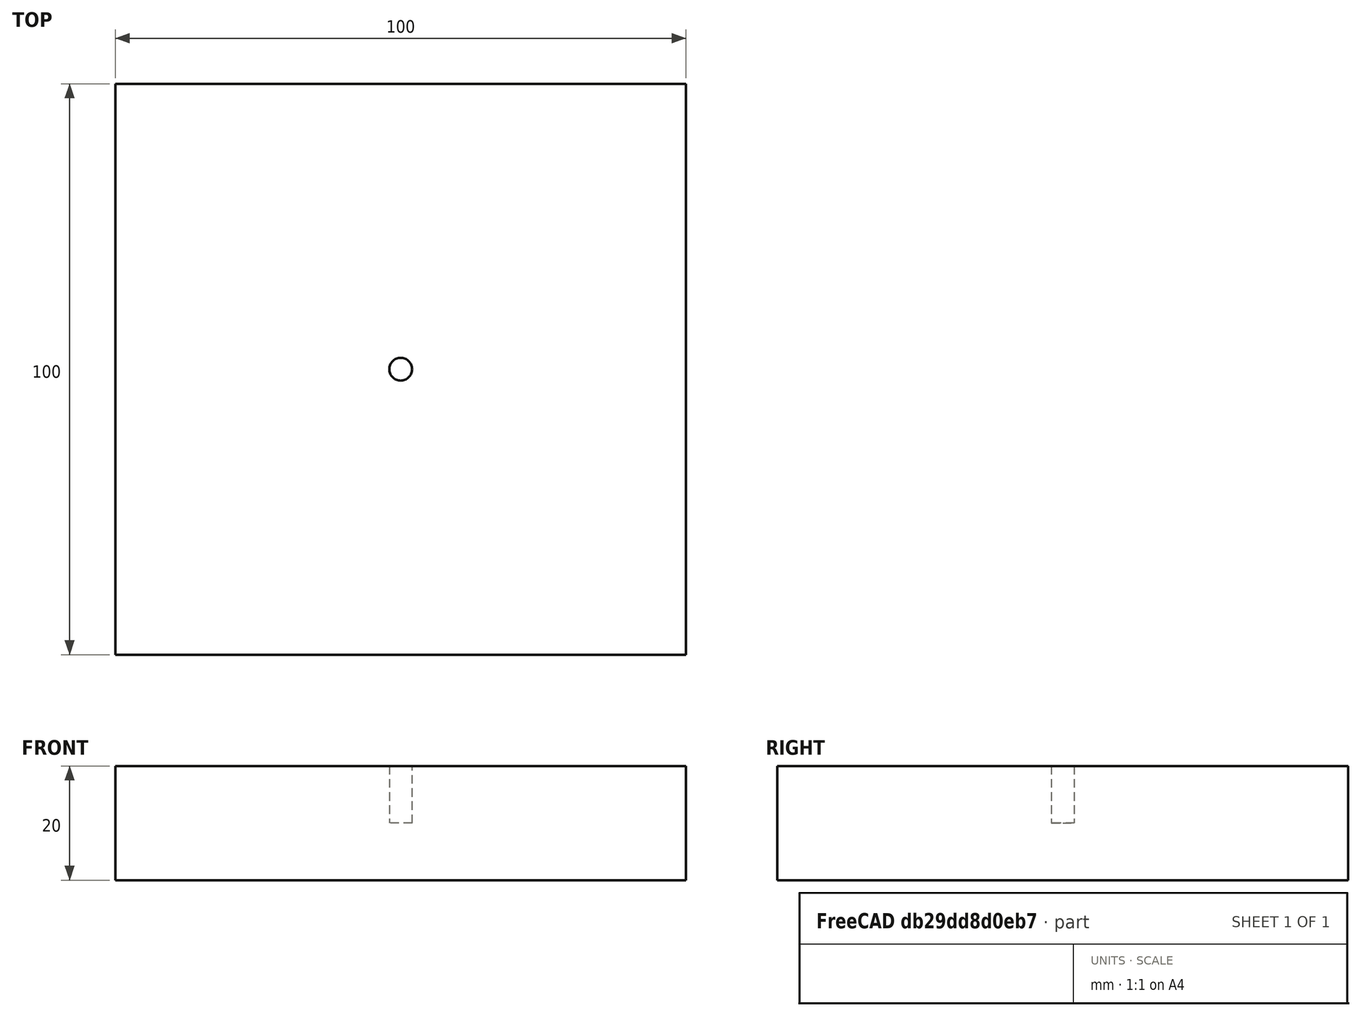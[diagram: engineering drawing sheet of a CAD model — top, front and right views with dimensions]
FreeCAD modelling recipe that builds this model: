
FCSTD DOCUMENT  (FreeCAD 0.19R24291 (Git))
Label: TestExtrudeSketch-Circle
License: All rights reserved
LicenseURL: http://en.wikipedia.org/wiki/All_rights_reserved
objects: App::DocumentObjectGroupPython×1089, Part::FeaturePython×1, Sketcher::SketchObject×1, Part::Extrusion×1, App::Part×1
note: 3 computed .brp shape members not serialized (recipe doc carries the construction recipe); baked Part::Feature solids carry a one-line shape summary decoded from their .brp

FEATURE [App::DocumentObjectGroupPython] HALFPI  # scripted group (container) (typed FeaturePython)
  name = HALFPI
  value = pi/2.
FEATURE [App::DocumentObjectGroupPython] PI  # scripted group (container) (typed FeaturePython)
  name = PI
  value = 1.*pi
FEATURE [App::DocumentObjectGroupPython] TWOPI  # scripted group (container) (typed FeaturePython)
  name = TWOPI
  value = 2.*pi
FEATURE [App::DocumentObjectGroupPython] Constants  # scripted group (container) (typed FeaturePython)
  Group = -> [HALFPI,PI,TWOPI]
FEATURE [App::DocumentObjectGroupPython] Variables  # scripted group (container) (typed FeaturePython)
FEATURE [App::DocumentObjectGroupPython] Quantities  # scripted group (container) (typed FeaturePython)
FEATURE [App::DocumentObjectGroupPython] Isotopes  # scripted group (container) (typed FeaturePython)
FEATURE [App::DocumentObjectGroupPython] Elements  # scripted group (container) (typed FeaturePython)
FEATURE [App::DocumentObjectGroupPython] Materials  # scripted group (container) (typed FeaturePython)
FEATURE [App::DocumentObjectGroupPython] G4Isotopes  # scripted group (container) (typed FeaturePython)
FEATURE [App::DocumentObjectGroupPython] H_element  # scripted group (container) (typed FeaturePython)
  Z = 1
  atom_value = 1.008
  formula = H
  name = H_element
FEATURE [App::DocumentObjectGroupPython] He_element  # scripted group (container) (typed FeaturePython)
  Z = 2
  atom_value = 4.0026
  formula = He
  name = He_element
FEATURE [App::DocumentObjectGroupPython] Li_element  # scripted group (container) (typed FeaturePython)
  Z = 3
  atom_value = 6.94
  formula = Li
  name = Li_element
FEATURE [App::DocumentObjectGroupPython] Be_element  # scripted group (container) (typed FeaturePython)
  Z = 4
  atom_value = 9.01218
  formula = Be
  name = Be_element
FEATURE [App::DocumentObjectGroupPython] B_element  # scripted group (container) (typed FeaturePython)
  Z = 5
  atom_value = 10.81
  formula = B
  name = B_element
FEATURE [App::DocumentObjectGroupPython] C_element  # scripted group (container) (typed FeaturePython)
  Z = 6
  atom_value = 12.011
  formula = C
  name = C_element
FEATURE [App::DocumentObjectGroupPython] N_element  # scripted group (container) (typed FeaturePython)
  Z = 7
  atom_value = 14.007
  formula = N
  name = N_element
FEATURE [App::DocumentObjectGroupPython] O_element  # scripted group (container) (typed FeaturePython)
  Z = 8
  atom_value = 15.999
  formula = O
  name = O_element
FEATURE [App::DocumentObjectGroupPython] F_element  # scripted group (container) (typed FeaturePython)
  Z = 9
  atom_value = 18.9984
  formula = F
  name = F_element
FEATURE [App::DocumentObjectGroupPython] Ne_element  # scripted group (container) (typed FeaturePython)
  Z = 10
  atom_value = 20.1797
  formula = Ne
  name = Ne_element
FEATURE [App::DocumentObjectGroupPython] Na_element  # scripted group (container) (typed FeaturePython)
  Z = 11
  atom_value = 22.9898
  formula = Na
  name = Na_element
FEATURE [App::DocumentObjectGroupPython] Mg_element  # scripted group (container) (typed FeaturePython)
  Z = 12
  atom_value = 24.305
  formula = Mg
  name = Mg_element
FEATURE [App::DocumentObjectGroupPython] Al_element  # scripted group (container) (typed FeaturePython)
  Z = 13
  atom_value = 26.9815
  formula = Al
  name = Al_element
FEATURE [App::DocumentObjectGroupPython] Si_element  # scripted group (container) (typed FeaturePython)
  Z = 14
  atom_value = 28.085
  formula = Si
  name = Si_element
FEATURE [App::DocumentObjectGroupPython] P_element  # scripted group (container) (typed FeaturePython)
  Z = 15
  atom_value = 30.9738
  formula = P
  name = P_element
FEATURE [App::DocumentObjectGroupPython] S_element  # scripted group (container) (typed FeaturePython)
  Z = 16
  atom_value = 32.06
  formula = S
  name = S_element
FEATURE [App::DocumentObjectGroupPython] Cl_element  # scripted group (container) (typed FeaturePython)
  Z = 17
  atom_value = 35.45
  formula = Cl
  name = Cl_element
FEATURE [App::DocumentObjectGroupPython] Ar_element  # scripted group (container) (typed FeaturePython)
  Z = 18
  atom_value = 39.95
  formula = Ar
  name = Ar_element
FEATURE [App::DocumentObjectGroupPython] K_element  # scripted group (container) (typed FeaturePython)
  Z = 19
  atom_value = 39.0983
  formula = K
  name = K_element
FEATURE [App::DocumentObjectGroupPython] Ca_element  # scripted group (container) (typed FeaturePython)
  Z = 20
  atom_value = 40.078
  formula = Ca
  name = Ca_element
FEATURE [App::DocumentObjectGroupPython] Sc_element  # scripted group (container) (typed FeaturePython)
  Z = 21
  atom_value = 44.9559
  formula = Sc
  name = Sc_element
FEATURE [App::DocumentObjectGroupPython] Ti_element  # scripted group (container) (typed FeaturePython)
  Z = 22
  atom_value = 47.867
  formula = Ti
  name = Ti_element
FEATURE [App::DocumentObjectGroupPython] V_element  # scripted group (container) (typed FeaturePython)
  Z = 23
  atom_value = 50.9415
  formula = V
  name = V_element
FEATURE [App::DocumentObjectGroupPython] Cr_element  # scripted group (container) (typed FeaturePython)
  Z = 24
  atom_value = 51.9961
  formula = Cr
  name = Cr_element
FEATURE [App::DocumentObjectGroupPython] Mn_element  # scripted group (container) (typed FeaturePython)
  Z = 25
  atom_value = 54.938
  formula = Mn
  name = Mn_element
FEATURE [App::DocumentObjectGroupPython] Fe_element  # scripted group (container) (typed FeaturePython)
  Z = 26
  atom_value = 55.845
  formula = Fe
  name = Fe_element
FEATURE [App::DocumentObjectGroupPython] Co_element  # scripted group (container) (typed FeaturePython)
  Z = 27
  atom_value = 58.9332
  formula = Co
  name = Co_element
FEATURE [App::DocumentObjectGroupPython] Ni_element  # scripted group (container) (typed FeaturePython)
  Z = 28
  atom_value = 58.6934
  formula = Ni
  name = Ni_element
FEATURE [App::DocumentObjectGroupPython] Cu_element  # scripted group (container) (typed FeaturePython)
  Z = 29
  atom_value = 63.546
  formula = Cu
  name = Cu_element
FEATURE [App::DocumentObjectGroupPython] Zn_element  # scripted group (container) (typed FeaturePython)
  Z = 30
  atom_value = 65.38
  formula = Zn
  name = Zn_element
FEATURE [App::DocumentObjectGroupPython] Ga_element  # scripted group (container) (typed FeaturePython)
  Z = 31
  atom_value = 69.723
  formula = Ga
  name = Ga_element
FEATURE [App::DocumentObjectGroupPython] Ge_element  # scripted group (container) (typed FeaturePython)
  Z = 32
  atom_value = 72.63
  formula = Ge
  name = Ge_element
FEATURE [App::DocumentObjectGroupPython] As_element  # scripted group (container) (typed FeaturePython)
  Z = 33
  atom_value = 74.9216
  formula = As
  name = As_element
FEATURE [App::DocumentObjectGroupPython] Se_element  # scripted group (container) (typed FeaturePython)
  Z = 34
  atom_value = 78.971
  formula = Se
  name = Se_element
FEATURE [App::DocumentObjectGroupPython] Br_element  # scripted group (container) (typed FeaturePython)
  Z = 35
  atom_value = 79.904
  formula = Br
  name = Br_element
FEATURE [App::DocumentObjectGroupPython] Kr_element  # scripted group (container) (typed FeaturePython)
  Z = 36
  atom_value = 83.798
  formula = Kr
  name = Kr_element
FEATURE [App::DocumentObjectGroupPython] Rb_element  # scripted group (container) (typed FeaturePython)
  Z = 37
  atom_value = 85.4678
  formula = Rb
  name = Rb_element
FEATURE [App::DocumentObjectGroupPython] Sr_element  # scripted group (container) (typed FeaturePython)
  Z = 38
  atom_value = 87.62
  formula = Sr
  name = Sr_element
FEATURE [App::DocumentObjectGroupPython] Y_element  # scripted group (container) (typed FeaturePython)
  Z = 39
  atom_value = 88.9058
  formula = Y
  name = Y_element
FEATURE [App::DocumentObjectGroupPython] Zr_element  # scripted group (container) (typed FeaturePython)
  Z = 40
  atom_value = 91.224
  formula = Zr
  name = Zr_element
FEATURE [App::DocumentObjectGroupPython] Nb_element  # scripted group (container) (typed FeaturePython)
  Z = 41
  atom_value = 92.9064
  formula = Nb
  name = Nb_element
FEATURE [App::DocumentObjectGroupPython] Mo_element  # scripted group (container) (typed FeaturePython)
  Z = 42
  atom_value = 95.95
  formula = Mo
  name = Mo_element
FEATURE [App::DocumentObjectGroupPython] Tc_element  # scripted group (container) (typed FeaturePython)
  Z = 43
  atom_value = 97
  formula = Tc
  name = Tc_element
FEATURE [App::DocumentObjectGroupPython] Ru_element  # scripted group (container) (typed FeaturePython)
  Z = 44
  atom_value = 101.07
  formula = Ru
  name = Ru_element
FEATURE [App::DocumentObjectGroupPython] Rh_element  # scripted group (container) (typed FeaturePython)
  Z = 45
  atom_value = 102.905
  formula = Rh
  name = Rh_element
FEATURE [App::DocumentObjectGroupPython] Pd_element  # scripted group (container) (typed FeaturePython)
  Z = 46
  atom_value = 106.42
  formula = Pd
  name = Pd_element
FEATURE [App::DocumentObjectGroupPython] Ag_element  # scripted group (container) (typed FeaturePython)
  Z = 47
  atom_value = 107.868
  formula = Ag
  name = Ag_element
FEATURE [App::DocumentObjectGroupPython] Cd_element  # scripted group (container) (typed FeaturePython)
  Z = 48
  atom_value = 112.414
  formula = Cd
  name = Cd_element
FEATURE [App::DocumentObjectGroupPython] In_element  # scripted group (container) (typed FeaturePython)
  Z = 49
  atom_value = 114.818
  formula = In
  name = In_element
FEATURE [App::DocumentObjectGroupPython] Sn_element  # scripted group (container) (typed FeaturePython)
  Z = 50
  atom_value = 118.71
  formula = Sn
  name = Sn_element
FEATURE [App::DocumentObjectGroupPython] Sb_element  # scripted group (container) (typed FeaturePython)
  Z = 51
  atom_value = 121.76
  formula = Sb
  name = Sb_element
FEATURE [App::DocumentObjectGroupPython] Te_element  # scripted group (container) (typed FeaturePython)
  Z = 52
  atom_value = 127.6
  formula = Te
  name = Te_element
FEATURE [App::DocumentObjectGroupPython] I_element  # scripted group (container) (typed FeaturePython)
  Z = 53
  atom_value = 126.904
  formula = I
  name = I_element
FEATURE [App::DocumentObjectGroupPython] Xe_element  # scripted group (container) (typed FeaturePython)
  Z = 54
  atom_value = 131.293
  formula = Xe
  name = Xe_element
FEATURE [App::DocumentObjectGroupPython] Cs_element  # scripted group (container) (typed FeaturePython)
  Z = 55
  atom_value = 132.905
  formula = Cs
  name = Cs_element
FEATURE [App::DocumentObjectGroupPython] Ba_element  # scripted group (container) (typed FeaturePython)
  Z = 56
  atom_value = 137.327
  formula = Ba
  name = Ba_element
FEATURE [App::DocumentObjectGroupPython] La_element  # scripted group (container) (typed FeaturePython)
  Z = 57
  atom_value = 138.905
  formula = La
  name = La_element
FEATURE [App::DocumentObjectGroupPython] Ce_element  # scripted group (container) (typed FeaturePython)
  Z = 58
  atom_value = 140.116
  formula = Ce
  name = Ce_element
FEATURE [App::DocumentObjectGroupPython] Pr_element  # scripted group (container) (typed FeaturePython)
  Z = 59
  atom_value = 140.908
  formula = Pr
  name = Pr_element
FEATURE [App::DocumentObjectGroupPython] Nd_element  # scripted group (container) (typed FeaturePython)
  Z = 60
  atom_value = 144.242
  formula = Nd
  name = Nd_element
FEATURE [App::DocumentObjectGroupPython] Pm_element  # scripted group (container) (typed FeaturePython)
  Z = 61
  atom_value = 145
  formula = Pm
  name = Pm_element
FEATURE [App::DocumentObjectGroupPython] Sm_element  # scripted group (container) (typed FeaturePython)
  Z = 62
  atom_value = 150.36
  formula = Sm
  name = Sm_element
FEATURE [App::DocumentObjectGroupPython] Eu_element  # scripted group (container) (typed FeaturePython)
  Z = 63
  atom_value = 151.964
  formula = Eu
  name = Eu_element
FEATURE [App::DocumentObjectGroupPython] Gd_element  # scripted group (container) (typed FeaturePython)
  Z = 64
  atom_value = 157.25
  formula = Gd
  name = Gd_element
FEATURE [App::DocumentObjectGroupPython] Tb_element  # scripted group (container) (typed FeaturePython)
  Z = 65
  atom_value = 158.925
  formula = Tb
  name = Tb_element
FEATURE [App::DocumentObjectGroupPython] Dy_element  # scripted group (container) (typed FeaturePython)
  Z = 66
  atom_value = 162.5
  formula = Dy
  name = Dy_element
FEATURE [App::DocumentObjectGroupPython] Ho_element  # scripted group (container) (typed FeaturePython)
  Z = 67
  atom_value = 164.93
  formula = Ho
  name = Ho_element
FEATURE [App::DocumentObjectGroupPython] Er_element  # scripted group (container) (typed FeaturePython)
  Z = 68
  atom_value = 167.259
  formula = Er
  name = Er_element
FEATURE [App::DocumentObjectGroupPython] Tm_element  # scripted group (container) (typed FeaturePython)
  Z = 69
  atom_value = 168.934
  formula = Tm
  name = Tm_element
FEATURE [App::DocumentObjectGroupPython] Yb_element  # scripted group (container) (typed FeaturePython)
  Z = 70
  atom_value = 173.045
  formula = Yb
  name = Yb_element
FEATURE [App::DocumentObjectGroupPython] Lu_element  # scripted group (container) (typed FeaturePython)
  Z = 71
  atom_value = 174.967
  formula = Lu
  name = Lu_element
FEATURE [App::DocumentObjectGroupPython] Hf_element  # scripted group (container) (typed FeaturePython)
  Z = 72
  atom_value = 178.49
  formula = Hf
  name = Hf_element
FEATURE [App::DocumentObjectGroupPython] Ta_element  # scripted group (container) (typed FeaturePython)
  Z = 73
  atom_value = 180.948
  formula = Ta
  name = Ta_element
FEATURE [App::DocumentObjectGroupPython] W_element  # scripted group (container) (typed FeaturePython)
  Z = 74
  atom_value = 183.84
  formula = W
  name = W_element
FEATURE [App::DocumentObjectGroupPython] Re_element  # scripted group (container) (typed FeaturePython)
  Z = 75
  atom_value = 186.207
  formula = Re
  name = Re_element
FEATURE [App::DocumentObjectGroupPython] Os_element  # scripted group (container) (typed FeaturePython)
  Z = 76
  atom_value = 190.23
  formula = Os
  name = Os_element
FEATURE [App::DocumentObjectGroupPython] Ir_element  # scripted group (container) (typed FeaturePython)
  Z = 77
  atom_value = 192.217
  formula = Ir
  name = Ir_element
FEATURE [App::DocumentObjectGroupPython] Pt_element  # scripted group (container) (typed FeaturePython)
  Z = 78
  atom_value = 195.084
  formula = Pt
  name = Pt_element
FEATURE [App::DocumentObjectGroupPython] Au_element  # scripted group (container) (typed FeaturePython)
  Z = 79
  atom_value = 196.967
  formula = Au
  name = Au_element
FEATURE [App::DocumentObjectGroupPython] Hg_element  # scripted group (container) (typed FeaturePython)
  Z = 80
  atom_value = 200.592
  formula = Hg
  name = Hg_element
FEATURE [App::DocumentObjectGroupPython] Tl_element  # scripted group (container) (typed FeaturePython)
  Z = 81
  atom_value = 204.38
  formula = Tl
  name = Tl_element
FEATURE [App::DocumentObjectGroupPython] Pb_element  # scripted group (container) (typed FeaturePython)
  Z = 82
  atom_value = 207.2
  formula = Pb
  name = Pb_element
FEATURE [App::DocumentObjectGroupPython] Bi_element  # scripted group (container) (typed FeaturePython)
  Z = 83
  atom_value = 208.98
  formula = Bi
  name = Bi_element
FEATURE [App::DocumentObjectGroupPython] Po_element  # scripted group (container) (typed FeaturePython)
  Z = 84
  atom_value = 209
  formula = Po
  name = Po_element
FEATURE [App::DocumentObjectGroupPython] At_element  # scripted group (container) (typed FeaturePython)
  Z = 85
  atom_value = 210
  formula = At
  name = At_element
FEATURE [App::DocumentObjectGroupPython] Rn_element  # scripted group (container) (typed FeaturePython)
  Z = 86
  atom_value = 222
  formula = Rn
  name = Rn_element
FEATURE [App::DocumentObjectGroupPython] Fr_element  # scripted group (container) (typed FeaturePython)
  Z = 87
  atom_value = 223
  formula = Fr
  name = Fr_element
FEATURE [App::DocumentObjectGroupPython] Ra_element  # scripted group (container) (typed FeaturePython)
  Z = 88
  atom_value = 226
  formula = Ra
  name = Ra_element
FEATURE [App::DocumentObjectGroupPython] Ac_element  # scripted group (container) (typed FeaturePython)
  Z = 89
  atom_value = 227
  formula = Ac
  name = Ac_element
FEATURE [App::DocumentObjectGroupPython] Th_element  # scripted group (container) (typed FeaturePython)
  Z = 90
  atom_value = 232.038
  formula = Th
  name = Th_element
FEATURE [App::DocumentObjectGroupPython] Pa_element  # scripted group (container) (typed FeaturePython)
  Z = 91
  atom_value = 231.036
  formula = Pa
  name = Pa_element
FEATURE [App::DocumentObjectGroupPython] U_element  # scripted group (container) (typed FeaturePython)
  Z = 92
  atom_value = 238.029
  formula = U
  name = U_element
FEATURE [App::DocumentObjectGroupPython] Np_element  # scripted group (container) (typed FeaturePython)
  Z = 93
  atom_value = 237
  formula = Np
  name = Np_element
FEATURE [App::DocumentObjectGroupPython] Pu_element  # scripted group (container) (typed FeaturePython)
  Z = 94
  atom_value = 244
  formula = Pu
  name = Pu_element
FEATURE [App::DocumentObjectGroupPython] Am_element  # scripted group (container) (typed FeaturePython)
  Z = 95
  atom_value = 243
  formula = Am
  name = Am_element
FEATURE [App::DocumentObjectGroupPython] Cm_element  # scripted group (container) (typed FeaturePython)
  Z = 96
  atom_value = 247
  formula = Cm
  name = Cm_element
FEATURE [App::DocumentObjectGroupPython] Bk_element  # scripted group (container) (typed FeaturePython)
  Z = 97
  atom_value = 247
  formula = Bk
  name = Bk_element
FEATURE [App::DocumentObjectGroupPython] Cf_element  # scripted group (container) (typed FeaturePython)
  Z = 98
  atom_value = 251
  formula = Cf
  name = Cf_element
FEATURE [App::DocumentObjectGroupPython] G4Elements  # scripted group (container) (typed FeaturePython)
  Group = -> [H_element,He_element,Li_element,Be_element,B_element,C_element,N_element,O_element,F_element,Ne_element,Na_element,Mg_element,Al_element,Si_element,P_element,S_element,Cl_element,Ar_element,K_element,Ca_element,Sc_element,Ti_element,V_element,Cr_element,Mn_element,Fe_element,Co_element,Ni_element,Cu_element,Zn_element,Ga_element,Ge_element,As_element,Se_element,Br_element,Kr_element,Rb_element,+61 more]
FEATURE [App::DocumentObjectGroupPython] H_element001  label="H_element : 0.101"  # scripted group (container) (typed FeaturePython)
  n = 0.101327
FEATURE [App::DocumentObjectGroupPython] C_element001  label="C_element : 0.775"  # scripted group (container) (typed FeaturePython)
  n = 0.7755
FEATURE [App::DocumentObjectGroupPython] N_element001  label="N_element : 0.035"  # scripted group (container) (typed FeaturePython)
  n = 0.035057
FEATURE [App::DocumentObjectGroupPython] O_element001  label="O_element : 0.052"  # scripted group (container) (typed FeaturePython)
  n = 0.0523159
FEATURE [App::DocumentObjectGroupPython] F_element001  label="F_element : 0.017"  # scripted group (container) (typed FeaturePython)
  n = 0.017422
FEATURE [App::DocumentObjectGroupPython] Ca_element001  label="Ca_element : 0.018"  # scripted group (container) (typed FeaturePython)
  n = 0.018378
FEATURE [App::DocumentObjectGroupPython] G4_A_150_TISSUE  # scripted group (container) (typed FeaturePython)
  Dunit = g/cm3
  Dvalue = 1.127
  Group = -> [H_element001,C_element001,N_element001,O_element001,F_element001,Ca_element001]
  conduct = 2
  density = 1
  expand = 3
  formula = G4_A-150_TISSUE
  name = G4_A-150_TISSUE
  specific = 4
FEATURE [App::DocumentObjectGroupPython] C_element002  label="C_element : 3"  # scripted group (container) (typed FeaturePython)
  n = 3
  ref = C_element
FEATURE [App::DocumentObjectGroupPython] H_element002  label="H_element : 6"  # scripted group (container) (typed FeaturePython)
  n = 6
  ref = H_element
FEATURE [App::DocumentObjectGroupPython] O_element002  label="O_element : 1"  # scripted group (container) (typed FeaturePython)
  n = 1
  ref = O_element
FEATURE [App::DocumentObjectGroupPython] G4_ACETONE  # scripted group (container) (typed FeaturePython)
  Dunit = g/cm3
  Dvalue = 0.7899
  Group = -> [C_element002,H_element002,O_element002]
  conduct = 2
  density = 1
  expand = 3
  formula = G4_ACETONE
  name = G4_ACETONE
  specific = 4
FEATURE [App::DocumentObjectGroupPython] C_element003  label="C_element : 2"  # scripted group (container) (typed FeaturePython)
  n = 2
  ref = C_element
FEATURE [App::DocumentObjectGroupPython] H_element003  label="H_element : 2"  # scripted group (container) (typed FeaturePython)
  n = 2
  ref = H_element
FEATURE [App::DocumentObjectGroupPython] G4_ACETYLENE  # scripted group (container) (typed FeaturePython)
  Dunit = g/cm3
  Dvalue = 0.0010967
  Group = -> [C_element003,H_element003]
  conduct = 2
  density = 1
  expand = 3
  formula = G4_ACETYLENE
  name = G4_ACETYLENE
  specific = 4
FEATURE [App::DocumentObjectGroupPython] C_element004  label="C_element : 5"  # scripted group (container) (typed FeaturePython)
  n = 5
  ref = C_element
FEATURE [App::DocumentObjectGroupPython] H_element004  label="H_element : 5"  # scripted group (container) (typed FeaturePython)
  n = 5
  ref = H_element
FEATURE [App::DocumentObjectGroupPython] N_element002  label="N_element : 5"  # scripted group (container) (typed FeaturePython)
  n = 5
  ref = N_element
FEATURE [App::DocumentObjectGroupPython] G4_ADENINE  # scripted group (container) (typed FeaturePython)
  Dunit = g/cm3
  Dvalue = 1.6
  Group = -> [C_element004,H_element004,N_element002]
  conduct = 2
  density = 1
  expand = 3
  formula = G4_ADENINE
  name = G4_ADENINE
  specific = 4
FEATURE [App::DocumentObjectGroupPython] H_element005  label="H_element : 0.114"  # scripted group (container) (typed FeaturePython)
  n = 0.114
FEATURE [App::DocumentObjectGroupPython] C_element005  label="C_element : 0.598"  # scripted group (container) (typed FeaturePython)
  n = 0.598
FEATURE [App::DocumentObjectGroupPython] N_element003  label="N_element : 0.007"  # scripted group (container) (typed FeaturePython)
  n = 0.007
FEATURE [App::DocumentObjectGroupPython] O_element003  label="O_element : 0.278"  # scripted group (container) (typed FeaturePython)
  n = 0.278
FEATURE [App::DocumentObjectGroupPython] Na_element001  label="Na_element : 0.001"  # scripted group (container) (typed FeaturePython)
  n = 0.001
FEATURE [App::DocumentObjectGroupPython] S_element001  label="S_element : 0.001"  # scripted group (container) (typed FeaturePython)
  n = 0.001
FEATURE [App::DocumentObjectGroupPython] Cl_element001  label="Cl_element : 0.001"  # scripted group (container) (typed FeaturePython)
  n = 0.001
FEATURE [App::DocumentObjectGroupPython] G4_ADIPOSE_TISSUE_ICRP  # scripted group (container) (typed FeaturePython)
  Dunit = g/cm3
  Dvalue = 0.95
  Group = -> [H_element005,C_element005,N_element003,O_element003,Na_element001,S_element001,Cl_element001]
  conduct = 2
  density = 1
  expand = 3
  formula = G4_ADIPOSE_TISSUE_ICRP
  name = G4_ADIPOSE_TISSUE_ICRP
  specific = 4
FEATURE [App::DocumentObjectGroupPython] C_element006  label="C_element : 0.000"  # scripted group (container) (typed FeaturePython)
  n = 0.000124
FEATURE [App::DocumentObjectGroupPython] N_element004  label="N_element : 0.755"  # scripted group (container) (typed FeaturePython)
  n = 0.755268
FEATURE [App::DocumentObjectGroupPython] O_element004  label="O_element : 0.232"  # scripted group (container) (typed FeaturePython)
  n = 0.231781
FEATURE [App::DocumentObjectGroupPython] Ar_element001  label="Ar_element : 0.013"  # scripted group (container) (typed FeaturePython)
  n = 0.012827
FEATURE [App::DocumentObjectGroupPython] G4_AIR  # scripted group (container) (typed FeaturePython)
  Dunit = g/cm3
  Dvalue = 0.00120479
  Group = -> [C_element006,N_element004,O_element004,Ar_element001]
  conduct = 2
  density = 1
  expand = 3
  formula = G4_AIR
  name = G4_AIR
  specific = 4
FEATURE [App::DocumentObjectGroupPython] C_element007  label="C_element : 006"  # scripted group (container) (typed FeaturePython)
  n = 3
  ref = C_element
FEATURE [App::DocumentObjectGroupPython] H_element006  label="H_element : 7"  # scripted group (container) (typed FeaturePython)
  n = 7
  ref = H_element
FEATURE [App::DocumentObjectGroupPython] N_element005  label="N_element : 1"  # scripted group (container) (typed FeaturePython)
  n = 1
  ref = N_element
FEATURE [App::DocumentObjectGroupPython] O_element005  label="O_element : 2"  # scripted group (container) (typed FeaturePython)
  n = 2
  ref = O_element
FEATURE [App::DocumentObjectGroupPython] G4_ALANINE  # scripted group (container) (typed FeaturePython)
  Dunit = g/cm3
  Dvalue = 1.42
  Group = -> [C_element007,H_element006,N_element005,O_element005]
  conduct = 2
  density = 1
  expand = 3
  formula = G4_ALANINE
  name = G4_ALANINE
  specific = 4
FEATURE [App::DocumentObjectGroupPython] Al_element001  label="Al_element : 2"  # scripted group (container) (typed FeaturePython)
  n = 2
  ref = Al_element
FEATURE [App::DocumentObjectGroupPython] O_element006  label="O_element : 3"  # scripted group (container) (typed FeaturePython)
  n = 3
  ref = O_element
FEATURE [App::DocumentObjectGroupPython] G4_ALUMINUM_OXIDE  # scripted group (container) (typed FeaturePython)
  Dunit = g/cm3
  Dvalue = 3.97
  Group = -> [Al_element001,O_element006]
  conduct = 2
  density = 1
  expand = 3
  formula = G4_ALUMINUM_OXIDE
  name = G4_ALUMINUM_OXIDE
  specific = 4
FEATURE [App::DocumentObjectGroupPython] H_element007  label="H_element : 0.106"  # scripted group (container) (typed FeaturePython)
  n = 0.10593
FEATURE [App::DocumentObjectGroupPython] C_element008  label="C_element : 0.789"  # scripted group (container) (typed FeaturePython)
  n = 0.788974
FEATURE [App::DocumentObjectGroupPython] O_element007  label="O_element : 0.105"  # scripted group (container) (typed FeaturePython)
  n = 0.105096
FEATURE [App::DocumentObjectGroupPython] G4_AMBER  # scripted group (container) (typed FeaturePython)
  Dunit = g/cm3
  Dvalue = 1.1
  Group = -> [H_element007,C_element008,O_element007]
  conduct = 2
  density = 1
  expand = 3
  formula = G4_AMBER
  name = G4_AMBER
  specific = 4
FEATURE [App::DocumentObjectGroupPython] N_element006  label="N_element : 006"  # scripted group (container) (typed FeaturePython)
  n = 1
  ref = N_element
FEATURE [App::DocumentObjectGroupPython] H_element008  label="H_element : 3"  # scripted group (container) (typed FeaturePython)
  n = 3
  ref = H_element
FEATURE [App::DocumentObjectGroupPython] G4_AMMONIA  # scripted group (container) (typed FeaturePython)
  Dunit = g/cm3
  Dvalue = 0.000826019
  Group = -> [N_element006,H_element008]
  conduct = 2
  density = 1
  expand = 3
  formula = G4_AMMONIA
  name = G4_AMMONIA
  specific = 4
FEATURE [App::DocumentObjectGroupPython] C_element009  label="C_element : 6"  # scripted group (container) (typed FeaturePython)
  n = 6
  ref = C_element
FEATURE [App::DocumentObjectGroupPython] H_element009  label="H_element : 008"  # scripted group (container) (typed FeaturePython)
  n = 7
  ref = H_element
FEATURE [App::DocumentObjectGroupPython] N_element007  label="N_element : 007"  # scripted group (container) (typed FeaturePython)
  n = 1
  ref = N_element
FEATURE [App::DocumentObjectGroupPython] G4_ANILINE  # scripted group (container) (typed FeaturePython)
  Dunit = g/cm3
  Dvalue = 1.0235
  Group = -> [C_element009,H_element009,N_element007]
  conduct = 2
  density = 1
  expand = 3
  formula = G4_ANILINE
  name = G4_ANILINE
  specific = 4
FEATURE [App::DocumentObjectGroupPython] C_element010  label="C_element : 14"  # scripted group (container) (typed FeaturePython)
  n = 14
  ref = C_element
FEATURE [App::DocumentObjectGroupPython] H_element010  label="H_element : 10"  # scripted group (container) (typed FeaturePython)
  n = 10
  ref = H_element
FEATURE [App::DocumentObjectGroupPython] G4_ANTHRACENE  # scripted group (container) (typed FeaturePython)
  Dunit = g/cm3
  Dvalue = 1.283
  Group = -> [C_element010,H_element010]
  conduct = 2
  density = 1
  expand = 3
  formula = G4_ANTHRACENE
  name = G4_ANTHRACENE
  specific = 4
FEATURE [App::DocumentObjectGroupPython] H_element011  label="H_element : 0.065"  # scripted group (container) (typed FeaturePython)
  n = 0.0654709
FEATURE [App::DocumentObjectGroupPython] C_element011  label="C_element : 0.537"  # scripted group (container) (typed FeaturePython)
  n = 0.536944
FEATURE [App::DocumentObjectGroupPython] N_element008  label="N_element : 0.021"  # scripted group (container) (typed FeaturePython)
  n = 0.0215
FEATURE [App::DocumentObjectGroupPython] O_element008  label="O_element : 0.032"  # scripted group (container) (typed FeaturePython)
  n = 0.032085
FEATURE [App::DocumentObjectGroupPython] F_element002  label="F_element : 0.167"  # scripted group (container) (typed FeaturePython)
  n = 0.167411
FEATURE [App::DocumentObjectGroupPython] Ca_element002  label="Ca_element : 0.177"  # scripted group (container) (typed FeaturePython)
  n = 0.176589
FEATURE [App::DocumentObjectGroupPython] G4_B_100_BONE  # scripted group (container) (typed FeaturePython)
  Dunit = g/cm3
  Dvalue = 1.45
  Group = -> [H_element011,C_element011,N_element008,O_element008,F_element002,Ca_element002]
  conduct = 2
  density = 1
  expand = 3
  formula = G4_B-100_BONE
  name = G4_B-100_BONE
  specific = 4
FEATURE [App::DocumentObjectGroupPython] H_element012  label="H_element : 0.057"  # scripted group (container) (typed FeaturePython)
  n = 0.057441
FEATURE [App::DocumentObjectGroupPython] C_element012  label="C_element : 0.790"  # scripted group (container) (typed FeaturePython)
  n = 0.774591
FEATURE [App::DocumentObjectGroupPython] O_element009  label="O_element : 0.168"  # scripted group (container) (typed FeaturePython)
  n = 0.167968
FEATURE [App::DocumentObjectGroupPython] G4_BAKELITE  # scripted group (container) (typed FeaturePython)
  Dunit = g/cm3
  Dvalue = 1.25
  Group = -> [H_element012,C_element012,O_element009]
  conduct = 2
  density = 1
  expand = 3
  formula = G4_BAKELITE
  name = G4_BAKELITE
  specific = 4
FEATURE [App::DocumentObjectGroupPython] Ba_element001  label="Ba_element : 1"  # scripted group (container) (typed FeaturePython)
  n = 1
  ref = Ba_element
FEATURE [App::DocumentObjectGroupPython] F_element003  label="F_element : 2"  # scripted group (container) (typed FeaturePython)
  n = 2
  ref = F_element
FEATURE [App::DocumentObjectGroupPython] G4_BARIUM_FLUORIDE  # scripted group (container) (typed FeaturePython)
  Dunit = g/cm3
  Dvalue = 4.89
  Group = -> [Ba_element001,F_element003]
  conduct = 2
  density = 1
  expand = 3
  formula = G4_BARIUM_FLUORIDE
  name = G4_BARIUM_FLUORIDE
  specific = 4
FEATURE [App::DocumentObjectGroupPython] Ba_element002  label="Ba_element : 002"  # scripted group (container) (typed FeaturePython)
  n = 1
  ref = Ba_element
FEATURE [App::DocumentObjectGroupPython] S_element002  label="S_element : 1"  # scripted group (container) (typed FeaturePython)
  n = 1
  ref = S_element
FEATURE [App::DocumentObjectGroupPython] O_element010  label="O_element : 4"  # scripted group (container) (typed FeaturePython)
  n = 4
  ref = O_element
FEATURE [App::DocumentObjectGroupPython] G4_BARIUM_SULFATE  # scripted group (container) (typed FeaturePython)
  Dunit = g/cm3
  Dvalue = 4.5
  Group = -> [Ba_element002,S_element002,O_element010]
  conduct = 2
  density = 1
  expand = 3
  formula = G4_BARIUM_SULFATE
  name = G4_BARIUM_SULFATE
  specific = 4
FEATURE [App::DocumentObjectGroupPython] C_element013  label="C_element : 007"  # scripted group (container) (typed FeaturePython)
  n = 6
  ref = C_element
FEATURE [App::DocumentObjectGroupPython] H_element013  label="H_element : 009"  # scripted group (container) (typed FeaturePython)
  n = 6
  ref = H_element
FEATURE [App::DocumentObjectGroupPython] G4_BENZENE  # scripted group (container) (typed FeaturePython)
  Dunit = g/cm3
  Dvalue = 0.87865
  Group = -> [C_element013,H_element013]
  conduct = 2
  density = 1
  expand = 3
  formula = G4_BENZENE
  name = G4_BENZENE
  specific = 4
FEATURE [App::DocumentObjectGroupPython] Be_element001  label="Be_element : 1"  # scripted group (container) (typed FeaturePython)
  n = 1
  ref = Be_element
FEATURE [App::DocumentObjectGroupPython] O_element011  label="O_element : 005"  # scripted group (container) (typed FeaturePython)
  n = 1
  ref = O_element
FEATURE [App::DocumentObjectGroupPython] G4_BERYLLIUM_OXIDE  # scripted group (container) (typed FeaturePython)
  Dunit = g/cm3
  Dvalue = 3.01
  Group = -> [Be_element001,O_element011]
  conduct = 2
  density = 1
  expand = 3
  formula = G4_BERYLLIUM_OXIDE
  name = G4_BERYLLIUM_OXIDE
  specific = 4
FEATURE [App::DocumentObjectGroupPython] Bi_element001  label="Bi_element : 4"  # scripted group (container) (typed FeaturePython)
  n = 4
  ref = Bi_element
FEATURE [App::DocumentObjectGroupPython] Ge_element001  label="Ge_element : 3"  # scripted group (container) (typed FeaturePython)
  n = 3
  ref = Ge_element
FEATURE [App::DocumentObjectGroupPython] O_element012  label="O_element : 12"  # scripted group (container) (typed FeaturePython)
  n = 12
  ref = O_element
FEATURE [App::DocumentObjectGroupPython] G4_BGO  # scripted group (container) (typed FeaturePython)
  Dunit = g/cm3
  Dvalue = 7.13
  Group = -> [Bi_element001,Ge_element001,O_element012]
  conduct = 2
  density = 1
  expand = 3
  formula = G4_BGO
  name = G4_BGO
  specific = 4
FEATURE [App::DocumentObjectGroupPython] H_element014  label="H_element : 0.102"  # scripted group (container) (typed FeaturePython)
  n = 0.102
FEATURE [App::DocumentObjectGroupPython] C_element014  label="C_element : 0.110"  # scripted group (container) (typed FeaturePython)
  n = 0.11
FEATURE [App::DocumentObjectGroupPython] N_element009  label="N_element : 0.033"  # scripted group (container) (typed FeaturePython)
  n = 0.033
FEATURE [App::DocumentObjectGroupPython] O_element013  label="O_element : 0.745"  # scripted group (container) (typed FeaturePython)
  n = 0.745
FEATURE [App::DocumentObjectGroupPython] Na_element002  label="Na_element : 0.002"  # scripted group (container) (typed FeaturePython)
  n = 0.001
FEATURE [App::DocumentObjectGroupPython] P_element001  label="P_element : 0.001"  # scripted group (container) (typed FeaturePython)
  n = 0.001
FEATURE [App::DocumentObjectGroupPython] S_element003  label="S_element : 0.002"  # scripted group (container) (typed FeaturePython)
  n = 0.002
FEATURE [App::DocumentObjectGroupPython] Cl_element002  label="Cl_element : 0.003"  # scripted group (container) (typed FeaturePython)
  n = 0.003
FEATURE [App::DocumentObjectGroupPython] K_element001  label="K_element : 0.002"  # scripted group (container) (typed FeaturePython)
  n = 0.002
FEATURE [App::DocumentObjectGroupPython] Fe_element001  label="Fe_element : 0.001"  # scripted group (container) (typed FeaturePython)
  n = 0.001
FEATURE [App::DocumentObjectGroupPython] G4_BLOOD_ICRP  # scripted group (container) (typed FeaturePython)
  Dunit = g/cm3
  Dvalue = 1.06
  Group = -> [H_element014,C_element014,N_element009,O_element013,Na_element002,P_element001,S_element003,Cl_element002,K_element001,Fe_element001]
  conduct = 2
  density = 1
  expand = 3
  formula = G4_BLOOD_ICRP
  name = G4_BLOOD_ICRP
  specific = 4
FEATURE [App::DocumentObjectGroupPython] H_element015  label="H_element : 0.064"  # scripted group (container) (typed FeaturePython)
  n = 0.064
FEATURE [App::DocumentObjectGroupPython] C_element015  label="C_element : 0.278"  # scripted group (container) (typed FeaturePython)
  n = 0.278
FEATURE [App::DocumentObjectGroupPython] N_element010  label="N_element : 0.027"  # scripted group (container) (typed FeaturePython)
  n = 0.027
FEATURE [App::DocumentObjectGroupPython] O_element014  label="O_element : 0.410"  # scripted group (container) (typed FeaturePython)
  n = 0.41
FEATURE [App::DocumentObjectGroupPython] Mg_element001  label="Mg_element : 0.002"  # scripted group (container) (typed FeaturePython)
  n = 0.002
FEATURE [App::DocumentObjectGroupPython] P_element002  label="P_element : 0.070"  # scripted group (container) (typed FeaturePython)
  n = 0.07
FEATURE [App::DocumentObjectGroupPython] S_element004  label="S_element : 0.003"  # scripted group (container) (typed FeaturePython)
  n = 0.002
FEATURE [App::DocumentObjectGroupPython] Ca_element003  label="Ca_element : 0.147"  # scripted group (container) (typed FeaturePython)
  n = 0.147
FEATURE [App::DocumentObjectGroupPython] G4_BONE_COMPACT_ICRU  # scripted group (container) (typed FeaturePython)
  Dunit = g/cm3
  Dvalue = 1.85
  Group = -> [H_element015,C_element015,N_element010,O_element014,Mg_element001,P_element002,S_element004,Ca_element003]
  conduct = 2
  density = 1
  expand = 3
  formula = G4_BONE_COMPACT_ICRU
  name = G4_BONE_COMPACT_ICRU
  specific = 4
FEATURE [App::DocumentObjectGroupPython] H_element016  label="H_element : 0.034"  # scripted group (container) (typed FeaturePython)
  n = 0.034
FEATURE [App::DocumentObjectGroupPython] C_element016  label="C_element : 0.155"  # scripted group (container) (typed FeaturePython)
  n = 0.155
FEATURE [App::DocumentObjectGroupPython] N_element011  label="N_element : 0.042"  # scripted group (container) (typed FeaturePython)
  n = 0.042
FEATURE [App::DocumentObjectGroupPython] O_element015  label="O_element : 0.435"  # scripted group (container) (typed FeaturePython)
  n = 0.435
FEATURE [App::DocumentObjectGroupPython] Na_element003  label="Na_element : 0.003"  # scripted group (container) (typed FeaturePython)
  n = 0.001
FEATURE [App::DocumentObjectGroupPython] Mg_element002  label="Mg_element : 0.003"  # scripted group (container) (typed FeaturePython)
  n = 0.002
FEATURE [App::DocumentObjectGroupPython] P_element003  label="P_element : 0.103"  # scripted group (container) (typed FeaturePython)
  n = 0.103
FEATURE [App::DocumentObjectGroupPython] S_element005  label="S_element : 0.004"  # scripted group (container) (typed FeaturePython)
  n = 0.003
FEATURE [App::DocumentObjectGroupPython] Ca_element004  label="Ca_element : 0.225"  # scripted group (container) (typed FeaturePython)
  n = 0.225
FEATURE [App::DocumentObjectGroupPython] G4_BONE_CORTICAL_ICRP  # scripted group (container) (typed FeaturePython)
  Dunit = g/cm3
  Dvalue = 1.92
  Group = -> [H_element016,C_element016,N_element011,O_element015,Na_element003,Mg_element002,P_element003,S_element005,Ca_element004]
  conduct = 2
  density = 1
  expand = 3
  formula = G4_BONE_CORTICAL_ICRP
  name = G4_BONE_CORTICAL_ICRP
  specific = 4
FEATURE [App::DocumentObjectGroupPython] B_element001  label="B_element : 4"  # scripted group (container) (typed FeaturePython)
  n = 4
  ref = B_element
FEATURE [App::DocumentObjectGroupPython] C_element017  label="C_element : 1"  # scripted group (container) (typed FeaturePython)
  n = 1
  ref = C_element
FEATURE [App::DocumentObjectGroupPython] G4_BORON_CARBIDE  # scripted group (container) (typed FeaturePython)
  Dunit = g/cm3
  Dvalue = 2.52
  Group = -> [B_element001,C_element017]
  conduct = 2
  density = 1
  expand = 3
  formula = G4_BORON_CARBIDE
  name = G4_BORON_CARBIDE
  specific = 4
FEATURE [App::DocumentObjectGroupPython] B_element002  label="B_element : 2"  # scripted group (container) (typed FeaturePython)
  n = 2
  ref = B_element
FEATURE [App::DocumentObjectGroupPython] O_element016  label="O_element : 006"  # scripted group (container) (typed FeaturePython)
  n = 3
  ref = O_element
FEATURE [App::DocumentObjectGroupPython] G4_BORON_OXIDE  # scripted group (container) (typed FeaturePython)
  Dunit = g/cm3
  Dvalue = 1.812
  Group = -> [B_element002,O_element016]
  conduct = 2
  density = 1
  expand = 3
  formula = G4_BORON_OXIDE
  name = G4_BORON_OXIDE
  specific = 4
FEATURE [App::DocumentObjectGroupPython] H_element017  label="H_element : 0.107"  # scripted group (container) (typed FeaturePython)
  n = 0.107
FEATURE [App::DocumentObjectGroupPython] C_element018  label="C_element : 0.145"  # scripted group (container) (typed FeaturePython)
  n = 0.145
FEATURE [App::DocumentObjectGroupPython] N_element012  label="N_element : 0.022"  # scripted group (container) (typed FeaturePython)
  n = 0.022
FEATURE [App::DocumentObjectGroupPython] O_element017  label="O_element : 0.712"  # scripted group (container) (typed FeaturePython)
  n = 0.712
FEATURE [App::DocumentObjectGroupPython] Na_element004  label="Na_element : 0.004"  # scripted group (container) (typed FeaturePython)
  n = 0.002
FEATURE [App::DocumentObjectGroupPython] P_element004  label="P_element : 0.004"  # scripted group (container) (typed FeaturePython)
  n = 0.004
FEATURE [App::DocumentObjectGroupPython] S_element006  label="S_element : 0.005"  # scripted group (container) (typed FeaturePython)
  n = 0.002
FEATURE [App::DocumentObjectGroupPython] Cl_element003  label="Cl_element : 0.004"  # scripted group (container) (typed FeaturePython)
  n = 0.003
FEATURE [App::DocumentObjectGroupPython] K_element002  label="K_element : 0.003"  # scripted group (container) (typed FeaturePython)
  n = 0.003
FEATURE [App::DocumentObjectGroupPython] G4_BRAIN_ICRP  # scripted group (container) (typed FeaturePython)
  Dunit = g/cm3
  Dvalue = 1.04
  Group = -> [H_element017,C_element018,N_element012,O_element017,Na_element004,P_element004,S_element006,Cl_element003,K_element002]
  conduct = 2
  density = 1
  expand = 3
  formula = G4_BRAIN_ICRP
  name = G4_BRAIN_ICRP
  specific = 4
FEATURE [App::DocumentObjectGroupPython] C_element019  label="C_element : 4"  # scripted group (container) (typed FeaturePython)
  n = 4
  ref = C_element
FEATURE [App::DocumentObjectGroupPython] H_element018  label="H_element : 010"  # scripted group (container) (typed FeaturePython)
  n = 10
  ref = H_element
FEATURE [App::DocumentObjectGroupPython] G4_BUTANE  # scripted group (container) (typed FeaturePython)
  Dunit = g/cm3
  Dvalue = 0.00249343
  Group = -> [C_element019,H_element018]
  conduct = 2
  density = 1
  expand = 3
  formula = G4_BUTANE
  name = G4_BUTANE
  specific = 4
FEATURE [App::DocumentObjectGroupPython] C_element020  label="C_element : 008"  # scripted group (container) (typed FeaturePython)
  n = 4
  ref = C_element
FEATURE [App::DocumentObjectGroupPython] H_element019  label="H_element : 011"  # scripted group (container) (typed FeaturePython)
  n = 10
  ref = H_element
FEATURE [App::DocumentObjectGroupPython] O_element018  label="O_element : 007"  # scripted group (container) (typed FeaturePython)
  n = 1
  ref = O_element
FEATURE [App::DocumentObjectGroupPython] G4_N_BUTYL_ALCOHOL  # scripted group (container) (typed FeaturePython)
  Dunit = g/cm3
  Dvalue = 0.8098
  Group = -> [C_element020,H_element019,O_element018]
  conduct = 2
  density = 1
  expand = 3
  formula = G4_N-BUTYL_ALCOHOL
  name = G4_N-BUTYL_ALCOHOL
  specific = 4
FEATURE [App::DocumentObjectGroupPython] H_element020  label="H_element : 0.025"  # scripted group (container) (typed FeaturePython)
  n = 0.02468
FEATURE [App::DocumentObjectGroupPython] C_element021  label="C_element : 0.502"  # scripted group (container) (typed FeaturePython)
  n = 0.501611
FEATURE [App::DocumentObjectGroupPython] O_element019  label="O_element : 0.005"  # scripted group (container) (typed FeaturePython)
  n = 0.004527
FEATURE [App::DocumentObjectGroupPython] F_element004  label="F_element : 0.465"  # scripted group (container) (typed FeaturePython)
  n = 0.465209
FEATURE [App::DocumentObjectGroupPython] Si_element001  label="Si_element : 0.004"  # scripted group (container) (typed FeaturePython)
  n = 0.003973
FEATURE [App::DocumentObjectGroupPython] G4_C_552  # scripted group (container) (typed FeaturePython)
  Dunit = g/cm3
  Dvalue = 1.76
  Group = -> [H_element020,C_element021,O_element019,F_element004,Si_element001]
  conduct = 2
  density = 1
  expand = 3
  formula = G4_C-552
  name = G4_C-552
  specific = 4
FEATURE [App::DocumentObjectGroupPython] Cd_element001  label="Cd_element : 1"  # scripted group (container) (typed FeaturePython)
  n = 1
  ref = Cd_element
FEATURE [App::DocumentObjectGroupPython] Te_element001  label="Te_element : 1"  # scripted group (container) (typed FeaturePython)
  n = 1
  ref = Te_element
FEATURE [App::DocumentObjectGroupPython] G4_CADMIUM_TELLURIDE  # scripted group (container) (typed FeaturePython)
  Dunit = g/cm3
  Dvalue = 6.2
  Group = -> [Cd_element001,Te_element001]
  conduct = 2
  density = 1
  expand = 3
  formula = G4_CADMIUM_TELLURIDE
  name = G4_CADMIUM_TELLURIDE
  specific = 4
FEATURE [App::DocumentObjectGroupPython] Cd_element002  label="Cd_element : 002"  # scripted group (container) (typed FeaturePython)
  n = 1
  ref = Cd_element
FEATURE [App::DocumentObjectGroupPython] W_element001  label="W_element : 1"  # scripted group (container) (typed FeaturePython)
  n = 1
  ref = W_element
FEATURE [App::DocumentObjectGroupPython] O_element020  label="O_element : 008"  # scripted group (container) (typed FeaturePython)
  n = 4
  ref = O_element
FEATURE [App::DocumentObjectGroupPython] G4_CADMIUM_TUNGSTATE  # scripted group (container) (typed FeaturePython)
  Dunit = g/cm3
  Dvalue = 7.9
  Group = -> [Cd_element002,W_element001,O_element020]
  conduct = 2
  density = 1
  expand = 3
  formula = G4_CADMIUM_TUNGSTATE
  name = G4_CADMIUM_TUNGSTATE
  specific = 4
FEATURE [App::DocumentObjectGroupPython] Ca_element005  label="Ca_element : 1"  # scripted group (container) (typed FeaturePython)
  n = 1
  ref = Ca_element
FEATURE [App::DocumentObjectGroupPython] C_element022  label="C_element : 009"  # scripted group (container) (typed FeaturePython)
  n = 1
  ref = C_element
FEATURE [App::DocumentObjectGroupPython] O_element021  label="O_element : 009"  # scripted group (container) (typed FeaturePython)
  n = 3
  ref = O_element
FEATURE [App::DocumentObjectGroupPython] G4_CALCIUM_CARBONATE  # scripted group (container) (typed FeaturePython)
  Dunit = g/cm3
  Dvalue = 2.8
  Group = -> [Ca_element005,C_element022,O_element021]
  conduct = 2
  density = 1
  expand = 3
  formula = G4_CALCIUM_CARBONATE
  name = G4_CALCIUM_CARBONATE
  specific = 4
FEATURE [App::DocumentObjectGroupPython] Ca_element006  label="Ca_element : 002"  # scripted group (container) (typed FeaturePython)
  n = 1
  ref = Ca_element
FEATURE [App::DocumentObjectGroupPython] F_element005  label="F_element : 003"  # scripted group (container) (typed FeaturePython)
  n = 2
  ref = F_element
FEATURE [App::DocumentObjectGroupPython] G4_CALCIUM_FLUORIDE  # scripted group (container) (typed FeaturePython)
  Dunit = g/cm3
  Dvalue = 3.18
  Group = -> [Ca_element006,F_element005]
  conduct = 2
  density = 1
  expand = 3
  formula = G4_CALCIUM_FLUORIDE
  name = G4_CALCIUM_FLUORIDE
  specific = 4
FEATURE [App::DocumentObjectGroupPython] Ca_element007  label="Ca_element : 003"  # scripted group (container) (typed FeaturePython)
  n = 1
  ref = Ca_element
FEATURE [App::DocumentObjectGroupPython] O_element022  label="O_element : 010"  # scripted group (container) (typed FeaturePython)
  n = 1
  ref = O_element
FEATURE [App::DocumentObjectGroupPython] G4_CALCIUM_OXIDE  # scripted group (container) (typed FeaturePython)
  Dunit = g/cm3
  Dvalue = 3.3
  Group = -> [Ca_element007,O_element022]
  conduct = 2
  density = 1
  expand = 3
  formula = G4_CALCIUM_OXIDE
  name = G4_CALCIUM_OXIDE
  specific = 4
FEATURE [App::DocumentObjectGroupPython] Ca_element008  label="Ca_element : 004"  # scripted group (container) (typed FeaturePython)
  n = 1
  ref = Ca_element
FEATURE [App::DocumentObjectGroupPython] S_element007  label="S_element : 002"  # scripted group (container) (typed FeaturePython)
  n = 1
  ref = S_element
FEATURE [App::DocumentObjectGroupPython] O_element023  label="O_element : 011"  # scripted group (container) (typed FeaturePython)
  n = 4
  ref = O_element
FEATURE [App::DocumentObjectGroupPython] G4_CALCIUM_SULFATE  # scripted group (container) (typed FeaturePython)
  Dunit = g/cm3
  Dvalue = 2.96
  Group = -> [Ca_element008,S_element007,O_element023]
  conduct = 2
  density = 1
  expand = 3
  formula = G4_CALCIUM_SULFATE
  name = G4_CALCIUM_SULFATE
  specific = 4
FEATURE [App::DocumentObjectGroupPython] Ca_element009  label="Ca_element : 005"  # scripted group (container) (typed FeaturePython)
  n = 1
  ref = Ca_element
FEATURE [App::DocumentObjectGroupPython] W_element002  label="W_element : 002"  # scripted group (container) (typed FeaturePython)
  n = 1
  ref = W_element
FEATURE [App::DocumentObjectGroupPython] O_element024  label="O_element : 012"  # scripted group (container) (typed FeaturePython)
  n = 4
  ref = O_element
FEATURE [App::DocumentObjectGroupPython] G4_CALCIUM_TUNGSTATE  # scripted group (container) (typed FeaturePython)
  Dunit = g/cm3
  Dvalue = 6.062
  Group = -> [Ca_element009,W_element002,O_element024]
  conduct = 2
  density = 1
  expand = 3
  formula = G4_CALCIUM_TUNGSTATE
  name = G4_CALCIUM_TUNGSTATE
  specific = 4
FEATURE [App::DocumentObjectGroupPython] C_element023  label="C_element : 010"  # scripted group (container) (typed FeaturePython)
  n = 1
  ref = C_element
FEATURE [App::DocumentObjectGroupPython] O_element025  label="O_element : 013"  # scripted group (container) (typed FeaturePython)
  n = 2
  ref = O_element
FEATURE [App::DocumentObjectGroupPython] G4_CARBON_DIOXIDE  # scripted group (container) (typed FeaturePython)
  Dunit = g/cm3
  Dvalue = 0.00184212
  Group = -> [C_element023,O_element025]
  conduct = 2
  density = 1
  expand = 3
  formula = G4_CARBON_DIOXIDE
  name = G4_CARBON_DIOXIDE
  specific = 4
FEATURE [App::DocumentObjectGroupPython] C_element024  label="C_element : 011"  # scripted group (container) (typed FeaturePython)
  n = 1
  ref = C_element
FEATURE [App::DocumentObjectGroupPython] Cl_element004  label="Cl_element : 4"  # scripted group (container) (typed FeaturePython)
  n = 4
  ref = Cl_element
FEATURE [App::DocumentObjectGroupPython] G4_CARBON_TETRACHLORIDE  # scripted group (container) (typed FeaturePython)
  Dunit = g/cm3
  Dvalue = 1.594
  Group = -> [C_element024,Cl_element004]
  conduct = 2
  density = 1
  expand = 3
  formula = G4_CARBON_TETRACHLORIDE
  name = G4_CARBON_TETRACHLORIDE
  specific = 4
FEATURE [App::DocumentObjectGroupPython] C_element025  label="C_element : 012"  # scripted group (container) (typed FeaturePython)
  n = 6
  ref = C_element
FEATURE [App::DocumentObjectGroupPython] H_element021  label="H_element : 012"  # scripted group (container) (typed FeaturePython)
  n = 10
  ref = H_element
FEATURE [App::DocumentObjectGroupPython] O_element026  label="O_element : 5"  # scripted group (container) (typed FeaturePython)
  n = 5
  ref = O_element
FEATURE [App::DocumentObjectGroupPython] G4_CELLULOSE_CELLOPHANE  # scripted group (container) (typed FeaturePython)
  Dunit = g/cm3
  Dvalue = 1.42
  Group = -> [C_element025,H_element021,O_element026]
  conduct = 2
  density = 1
  expand = 3
  formula = G4_CELLULOSE_CELLOPHANE
  name = G4_CELLULOSE_CELLOPHANE
  specific = 4
FEATURE [App::DocumentObjectGroupPython] H_element022  label="H_element : 0.067"  # scripted group (container) (typed FeaturePython)
  n = 0.067125
FEATURE [App::DocumentObjectGroupPython] C_element026  label="C_element : 0.545"  # scripted group (container) (typed FeaturePython)
  n = 0.545403
FEATURE [App::DocumentObjectGroupPython] O_element027  label="O_element : 0.387"  # scripted group (container) (typed FeaturePython)
  n = 0.387472
FEATURE [App::DocumentObjectGroupPython] G4_CELLULOSE_BUTYRATE  # scripted group (container) (typed FeaturePython)
  Dunit = g/cm3
  Dvalue = 1.2
  Group = -> [H_element022,C_element026,O_element027]
  conduct = 2
  density = 1
  expand = 3
  formula = G4_CELLULOSE_BUTYRATE
  name = G4_CELLULOSE_BUTYRATE
  specific = 4
FEATURE [App::DocumentObjectGroupPython] H_element023  label="H_element : 0.029"  # scripted group (container) (typed FeaturePython)
  n = 0.029216
FEATURE [App::DocumentObjectGroupPython] C_element027  label="C_element : 0.271"  # scripted group (container) (typed FeaturePython)
  n = 0.271296
FEATURE [App::DocumentObjectGroupPython] N_element013  label="N_element : 0.121"  # scripted group (container) (typed FeaturePython)
  n = 0.121276
FEATURE [App::DocumentObjectGroupPython] O_element028  label="O_element : 0.578"  # scripted group (container) (typed FeaturePython)
  n = 0.578212
FEATURE [App::DocumentObjectGroupPython] G4_CELLULOSE_NITRATE  # scripted group (container) (typed FeaturePython)
  Dunit = g/cm3
  Dvalue = 1.49
  Group = -> [H_element023,C_element027,N_element013,O_element028]
  conduct = 2
  density = 1
  expand = 3
  formula = G4_CELLULOSE_NITRATE
  name = G4_CELLULOSE_NITRATE
  specific = 4
FEATURE [App::DocumentObjectGroupPython] H_element024  label="H_element : 0.108"  # scripted group (container) (typed FeaturePython)
  n = 0.107596
FEATURE [App::DocumentObjectGroupPython] N_element014  label="N_element : 0.001"  # scripted group (container) (typed FeaturePython)
  n = 0.0008
FEATURE [App::DocumentObjectGroupPython] O_element029  label="O_element : 0.875"  # scripted group (container) (typed FeaturePython)
  n = 0.874976
FEATURE [App::DocumentObjectGroupPython] S_element008  label="S_element : 0.015"  # scripted group (container) (typed FeaturePython)
  n = 0.014627
FEATURE [App::DocumentObjectGroupPython] Ce_element001  label="Ce_element : 0.002"  # scripted group (container) (typed FeaturePython)
  n = 0.002001
FEATURE [App::DocumentObjectGroupPython] G4_CERIC_SULFATE  # scripted group (container) (typed FeaturePython)
  Dunit = g/cm3
  Dvalue = 1.03
  Group = -> [H_element024,N_element014,O_element029,S_element008,Ce_element001]
  conduct = 2
  density = 1
  expand = 3
  formula = G4_CERIC_SULFATE
  name = G4_CERIC_SULFATE
  specific = 4
FEATURE [App::DocumentObjectGroupPython] Cs_element001  label="Cs_element : 1"  # scripted group (container) (typed FeaturePython)
  n = 1
  ref = Cs_element
FEATURE [App::DocumentObjectGroupPython] F_element006  label="F_element : 1"  # scripted group (container) (typed FeaturePython)
  n = 1
  ref = F_element
FEATURE [App::DocumentObjectGroupPython] G4_CESIUM_FLUORIDE  # scripted group (container) (typed FeaturePython)
  Dunit = g/cm3
  Dvalue = 4.115
  Group = -> [Cs_element001,F_element006]
  conduct = 2
  density = 1
  expand = 3
  formula = G4_CESIUM_FLUORIDE
  name = G4_CESIUM_FLUORIDE
  specific = 4
FEATURE [App::DocumentObjectGroupPython] Cs_element002  label="Cs_element : 002"  # scripted group (container) (typed FeaturePython)
  n = 1
  ref = Cs_element
FEATURE [App::DocumentObjectGroupPython] I_element001  label="I_element : 1"  # scripted group (container) (typed FeaturePython)
  n = 1
  ref = I_element
FEATURE [App::DocumentObjectGroupPython] G4_CESIUM_IODIDE  # scripted group (container) (typed FeaturePython)
  Dunit = g/cm3
  Dvalue = 4.51
  Group = -> [Cs_element002,I_element001]
  conduct = 2
  density = 1
  expand = 3
  formula = G4_CESIUM_IODIDE
  name = G4_CESIUM_IODIDE
  specific = 4
FEATURE [App::DocumentObjectGroupPython] C_element028  label="C_element : 013"  # scripted group (container) (typed FeaturePython)
  n = 6
  ref = C_element
FEATURE [App::DocumentObjectGroupPython] H_element025  label="H_element : 013"  # scripted group (container) (typed FeaturePython)
  n = 5
  ref = H_element
FEATURE [App::DocumentObjectGroupPython] Cl_element005  label="Cl_element : 1"  # scripted group (container) (typed FeaturePython)
  n = 1
  ref = Cl_element
FEATURE [App::DocumentObjectGroupPython] G4_CHLOROBENZENE  # scripted group (container) (typed FeaturePython)
  Dunit = g/cm3
  Dvalue = 1.1058
  Group = -> [C_element028,H_element025,Cl_element005]
  conduct = 2
  density = 1
  expand = 3
  formula = G4_CHLOROBENZENE
  name = G4_CHLOROBENZENE
  specific = 4
FEATURE [App::DocumentObjectGroupPython] C_element029  label="C_element : 014"  # scripted group (container) (typed FeaturePython)
  n = 1
  ref = C_element
FEATURE [App::DocumentObjectGroupPython] H_element026  label="H_element : 1"  # scripted group (container) (typed FeaturePython)
  n = 1
  ref = H_element
FEATURE [App::DocumentObjectGroupPython] Cl_element006  label="Cl_element : 3"  # scripted group (container) (typed FeaturePython)
  n = 3
  ref = Cl_element
FEATURE [App::DocumentObjectGroupPython] G4_CHLOROFORM  # scripted group (container) (typed FeaturePython)
  Dunit = g/cm3
  Dvalue = 1.4832
  Group = -> [C_element029,H_element026,Cl_element006]
  conduct = 2
  density = 1
  expand = 3
  formula = G4_CHLOROFORM
  name = G4_CHLOROFORM
  specific = 4
FEATURE [App::DocumentObjectGroupPython] H_element027  label="H_element : 0.010"  # scripted group (container) (typed FeaturePython)
  n = 0.01
FEATURE [App::DocumentObjectGroupPython] C_element030  label="C_element : 0.001"  # scripted group (container) (typed FeaturePython)
  n = 0.001
FEATURE [App::DocumentObjectGroupPython] O_element030  label="O_element : 0.529"  # scripted group (container) (typed FeaturePython)
  n = 0.529107
FEATURE [App::DocumentObjectGroupPython] Na_element005  label="Na_element : 0.016"  # scripted group (container) (typed FeaturePython)
  n = 0.016
FEATURE [App::DocumentObjectGroupPython] Mg_element003  label="Mg_element : 0.004"  # scripted group (container) (typed FeaturePython)
  n = 0.002
FEATURE [App::DocumentObjectGroupPython] Al_element002  label="Al_element : 0.034"  # scripted group (container) (typed FeaturePython)
  n = 0.033872
FEATURE [App::DocumentObjectGroupPython] Si_element002  label="Si_element : 0.337"  # scripted group (container) (typed FeaturePython)
  n = 0.337021
FEATURE [App::DocumentObjectGroupPython] K_element003  label="K_element : 0.013"  # scripted group (container) (typed FeaturePython)
  n = 0.013
FEATURE [App::DocumentObjectGroupPython] Ca_element010  label="Ca_element : 0.044"  # scripted group (container) (typed FeaturePython)
  n = 0.044
FEATURE [App::DocumentObjectGroupPython] Fe_element002  label="Fe_element : 0.014"  # scripted group (container) (typed FeaturePython)
  n = 0.014
FEATURE [App::DocumentObjectGroupPython] G4_CONCRETE  # scripted group (container) (typed FeaturePython)
  Dunit = g/cm3
  Dvalue = 2.3
  Group = -> [H_element027,C_element030,O_element030,Na_element005,Mg_element003,Al_element002,Si_element002,K_element003,Ca_element010,Fe_element002]
  conduct = 2
  density = 1
  expand = 3
  formula = G4_CONCRETE
  name = G4_CONCRETE
  specific = 4
FEATURE [App::DocumentObjectGroupPython] C_element031  label="C_element : 015"  # scripted group (container) (typed FeaturePython)
  n = 6
  ref = C_element
FEATURE [App::DocumentObjectGroupPython] H_element028  label="H_element : 12"  # scripted group (container) (typed FeaturePython)
  n = 12
  ref = H_element
FEATURE [App::DocumentObjectGroupPython] G4_CYCLOHEXANE  # scripted group (container) (typed FeaturePython)
  Dunit = g/cm3
  Dvalue = 0.779
  Group = -> [C_element031,H_element028]
  conduct = 2
  density = 1
  expand = 3
  formula = G4_CYCLOHEXANE
  name = G4_CYCLOHEXANE
  specific = 4
FEATURE [App::DocumentObjectGroupPython] C_element032  label="C_element : 016"  # scripted group (container) (typed FeaturePython)
  n = 6
  ref = C_element
FEATURE [App::DocumentObjectGroupPython] H_element029  label="H_element : 4"  # scripted group (container) (typed FeaturePython)
  n = 4
  ref = H_element
FEATURE [App::DocumentObjectGroupPython] Cl_element007  label="Cl_element : 2"  # scripted group (container) (typed FeaturePython)
  n = 2
  ref = Cl_element
FEATURE [App::DocumentObjectGroupPython] G4_1_2_DICHLOROBENZENE  # scripted group (container) (typed FeaturePython)
  Dunit = g/cm3
  Dvalue = 1.3048
  Group = -> [C_element032,H_element029,Cl_element007]
  conduct = 2
  density = 1
  expand = 3
  formula = G4_1.2-DICHLOROBENZENE
  name = G4_1.2-DICHLOROBENZENE
  specific = 4
FEATURE [App::DocumentObjectGroupPython] C_element033  label="C_element : 017"  # scripted group (container) (typed FeaturePython)
  n = 4
  ref = C_element
FEATURE [App::DocumentObjectGroupPython] H_element030  label="H_element : 8"  # scripted group (container) (typed FeaturePython)
  n = 8
  ref = H_element
FEATURE [App::DocumentObjectGroupPython] O_element031  label="O_element : 014"  # scripted group (container) (typed FeaturePython)
  n = 1
  ref = O_element
FEATURE [App::DocumentObjectGroupPython] Cl_element008  label="Cl_element : 005"  # scripted group (container) (typed FeaturePython)
  n = 2
  ref = Cl_element
FEATURE [App::DocumentObjectGroupPython] G4_DICHLORODIETHYL_ETHER  # scripted group (container) (typed FeaturePython)
  Dunit = g/cm3
  Dvalue = 1.2199
  Group = -> [C_element033,H_element030,O_element031,Cl_element008]
  conduct = 2
  density = 1
  expand = 3
  formula = G4_DICHLORODIETHYL_ETHER
  name = G4_DICHLORODIETHYL_ETHER
  specific = 4
FEATURE [App::DocumentObjectGroupPython] C_element034  label="C_element : 018"  # scripted group (container) (typed FeaturePython)
  n = 2
  ref = C_element
FEATURE [App::DocumentObjectGroupPython] H_element031  label="H_element : 014"  # scripted group (container) (typed FeaturePython)
  n = 4
  ref = H_element
FEATURE [App::DocumentObjectGroupPython] Cl_element009  label="Cl_element : 006"  # scripted group (container) (typed FeaturePython)
  n = 2
  ref = Cl_element
FEATURE [App::DocumentObjectGroupPython] G4_1_2_DICHLOROETHANE  # scripted group (container) (typed FeaturePython)
  Dunit = g/cm3
  Dvalue = 1.2351
  Group = -> [C_element034,H_element031,Cl_element009]
  conduct = 2
  density = 1
  expand = 3
  formula = G4_1.2-DICHLOROETHANE
  name = G4_1.2-DICHLOROETHANE
  specific = 4
FEATURE [App::DocumentObjectGroupPython] C_element035  label="C_element : 019"  # scripted group (container) (typed FeaturePython)
  n = 4
  ref = C_element
FEATURE [App::DocumentObjectGroupPython] H_element032  label="H_element : 015"  # scripted group (container) (typed FeaturePython)
  n = 10
  ref = H_element
FEATURE [App::DocumentObjectGroupPython] O_element032  label="O_element : 015"  # scripted group (container) (typed FeaturePython)
  n = 1
  ref = O_element
FEATURE [App::DocumentObjectGroupPython] G4_DIETHYL_ETHER  # scripted group (container) (typed FeaturePython)
  Dunit = g/cm3
  Dvalue = 0.71378
  Group = -> [C_element035,H_element032,O_element032]
  conduct = 2
  density = 1
  expand = 3
  formula = G4_DIETHYL_ETHER
  name = G4_DIETHYL_ETHER
  specific = 4
FEATURE [App::DocumentObjectGroupPython] C_element036  label="C_element : 020"  # scripted group (container) (typed FeaturePython)
  n = 3
  ref = C_element
FEATURE [App::DocumentObjectGroupPython] H_element033  label="H_element : 016"  # scripted group (container) (typed FeaturePython)
  n = 7
  ref = H_element
FEATURE [App::DocumentObjectGroupPython] N_element015  label="N_element : 008"  # scripted group (container) (typed FeaturePython)
  n = 1
  ref = N_element
FEATURE [App::DocumentObjectGroupPython] O_element033  label="O_element : 016"  # scripted group (container) (typed FeaturePython)
  n = 1
  ref = O_element
FEATURE [App::DocumentObjectGroupPython] G4_N_N_DIMETHYL_FORMAMIDE  # scripted group (container) (typed FeaturePython)
  Dunit = g/cm3
  Dvalue = 0.9487
  Group = -> [C_element036,H_element033,N_element015,O_element033]
  conduct = 2
  density = 1
  expand = 3
  formula = G4_N.N-DIMETHYL_FORMAMIDE
  name = G4_N.N-DIMETHYL_FORMAMIDE
  specific = 4
FEATURE [App::DocumentObjectGroupPython] C_element037  label="C_element : 021"  # scripted group (container) (typed FeaturePython)
  n = 2
  ref = C_element
FEATURE [App::DocumentObjectGroupPython] H_element034  label="H_element : 017"  # scripted group (container) (typed FeaturePython)
  n = 6
  ref = H_element
FEATURE [App::DocumentObjectGroupPython] O_element034  label="O_element : 017"  # scripted group (container) (typed FeaturePython)
  n = 1
  ref = O_element
FEATURE [App::DocumentObjectGroupPython] S_element009  label="S_element : 003"  # scripted group (container) (typed FeaturePython)
  n = 1
  ref = S_element
FEATURE [App::DocumentObjectGroupPython] G4_DIMETHYL_SULFOXIDE  # scripted group (container) (typed FeaturePython)
  Dunit = g/cm3
  Dvalue = 1.1014
  Group = -> [C_element037,H_element034,O_element034,S_element009]
  conduct = 2
  density = 1
  expand = 3
  formula = G4_DIMETHYL_SULFOXIDE
  name = G4_DIMETHYL_SULFOXIDE
  specific = 4
FEATURE [App::DocumentObjectGroupPython] C_element038  label="C_element : 022"  # scripted group (container) (typed FeaturePython)
  n = 2
  ref = C_element
FEATURE [App::DocumentObjectGroupPython] H_element035  label="H_element : 018"  # scripted group (container) (typed FeaturePython)
  n = 6
  ref = H_element
FEATURE [App::DocumentObjectGroupPython] G4_ETHANE  # scripted group (container) (typed FeaturePython)
  Dunit = g/cm3
  Dvalue = 0.00125324
  Group = -> [C_element038,H_element035]
  conduct = 2
  density = 1
  expand = 3
  formula = G4_ETHANE
  name = G4_ETHANE
  specific = 4
FEATURE [App::DocumentObjectGroupPython] C_element039  label="C_element : 023"  # scripted group (container) (typed FeaturePython)
  n = 2
  ref = C_element
FEATURE [App::DocumentObjectGroupPython] H_element036  label="H_element : 019"  # scripted group (container) (typed FeaturePython)
  n = 6
  ref = H_element
FEATURE [App::DocumentObjectGroupPython] O_element035  label="O_element : 018"  # scripted group (container) (typed FeaturePython)
  n = 1
  ref = O_element
FEATURE [App::DocumentObjectGroupPython] G4_ETHYL_ALCOHOL  # scripted group (container) (typed FeaturePython)
  Dunit = g/cm3
  Dvalue = 0.7893
  Group = -> [C_element039,H_element036,O_element035]
  conduct = 2
  density = 1
  expand = 3
  formula = G4_ETHYL_ALCOHOL
  name = G4_ETHYL_ALCOHOL
  specific = 4
FEATURE [App::DocumentObjectGroupPython] H_element037  label="H_element : 0.090"  # scripted group (container) (typed FeaturePython)
  n = 0.090027
FEATURE [App::DocumentObjectGroupPython] C_element040  label="C_element : 0.585"  # scripted group (container) (typed FeaturePython)
  n = 0.585182
FEATURE [App::DocumentObjectGroupPython] O_element036  label="O_element : 0.325"  # scripted group (container) (typed FeaturePython)
  n = 0.324791
FEATURE [App::DocumentObjectGroupPython] G4_ETHYL_CELLULOSE  # scripted group (container) (typed FeaturePython)
  Dunit = g/cm3
  Dvalue = 1.13
  Group = -> [H_element037,C_element040,O_element036]
  conduct = 2
  density = 1
  expand = 3
  formula = G4_ETHYL_CELLULOSE
  name = G4_ETHYL_CELLULOSE
  specific = 4
FEATURE [App::DocumentObjectGroupPython] C_element041  label="C_element : 024"  # scripted group (container) (typed FeaturePython)
  n = 2
  ref = C_element
FEATURE [App::DocumentObjectGroupPython] H_element038  label="H_element : 020"  # scripted group (container) (typed FeaturePython)
  n = 4
  ref = H_element
FEATURE [App::DocumentObjectGroupPython] G4_ETHYLENE  # scripted group (container) (typed FeaturePython)
  Dunit = g/cm3
  Dvalue = 0.00117497
  Group = -> [C_element041,H_element038]
  conduct = 2
  density = 1
  expand = 3
  formula = G4_ETHYLENE
  name = G4_ETHYLENE
  specific = 4
FEATURE [App::DocumentObjectGroupPython] H_element039  label="H_element : 0.096"  # scripted group (container) (typed FeaturePython)
  n = 0.096
FEATURE [App::DocumentObjectGroupPython] C_element042  label="C_element : 0.195"  # scripted group (container) (typed FeaturePython)
  n = 0.195
FEATURE [App::DocumentObjectGroupPython] N_element016  label="N_element : 0.057"  # scripted group (container) (typed FeaturePython)
  n = 0.057
FEATURE [App::DocumentObjectGroupPython] O_element037  label="O_element : 0.646"  # scripted group (container) (typed FeaturePython)
  n = 0.646
FEATURE [App::DocumentObjectGroupPython] Na_element006  label="Na_element : 0.017"  # scripted group (container) (typed FeaturePython)
  n = 0.001
FEATURE [App::DocumentObjectGroupPython] P_element005  label="P_element : 0.104"  # scripted group (container) (typed FeaturePython)
  n = 0.001
FEATURE [App::DocumentObjectGroupPython] S_element010  label="S_element : 0.016"  # scripted group (container) (typed FeaturePython)
  n = 0.003
FEATURE [App::DocumentObjectGroupPython] Cl_element010  label="Cl_element : 0.005"  # scripted group (container) (typed FeaturePython)
  n = 0.001
FEATURE [App::DocumentObjectGroupPython] G4_EYE_LENS_ICRP  # scripted group (container) (typed FeaturePython)
  Dunit = g/cm3
  Dvalue = 1.07
  Group = -> [H_element039,C_element042,N_element016,O_element037,Na_element006,P_element005,S_element010,Cl_element010]
  conduct = 2
  density = 1
  expand = 3
  formula = G4_EYE_LENS_ICRP
  name = G4_EYE_LENS_ICRP
  specific = 4
FEATURE [App::DocumentObjectGroupPython] Fe_element003  label="Fe_element : 2"  # scripted group (container) (typed FeaturePython)
  n = 2
  ref = Fe_element
FEATURE [App::DocumentObjectGroupPython] O_element038  label="O_element : 019"  # scripted group (container) (typed FeaturePython)
  n = 3
  ref = O_element
FEATURE [App::DocumentObjectGroupPython] G4_FERRIC_OXIDE  # scripted group (container) (typed FeaturePython)
  Dunit = g/cm3
  Dvalue = 5.2
  Group = -> [Fe_element003,O_element038]
  conduct = 2
  density = 1
  expand = 3
  formula = G4_FERRIC_OXIDE
  name = G4_FERRIC_OXIDE
  specific = 4
FEATURE [App::DocumentObjectGroupPython] Fe_element004  label="Fe_element : 1"  # scripted group (container) (typed FeaturePython)
  n = 1
  ref = Fe_element
FEATURE [App::DocumentObjectGroupPython] B_element003  label="B_element : 1"  # scripted group (container) (typed FeaturePython)
  n = 1
  ref = B_element
FEATURE [App::DocumentObjectGroupPython] G4_FERROBORIDE  # scripted group (container) (typed FeaturePython)
  Dunit = g/cm3
  Dvalue = 7.15
  Group = -> [Fe_element004,B_element003]
  conduct = 2
  density = 1
  expand = 3
  formula = G4_FERROBORIDE
  name = G4_FERROBORIDE
  specific = 4
FEATURE [App::DocumentObjectGroupPython] Fe_element005  label="Fe_element : 003"  # scripted group (container) (typed FeaturePython)
  n = 1
  ref = Fe_element
FEATURE [App::DocumentObjectGroupPython] O_element039  label="O_element : 020"  # scripted group (container) (typed FeaturePython)
  n = 1
  ref = O_element
FEATURE [App::DocumentObjectGroupPython] G4_FERROUS_OXIDE  # scripted group (container) (typed FeaturePython)
  Dunit = g/cm3
  Dvalue = 5.7
  Group = -> [Fe_element005,O_element039]
  conduct = 2
  density = 1
  expand = 3
  formula = G4_FERROUS_OXIDE
  name = G4_FERROUS_OXIDE
  specific = 4
FEATURE [App::DocumentObjectGroupPython] H_element040  label="H_element : 0.115"  # scripted group (container) (typed FeaturePython)
  n = 0.108259
FEATURE [App::DocumentObjectGroupPython] N_element017  label="N_element : 0.000"  # scripted group (container) (typed FeaturePython)
  n = 2.7e-05
FEATURE [App::DocumentObjectGroupPython] O_element040  label="O_element : 0.879"  # scripted group (container) (typed FeaturePython)
  n = 0.878636
FEATURE [App::DocumentObjectGroupPython] Na_element007  label="Na_element : 0.000"  # scripted group (container) (typed FeaturePython)
  n = 2.2e-05
FEATURE [App::DocumentObjectGroupPython] S_element011  label="S_element : 0.013"  # scripted group (container) (typed FeaturePython)
  n = 0.012968
FEATURE [App::DocumentObjectGroupPython] Cl_element011  label="Cl_element : 0.000"  # scripted group (container) (typed FeaturePython)
  n = 3.4e-05
FEATURE [App::DocumentObjectGroupPython] Fe_element006  label="Fe_element : 0.000"  # scripted group (container) (typed FeaturePython)
  n = 5.4e-05
FEATURE [App::DocumentObjectGroupPython] G4_FERROUS_SULFATE  # scripted group (container) (typed FeaturePython)
  Dunit = g/cm3
  Dvalue = 1.024
  Group = -> [H_element040,N_element017,O_element040,Na_element007,S_element011,Cl_element011,Fe_element006]
  conduct = 2
  density = 1
  expand = 3
  formula = G4_FERROUS_SULFATE
  name = G4_FERROUS_SULFATE
  specific = 4
FEATURE [App::DocumentObjectGroupPython] C_element043  label="C_element : 0.099"  # scripted group (container) (typed FeaturePython)
  n = 0.099335
FEATURE [App::DocumentObjectGroupPython] F_element007  label="F_element : 0.314"  # scripted group (container) (typed FeaturePython)
  n = 0.314247
FEATURE [App::DocumentObjectGroupPython] Cl_element012  label="Cl_element : 0.586"  # scripted group (container) (typed FeaturePython)
  n = 0.586418
FEATURE [App::DocumentObjectGroupPython] G4_FREON_12  # scripted group (container) (typed FeaturePython)
  Dunit = g/cm3
  Dvalue = 1.12
  Group = -> [C_element043,F_element007,Cl_element012]
  conduct = 2
  density = 1
  expand = 3
  formula = G4_FREON-12
  name = G4_FREON-12
  specific = 4
FEATURE [App::DocumentObjectGroupPython] C_element044  label="C_element : 0.057"  # scripted group (container) (typed FeaturePython)
  n = 0.057245
FEATURE [App::DocumentObjectGroupPython] F_element008  label="F_element : 0.181"  # scripted group (container) (typed FeaturePython)
  n = 0.181096
FEATURE [App::DocumentObjectGroupPython] Br_element001  label="Br_element : 0.762"  # scripted group (container) (typed FeaturePython)
  n = 0.761659
FEATURE [App::DocumentObjectGroupPython] G4_FREON_12B2  # scripted group (container) (typed FeaturePython)
  Dunit = g/cm3
  Dvalue = 1.8
  Group = -> [C_element044,F_element008,Br_element001]
  conduct = 2
  density = 1
  expand = 3
  formula = G4_FREON-12B2
  name = G4_FREON-12B2
  specific = 4
FEATURE [App::DocumentObjectGroupPython] C_element045  label="C_element : 0.115"  # scripted group (container) (typed FeaturePython)
  n = 0.114983
FEATURE [App::DocumentObjectGroupPython] F_element009  label="F_element : 0.546"  # scripted group (container) (typed FeaturePython)
  n = 0.545621
FEATURE [App::DocumentObjectGroupPython] Cl_element013  label="Cl_element : 0.339"  # scripted group (container) (typed FeaturePython)
  n = 0.339396
FEATURE [App::DocumentObjectGroupPython] G4_FREON_13  # scripted group (container) (typed FeaturePython)
  Dunit = g/cm3
  Dvalue = 0.95
  Group = -> [C_element045,F_element009,Cl_element013]
  conduct = 2
  density = 1
  expand = 3
  formula = G4_FREON-13
  name = G4_FREON-13
  specific = 4
FEATURE [App::DocumentObjectGroupPython] C_element046  label="C_element : 025"  # scripted group (container) (typed FeaturePython)
  n = 1
  ref = C_element
FEATURE [App::DocumentObjectGroupPython] F_element010  label="F_element : 3"  # scripted group (container) (typed FeaturePython)
  n = 3
  ref = F_element
FEATURE [App::DocumentObjectGroupPython] Br_element002  label="Br_element : 1"  # scripted group (container) (typed FeaturePython)
  n = 1
  ref = Br_element
FEATURE [App::DocumentObjectGroupPython] G4_FREON_13B1  # scripted group (container) (typed FeaturePython)
  Dunit = g/cm3
  Dvalue = 1.5
  Group = -> [C_element046,F_element010,Br_element002]
  conduct = 2
  density = 1
  expand = 3
  formula = G4_FREON-13B1
  name = G4_FREON-13B1
  specific = 4
FEATURE [App::DocumentObjectGroupPython] C_element047  label="C_element : 0.061"  # scripted group (container) (typed FeaturePython)
  n = 0.061309
FEATURE [App::DocumentObjectGroupPython] F_element011  label="F_element : 0.291"  # scripted group (container) (typed FeaturePython)
  n = 0.290924
FEATURE [App::DocumentObjectGroupPython] I_element002  label="I_element : 0.648"  # scripted group (container) (typed FeaturePython)
  n = 0.647767
FEATURE [App::DocumentObjectGroupPython] G4_FREON_13I1  # scripted group (container) (typed FeaturePython)
  Dunit = g/cm3
  Dvalue = 1.8
  Group = -> [C_element047,F_element011,I_element002]
  conduct = 2
  density = 1
  expand = 3
  formula = G4_FREON-13I1
  name = G4_FREON-13I1
  specific = 4
FEATURE [App::DocumentObjectGroupPython] H_element041  label="H_element : 021"  # scripted group (container) (typed FeaturePython)
  n = 1
  ref = H_element
FEATURE [App::DocumentObjectGroupPython] G4_Galactic  # scripted group (container) (typed FeaturePython)
  Dunit = g/cm3
  Dvalue = 10
  Group = -> [H_element041]
  conduct = 2
  density = 1
  expand = 3
  formula = G4_Galactic
  name = G4_Galactic
  specific = 4
FEATURE [App::DocumentObjectGroupPython] Gd_element001  label="Gd_element : 2"  # scripted group (container) (typed FeaturePython)
  n = 2
  ref = Gd_element
FEATURE [App::DocumentObjectGroupPython] O_element041  label="O_element : 021"  # scripted group (container) (typed FeaturePython)
  n = 2
  ref = O_element
FEATURE [App::DocumentObjectGroupPython] S_element012  label="S_element : 004"  # scripted group (container) (typed FeaturePython)
  n = 1
  ref = S_element
FEATURE [App::DocumentObjectGroupPython] G4_GADOLINIUM_OXYSULFIDE  # scripted group (container) (typed FeaturePython)
  Dunit = g/cm3
  Dvalue = 7.44
  Group = -> [Gd_element001,O_element041,S_element012]
  conduct = 2
  density = 1
  expand = 3
  formula = G4_GADOLINIUM_OXYSULFIDE
  name = G4_GADOLINIUM_OXYSULFIDE
  specific = 4
FEATURE [App::DocumentObjectGroupPython] Ga_element001  label="Ga_element : 1"  # scripted group (container) (typed FeaturePython)
  n = 1
  ref = Ga_element
FEATURE [App::DocumentObjectGroupPython] As_element001  label="As_element : 1"  # scripted group (container) (typed FeaturePython)
  n = 1
  ref = As_element
FEATURE [App::DocumentObjectGroupPython] G4_GALLIUM_ARSENIDE  # scripted group (container) (typed FeaturePython)
  Dunit = g/cm3
  Dvalue = 5.31
  Group = -> [Ga_element001,As_element001]
  conduct = 2
  density = 1
  expand = 3
  formula = G4_GALLIUM_ARSENIDE
  name = G4_GALLIUM_ARSENIDE
  specific = 4
FEATURE [App::DocumentObjectGroupPython] H_element042  label="H_element : 0.081"  # scripted group (container) (typed FeaturePython)
  n = 0.08118
FEATURE [App::DocumentObjectGroupPython] C_element048  label="C_element : 0.416"  # scripted group (container) (typed FeaturePython)
  n = 0.41606
FEATURE [App::DocumentObjectGroupPython] N_element018  label="N_element : 0.111"  # scripted group (container) (typed FeaturePython)
  n = 0.11124
FEATURE [App::DocumentObjectGroupPython] O_element042  label="O_element : 0.381"  # scripted group (container) (typed FeaturePython)
  n = 0.38064
FEATURE [App::DocumentObjectGroupPython] S_element013  label="S_element : 0.011"  # scripted group (container) (typed FeaturePython)
  n = 0.01088
FEATURE [App::DocumentObjectGroupPython] G4_GEL_PHOTO_EMULSION  # scripted group (container) (typed FeaturePython)
  Dunit = g/cm3
  Dvalue = 1.2914
  Group = -> [H_element042,C_element048,N_element018,O_element042,S_element013]
  conduct = 2
  density = 1
  expand = 3
  formula = G4_GEL_PHOTO_EMULSION
  name = G4_GEL_PHOTO_EMULSION
  specific = 4
FEATURE [App::DocumentObjectGroupPython] B_element004  label="B_element : 0.040"  # scripted group (container) (typed FeaturePython)
  n = 0.0400639
FEATURE [App::DocumentObjectGroupPython] O_element043  label="O_element : 0.540"  # scripted group (container) (typed FeaturePython)
  n = 0.539561
FEATURE [App::DocumentObjectGroupPython] Na_element008  label="Na_element : 0.028"  # scripted group (container) (typed FeaturePython)
  n = 0.0281909
FEATURE [App::DocumentObjectGroupPython] Al_element003  label="Al_element : 0.012"  # scripted group (container) (typed FeaturePython)
  n = 0.011644
FEATURE [App::DocumentObjectGroupPython] Si_element003  label="Si_element : 0.377"  # scripted group (container) (typed FeaturePython)
  n = 0.377219
FEATURE [App::DocumentObjectGroupPython] K_element004  label="K_element : 0.014"  # scripted group (container) (typed FeaturePython)
  n = 0.00332099
FEATURE [App::DocumentObjectGroupPython] G4_Pyrex_Glass  # scripted group (container) (typed FeaturePython)
  Dunit = g/cm3
  Dvalue = 2.23
  Group = -> [B_element004,O_element043,Na_element008,Al_element003,Si_element003,K_element004]
  conduct = 2
  density = 1
  expand = 3
  formula = G4_Pyrex_Glass
  name = G4_Pyrex_Glass
  specific = 4
FEATURE [App::DocumentObjectGroupPython] O_element044  label="O_element : 0.156"  # scripted group (container) (typed FeaturePython)
  n = 0.156453
FEATURE [App::DocumentObjectGroupPython] Si_element004  label="Si_element : 0.081"  # scripted group (container) (typed FeaturePython)
  n = 0.080866
FEATURE [App::DocumentObjectGroupPython] Ti_element001  label="Ti_element : 0.008"  # scripted group (container) (typed FeaturePython)
  n = 0.008092
FEATURE [App::DocumentObjectGroupPython] As_element002  label="As_element : 0.003"  # scripted group (container) (typed FeaturePython)
  n = 0.002651
FEATURE [App::DocumentObjectGroupPython] Pb_element001  label="Pb_element : 0.752"  # scripted group (container) (typed FeaturePython)
  n = 0.751938
FEATURE [App::DocumentObjectGroupPython] G4_GLASS_LEAD  # scripted group (container) (typed FeaturePython)
  Dunit = g/cm3
  Dvalue = 6.22
  Group = -> [O_element044,Si_element004,Ti_element001,As_element002,Pb_element001]
  conduct = 2
  density = 1
  expand = 3
  formula = G4_GLASS_LEAD
  name = G4_GLASS_LEAD
  specific = 4
FEATURE [App::DocumentObjectGroupPython] O_element045  label="O_element : 0.460"  # scripted group (container) (typed FeaturePython)
  n = 0.4598
FEATURE [App::DocumentObjectGroupPython] Na_element009  label="Na_element : 0.096"  # scripted group (container) (typed FeaturePython)
  n = 0.0964411
FEATURE [App::DocumentObjectGroupPython] Si_element005  label="Si_element : 0.378"  # scripted group (container) (typed FeaturePython)
  n = 0.336553
FEATURE [App::DocumentObjectGroupPython] Ca_element011  label="Ca_element : 0.107"  # scripted group (container) (typed FeaturePython)
  n = 0.107205
FEATURE [App::DocumentObjectGroupPython] G4_GLASS_PLATE  # scripted group (container) (typed FeaturePython)
  Dunit = g/cm3
  Dvalue = 2.4
  Group = -> [O_element045,Na_element009,Si_element005,Ca_element011]
  conduct = 2
  density = 1
  expand = 3
  formula = G4_GLASS_PLATE
  name = G4_GLASS_PLATE
  specific = 4
FEATURE [App::DocumentObjectGroupPython] C_element049  label="C_element : 026"  # scripted group (container) (typed FeaturePython)
  n = 5
  ref = C_element
FEATURE [App::DocumentObjectGroupPython] H_element043  label="H_element : 022"  # scripted group (container) (typed FeaturePython)
  n = 10
  ref = H_element
FEATURE [App::DocumentObjectGroupPython] N_element019  label="N_element : 2"  # scripted group (container) (typed FeaturePython)
  n = 2
  ref = N_element
FEATURE [App::DocumentObjectGroupPython] O_element046  label="O_element : 022"  # scripted group (container) (typed FeaturePython)
  n = 3
  ref = O_element
FEATURE [App::DocumentObjectGroupPython] G4_GLUTAMINE  # scripted group (container) (typed FeaturePython)
  Dunit = g/cm3
  Dvalue = 1.46
  Group = -> [C_element049,H_element043,N_element019,O_element046]
  conduct = 2
  density = 1
  expand = 3
  formula = G4_GLUTAMINE
  name = G4_GLUTAMINE
  specific = 4
FEATURE [App::DocumentObjectGroupPython] C_element050  label="C_element : 027"  # scripted group (container) (typed FeaturePython)
  n = 3
  ref = C_element
FEATURE [App::DocumentObjectGroupPython] H_element044  label="H_element : 023"  # scripted group (container) (typed FeaturePython)
  n = 8
  ref = H_element
FEATURE [App::DocumentObjectGroupPython] O_element047  label="O_element : 023"  # scripted group (container) (typed FeaturePython)
  n = 3
  ref = O_element
FEATURE [App::DocumentObjectGroupPython] G4_GLYCEROL  # scripted group (container) (typed FeaturePython)
  Dunit = g/cm3
  Dvalue = 1.2613
  Group = -> [C_element050,H_element044,O_element047]
  conduct = 2
  density = 1
  expand = 3
  formula = G4_GLYCEROL
  name = G4_GLYCEROL
  specific = 4
FEATURE [App::DocumentObjectGroupPython] C_element051  label="C_element : 028"  # scripted group (container) (typed FeaturePython)
  n = 5
  ref = C_element
FEATURE [App::DocumentObjectGroupPython] H_element045  label="H_element : 024"  # scripted group (container) (typed FeaturePython)
  n = 5
  ref = H_element
FEATURE [App::DocumentObjectGroupPython] N_element020  label="N_element : 009"  # scripted group (container) (typed FeaturePython)
  n = 5
  ref = N_element
FEATURE [App::DocumentObjectGroupPython] O_element048  label="O_element : 024"  # scripted group (container) (typed FeaturePython)
  n = 1
  ref = O_element
FEATURE [App::DocumentObjectGroupPython] G4_GUANINE  # scripted group (container) (typed FeaturePython)
  Dunit = g/cm3
  Dvalue = 2.2
  Group = -> [C_element051,H_element045,N_element020,O_element048]
  conduct = 2
  density = 1
  expand = 3
  formula = G4_GUANINE
  name = G4_GUANINE
  specific = 4
FEATURE [App::DocumentObjectGroupPython] Ca_element012  label="Ca_element : 006"  # scripted group (container) (typed FeaturePython)
  n = 1
  ref = Ca_element
FEATURE [App::DocumentObjectGroupPython] S_element014  label="S_element : 005"  # scripted group (container) (typed FeaturePython)
  n = 1
  ref = S_element
FEATURE [App::DocumentObjectGroupPython] O_element049  label="O_element : 6"  # scripted group (container) (typed FeaturePython)
  n = 6
  ref = O_element
FEATURE [App::DocumentObjectGroupPython] H_element046  label="H_element : 025"  # scripted group (container) (typed FeaturePython)
  n = 4
  ref = H_element
FEATURE [App::DocumentObjectGroupPython] G4_GYPSUM  # scripted group (container) (typed FeaturePython)
  Dunit = g/cm3
  Dvalue = 2.32
  Group = -> [Ca_element012,S_element014,O_element049,H_element046]
  conduct = 2
  density = 1
  expand = 3
  formula = G4_GYPSUM
  name = G4_GYPSUM
  specific = 4
FEATURE [App::DocumentObjectGroupPython] C_element052  label="C_element : 7"  # scripted group (container) (typed FeaturePython)
  n = 7
  ref = C_element
FEATURE [App::DocumentObjectGroupPython] H_element047  label="H_element : 16"  # scripted group (container) (typed FeaturePython)
  n = 16
  ref = H_element
FEATURE [App::DocumentObjectGroupPython] G4_N_HEPTANE  # scripted group (container) (typed FeaturePython)
  Dunit = g/cm3
  Dvalue = 0.68376
  Group = -> [C_element052,H_element047]
  conduct = 2
  density = 1
  expand = 3
  formula = G4_N-HEPTANE
  name = G4_N-HEPTANE
  specific = 4
FEATURE [App::DocumentObjectGroupPython] C_element053  label="C_element : 029"  # scripted group (container) (typed FeaturePython)
  n = 6
  ref = C_element
FEATURE [App::DocumentObjectGroupPython] H_element048  label="H_element : 14"  # scripted group (container) (typed FeaturePython)
  n = 14
  ref = H_element
FEATURE [App::DocumentObjectGroupPython] G4_N_HEXANE  # scripted group (container) (typed FeaturePython)
  Dunit = g/cm3
  Dvalue = 0.6603
  Group = -> [C_element053,H_element048]
  conduct = 2
  density = 1
  expand = 3
  formula = G4_N-HEXANE
  name = G4_N-HEXANE
  specific = 4
FEATURE [App::DocumentObjectGroupPython] C_element054  label="C_element : 22"  # scripted group (container) (typed FeaturePython)
  n = 22
  ref = C_element
FEATURE [App::DocumentObjectGroupPython] H_element049  label="H_element : 026"  # scripted group (container) (typed FeaturePython)
  n = 10
  ref = H_element
FEATURE [App::DocumentObjectGroupPython] N_element021  label="N_element : 010"  # scripted group (container) (typed FeaturePython)
  n = 2
  ref = N_element
FEATURE [App::DocumentObjectGroupPython] O_element050  label="O_element : 025"  # scripted group (container) (typed FeaturePython)
  n = 5
  ref = O_element
FEATURE [App::DocumentObjectGroupPython] G4_KAPTON  # scripted group (container) (typed FeaturePython)
  Dunit = g/cm3
  Dvalue = 1.42
  Group = -> [C_element054,H_element049,N_element021,O_element050]
  conduct = 2
  density = 1
  expand = 3
  formula = G4_KAPTON
  name = G4_KAPTON
  specific = 4
FEATURE [App::DocumentObjectGroupPython] La_element001  label="La_element : 1"  # scripted group (container) (typed FeaturePython)
  n = 1
  ref = La_element
FEATURE [App::DocumentObjectGroupPython] Br_element003  label="Br_element : 002"  # scripted group (container) (typed FeaturePython)
  n = 1
  ref = Br_element
FEATURE [App::DocumentObjectGroupPython] O_element051  label="O_element : 026"  # scripted group (container) (typed FeaturePython)
  n = 1
  ref = O_element
FEATURE [App::DocumentObjectGroupPython] G4_LANTHANUM_OXYBROMIDE  # scripted group (container) (typed FeaturePython)
  Dunit = g/cm3
  Dvalue = 6.28
  Group = -> [La_element001,Br_element003,O_element051]
  conduct = 2
  density = 1
  expand = 3
  formula = G4_LANTHANUM_OXYBROMIDE
  name = G4_LANTHANUM_OXYBROMIDE
  specific = 4
FEATURE [App::DocumentObjectGroupPython] La_element002  label="La_element : 2"  # scripted group (container) (typed FeaturePython)
  n = 2
  ref = La_element
FEATURE [App::DocumentObjectGroupPython] O_element052  label="O_element : 027"  # scripted group (container) (typed FeaturePython)
  n = 2
  ref = O_element
FEATURE [App::DocumentObjectGroupPython] S_element015  label="S_element : 006"  # scripted group (container) (typed FeaturePython)
  n = 1
  ref = S_element
FEATURE [App::DocumentObjectGroupPython] G4_LANTHANUM_OXYSULFIDE  # scripted group (container) (typed FeaturePython)
  Dunit = g/cm3
  Dvalue = 5.86
  Group = -> [La_element002,O_element052,S_element015]
  conduct = 2
  density = 1
  expand = 3
  formula = G4_LANTHANUM_OXYSULFIDE
  name = G4_LANTHANUM_OXYSULFIDE
  specific = 4
FEATURE [App::DocumentObjectGroupPython] O_element053  label="O_element : 0.072"  # scripted group (container) (typed FeaturePython)
  n = 0.071682
FEATURE [App::DocumentObjectGroupPython] Pb_element002  label="Pb_element : 0.928"  # scripted group (container) (typed FeaturePython)
  n = 0.928318
FEATURE [App::DocumentObjectGroupPython] G4_LEAD_OXIDE  # scripted group (container) (typed FeaturePython)
  Dunit = g/cm3
  Dvalue = 9.53
  Group = -> [O_element053,Pb_element002]
  conduct = 2
  density = 1
  expand = 3
  formula = G4_LEAD_OXIDE
  name = G4_LEAD_OXIDE
  specific = 4
FEATURE [App::DocumentObjectGroupPython] Li_element001  label="Li_element : 1"  # scripted group (container) (typed FeaturePython)
  n = 1
  ref = Li_element
FEATURE [App::DocumentObjectGroupPython] N_element022  label="N_element : 011"  # scripted group (container) (typed FeaturePython)
  n = 1
  ref = N_element
FEATURE [App::DocumentObjectGroupPython] H_element050  label="H_element : 027"  # scripted group (container) (typed FeaturePython)
  n = 2
  ref = H_element
FEATURE [App::DocumentObjectGroupPython] G4_LITHIUM_AMIDE  # scripted group (container) (typed FeaturePython)
  Dunit = g/cm3
  Dvalue = 1.178
  Group = -> [Li_element001,N_element022,H_element050]
  conduct = 2
  density = 1
  expand = 3
  formula = G4_LITHIUM_AMIDE
  name = G4_LITHIUM_AMIDE
  specific = 4
FEATURE [App::DocumentObjectGroupPython] Li_element002  label="Li_element : 2"  # scripted group (container) (typed FeaturePython)
  n = 2
  ref = Li_element
FEATURE [App::DocumentObjectGroupPython] C_element055  label="C_element : 030"  # scripted group (container) (typed FeaturePython)
  n = 1
  ref = C_element
FEATURE [App::DocumentObjectGroupPython] O_element054  label="O_element : 028"  # scripted group (container) (typed FeaturePython)
  n = 3
  ref = O_element
FEATURE [App::DocumentObjectGroupPython] G4_LITHIUM_CARBONATE  # scripted group (container) (typed FeaturePython)
  Dunit = g/cm3
  Dvalue = 2.11
  Group = -> [Li_element002,C_element055,O_element054]
  conduct = 2
  density = 1
  expand = 3
  formula = G4_LITHIUM_CARBONATE
  name = G4_LITHIUM_CARBONATE
  specific = 4
FEATURE [App::DocumentObjectGroupPython] Li_element003  label="Li_element : 003"  # scripted group (container) (typed FeaturePython)
  n = 1
  ref = Li_element
FEATURE [App::DocumentObjectGroupPython] F_element012  label="F_element : 004"  # scripted group (container) (typed FeaturePython)
  n = 1
  ref = F_element
FEATURE [App::DocumentObjectGroupPython] G4_LITHIUM_FLUORIDE  # scripted group (container) (typed FeaturePython)
  Dunit = g/cm3
  Dvalue = 2.635
  Group = -> [Li_element003,F_element012]
  conduct = 2
  density = 1
  expand = 3
  formula = G4_LITHIUM_FLUORIDE
  name = G4_LITHIUM_FLUORIDE
  specific = 4
FEATURE [App::DocumentObjectGroupPython] Li_element004  label="Li_element : 004"  # scripted group (container) (typed FeaturePython)
  n = 1
  ref = Li_element
FEATURE [App::DocumentObjectGroupPython] H_element051  label="H_element : 028"  # scripted group (container) (typed FeaturePython)
  n = 1
  ref = H_element
FEATURE [App::DocumentObjectGroupPython] G4_LITHIUM_HYDRIDE  # scripted group (container) (typed FeaturePython)
  Dunit = g/cm3
  Dvalue = 0.82
  Group = -> [Li_element004,H_element051]
  conduct = 2
  density = 1
  expand = 3
  formula = G4_LITHIUM_HYDRIDE
  name = G4_LITHIUM_HYDRIDE
  specific = 4
FEATURE [App::DocumentObjectGroupPython] Li_element005  label="Li_element : 005"  # scripted group (container) (typed FeaturePython)
  n = 1
  ref = Li_element
FEATURE [App::DocumentObjectGroupPython] I_element003  label="I_element : 002"  # scripted group (container) (typed FeaturePython)
  n = 1
  ref = I_element
FEATURE [App::DocumentObjectGroupPython] G4_LITHIUM_IODIDE  # scripted group (container) (typed FeaturePython)
  Dunit = g/cm3
  Dvalue = 3.494
  Group = -> [Li_element005,I_element003]
  conduct = 2
  density = 1
  expand = 3
  formula = G4_LITHIUM_IODIDE
  name = G4_LITHIUM_IODIDE
  specific = 4
FEATURE [App::DocumentObjectGroupPython] Li_element006  label="Li_element : 006"  # scripted group (container) (typed FeaturePython)
  n = 2
  ref = Li_element
FEATURE [App::DocumentObjectGroupPython] O_element055  label="O_element : 029"  # scripted group (container) (typed FeaturePython)
  n = 1
  ref = O_element
FEATURE [App::DocumentObjectGroupPython] G4_LITHIUM_OXIDE  # scripted group (container) (typed FeaturePython)
  Dunit = g/cm3
  Dvalue = 2.013
  Group = -> [Li_element006,O_element055]
  conduct = 2
  density = 1
  expand = 3
  formula = G4_LITHIUM_OXIDE
  name = G4_LITHIUM_OXIDE
  specific = 4
FEATURE [App::DocumentObjectGroupPython] Li_element007  label="Li_element : 007"  # scripted group (container) (typed FeaturePython)
  n = 2
  ref = Li_element
FEATURE [App::DocumentObjectGroupPython] B_element005  label="B_element : 005"  # scripted group (container) (typed FeaturePython)
  n = 4
  ref = B_element
FEATURE [App::DocumentObjectGroupPython] O_element056  label="O_element : 7"  # scripted group (container) (typed FeaturePython)
  n = 7
  ref = O_element
FEATURE [App::DocumentObjectGroupPython] G4_LITHIUM_TETRABORATE  # scripted group (container) (typed FeaturePython)
  Dunit = g/cm3
  Dvalue = 2.44
  Group = -> [Li_element007,B_element005,O_element056]
  conduct = 2
  density = 1
  expand = 3
  formula = G4_LITHIUM_TETRABORATE
  name = G4_LITHIUM_TETRABORATE
  specific = 4
FEATURE [App::DocumentObjectGroupPython] H_element052  label="H_element : 0.105"  # scripted group (container) (typed FeaturePython)
  n = 0.105
FEATURE [App::DocumentObjectGroupPython] C_element056  label="C_element : 0.083"  # scripted group (container) (typed FeaturePython)
  n = 0.083
FEATURE [App::DocumentObjectGroupPython] N_element023  label="N_element : 0.023"  # scripted group (container) (typed FeaturePython)
  n = 0.023
FEATURE [App::DocumentObjectGroupPython] O_element057  label="O_element : 0.779"  # scripted group (container) (typed FeaturePython)
  n = 0.779
FEATURE [App::DocumentObjectGroupPython] Na_element010  label="Na_element : 0.097"  # scripted group (container) (typed FeaturePython)
  n = 0.002
FEATURE [App::DocumentObjectGroupPython] P_element006  label="P_element : 0.105"  # scripted group (container) (typed FeaturePython)
  n = 0.001
FEATURE [App::DocumentObjectGroupPython] S_element016  label="S_element : 0.017"  # scripted group (container) (typed FeaturePython)
  n = 0.002
FEATURE [App::DocumentObjectGroupPython] Cl_element014  label="Cl_element : 0.587"  # scripted group (container) (typed FeaturePython)
  n = 0.003
FEATURE [App::DocumentObjectGroupPython] K_element005  label="K_element : 0.015"  # scripted group (container) (typed FeaturePython)
  n = 0.002
FEATURE [App::DocumentObjectGroupPython] G4_LUNG_ICRP  # scripted group (container) (typed FeaturePython)
  Dunit = g/cm3
  Dvalue = 1.04
  Group = -> [H_element052,C_element056,N_element023,O_element057,Na_element010,P_element006,S_element016,Cl_element014,K_element005]
  conduct = 2
  density = 1
  expand = 3
  formula = G4_LUNG_ICRP
  name = G4_LUNG_ICRP
  specific = 4
FEATURE [App::DocumentObjectGroupPython] H_element053  label="H_element : 0.116"  # scripted group (container) (typed FeaturePython)
  n = 0.114318
FEATURE [App::DocumentObjectGroupPython] C_element057  label="C_element : 0.656"  # scripted group (container) (typed FeaturePython)
  n = 0.655824
FEATURE [App::DocumentObjectGroupPython] O_element058  label="O_element : 0.092"  # scripted group (container) (typed FeaturePython)
  n = 0.0921831
FEATURE [App::DocumentObjectGroupPython] Mg_element004  label="Mg_element : 0.135"  # scripted group (container) (typed FeaturePython)
  n = 0.134792
FEATURE [App::DocumentObjectGroupPython] Ca_element013  label="Ca_element : 0.003"  # scripted group (container) (typed FeaturePython)
  n = 0.002883
FEATURE [App::DocumentObjectGroupPython] G4_M3_WAX  # scripted group (container) (typed FeaturePython)
  Dunit = g/cm3
  Dvalue = 1.05
  Group = -> [H_element053,C_element057,O_element058,Mg_element004,Ca_element013]
  conduct = 2
  density = 1
  expand = 3
  formula = G4_M3_WAX
  name = G4_M3_WAX
  specific = 4
FEATURE [App::DocumentObjectGroupPython] Mg_element005  label="Mg_element : 1"  # scripted group (container) (typed FeaturePython)
  n = 1
  ref = Mg_element
FEATURE [App::DocumentObjectGroupPython] C_element058  label="C_element : 031"  # scripted group (container) (typed FeaturePython)
  n = 1
  ref = C_element
FEATURE [App::DocumentObjectGroupPython] O_element059  label="O_element : 030"  # scripted group (container) (typed FeaturePython)
  n = 3
  ref = O_element
FEATURE [App::DocumentObjectGroupPython] G4_MAGNESIUM_CARBONATE  # scripted group (container) (typed FeaturePython)
  Dunit = g/cm3
  Dvalue = 2.958
  Group = -> [Mg_element005,C_element058,O_element059]
  conduct = 2
  density = 1
  expand = 3
  formula = G4_MAGNESIUM_CARBONATE
  name = G4_MAGNESIUM_CARBONATE
  specific = 4
FEATURE [App::DocumentObjectGroupPython] Mg_element006  label="Mg_element : 002"  # scripted group (container) (typed FeaturePython)
  n = 1
  ref = Mg_element
FEATURE [App::DocumentObjectGroupPython] F_element013  label="F_element : 005"  # scripted group (container) (typed FeaturePython)
  n = 2
  ref = F_element
FEATURE [App::DocumentObjectGroupPython] G4_MAGNESIUM_FLUORIDE  # scripted group (container) (typed FeaturePython)
  Dunit = g/cm3
  Dvalue = 3
  Group = -> [Mg_element006,F_element013]
  conduct = 2
  density = 1
  expand = 3
  formula = G4_MAGNESIUM_FLUORIDE
  name = G4_MAGNESIUM_FLUORIDE
  specific = 4
FEATURE [App::DocumentObjectGroupPython] Mg_element007  label="Mg_element : 003"  # scripted group (container) (typed FeaturePython)
  n = 1
  ref = Mg_element
FEATURE [App::DocumentObjectGroupPython] O_element060  label="O_element : 031"  # scripted group (container) (typed FeaturePython)
  n = 1
  ref = O_element
FEATURE [App::DocumentObjectGroupPython] G4_MAGNESIUM_OXIDE  # scripted group (container) (typed FeaturePython)
  Dunit = g/cm3
  Dvalue = 3.58
  Group = -> [Mg_element007,O_element060]
  conduct = 2
  density = 1
  expand = 3
  formula = G4_MAGNESIUM_OXIDE
  name = G4_MAGNESIUM_OXIDE
  specific = 4
FEATURE [App::DocumentObjectGroupPython] Mg_element008  label="Mg_element : 004"  # scripted group (container) (typed FeaturePython)
  n = 1
  ref = Mg_element
FEATURE [App::DocumentObjectGroupPython] B_element006  label="B_element : 006"  # scripted group (container) (typed FeaturePython)
  n = 4
  ref = B_element
FEATURE [App::DocumentObjectGroupPython] O_element061  label="O_element : 032"  # scripted group (container) (typed FeaturePython)
  n = 7
  ref = O_element
FEATURE [App::DocumentObjectGroupPython] G4_MAGNESIUM_TETRABORATE  # scripted group (container) (typed FeaturePython)
  Dunit = g/cm3
  Dvalue = 2.53
  Group = -> [Mg_element008,B_element006,O_element061]
  conduct = 2
  density = 1
  expand = 3
  formula = G4_MAGNESIUM_TETRABORATE
  name = G4_MAGNESIUM_TETRABORATE
  specific = 4
FEATURE [App::DocumentObjectGroupPython] Hg_element001  label="Hg_element : 1"  # scripted group (container) (typed FeaturePython)
  n = 1
  ref = Hg_element
FEATURE [App::DocumentObjectGroupPython] I_element004  label="I_element : 2"  # scripted group (container) (typed FeaturePython)
  n = 2
  ref = I_element
FEATURE [App::DocumentObjectGroupPython] G4_MERCURIC_IODIDE  # scripted group (container) (typed FeaturePython)
  Dunit = g/cm3
  Dvalue = 6.36
  Group = -> [Hg_element001,I_element004]
  conduct = 2
  density = 1
  expand = 3
  formula = G4_MERCURIC_IODIDE
  name = G4_MERCURIC_IODIDE
  specific = 4
FEATURE [App::DocumentObjectGroupPython] C_element059  label="C_element : 032"  # scripted group (container) (typed FeaturePython)
  n = 1
  ref = C_element
FEATURE [App::DocumentObjectGroupPython] H_element054  label="H_element : 029"  # scripted group (container) (typed FeaturePython)
  n = 4
  ref = H_element
FEATURE [App::DocumentObjectGroupPython] G4_METHANE  # scripted group (container) (typed FeaturePython)
  Dunit = g/cm3
  Dvalue = 0.000667151
  Group = -> [C_element059,H_element054]
  conduct = 2
  density = 1
  expand = 3
  formula = G4_METHANE
  name = G4_METHANE
  specific = 4
FEATURE [App::DocumentObjectGroupPython] C_element060  label="C_element : 033"  # scripted group (container) (typed FeaturePython)
  n = 1
  ref = C_element
FEATURE [App::DocumentObjectGroupPython] H_element055  label="H_element : 030"  # scripted group (container) (typed FeaturePython)
  n = 4
  ref = H_element
FEATURE [App::DocumentObjectGroupPython] O_element062  label="O_element : 033"  # scripted group (container) (typed FeaturePython)
  n = 1
  ref = O_element
FEATURE [App::DocumentObjectGroupPython] G4_METHANOL  # scripted group (container) (typed FeaturePython)
  Dunit = g/cm3
  Dvalue = 0.7914
  Group = -> [C_element060,H_element055,O_element062]
  conduct = 2
  density = 1
  expand = 3
  formula = G4_METHANOL
  name = G4_METHANOL
  specific = 4
FEATURE [App::DocumentObjectGroupPython] H_element056  label="H_element : 0.134"  # scripted group (container) (typed FeaturePython)
  n = 0.13404
FEATURE [App::DocumentObjectGroupPython] C_element061  label="C_element : 0.778"  # scripted group (container) (typed FeaturePython)
  n = 0.77796
FEATURE [App::DocumentObjectGroupPython] O_element063  label="O_element : 0.035"  # scripted group (container) (typed FeaturePython)
  n = 0.03502
FEATURE [App::DocumentObjectGroupPython] Mg_element009  label="Mg_element : 0.039"  # scripted group (container) (typed FeaturePython)
  n = 0.038594
FEATURE [App::DocumentObjectGroupPython] Ti_element002  label="Ti_element : 0.014"  # scripted group (container) (typed FeaturePython)
  n = 0.014386
FEATURE [App::DocumentObjectGroupPython] G4_MIX_D_WAX  # scripted group (container) (typed FeaturePython)
  Dunit = g/cm3
  Dvalue = 0.99
  Group = -> [H_element056,C_element061,O_element063,Mg_element009,Ti_element002]
  conduct = 2
  density = 1
  expand = 3
  formula = G4_MIX_D_WAX
  name = G4_MIX_D_WAX
  specific = 4
FEATURE [App::DocumentObjectGroupPython] H_element057  label="H_element : 0.135"  # scripted group (container) (typed FeaturePython)
  n = 0.081192
FEATURE [App::DocumentObjectGroupPython] C_element062  label="C_element : 0.583"  # scripted group (container) (typed FeaturePython)
  n = 0.583442
FEATURE [App::DocumentObjectGroupPython] N_element024  label="N_element : 0.018"  # scripted group (container) (typed FeaturePython)
  n = 0.017798
FEATURE [App::DocumentObjectGroupPython] O_element064  label="O_element : 0.186"  # scripted group (container) (typed FeaturePython)
  n = 0.186381
FEATURE [App::DocumentObjectGroupPython] Mg_element010  label="Mg_element : 0.130"  # scripted group (container) (typed FeaturePython)
  n = 0.130287
FEATURE [App::DocumentObjectGroupPython] Cl_element015  label="Cl_element : 0.588"  # scripted group (container) (typed FeaturePython)
  n = 0.0009
FEATURE [App::DocumentObjectGroupPython] G4_MS20_TISSUE  # scripted group (container) (typed FeaturePython)
  Dunit = g/cm3
  Dvalue = 1
  Group = -> [H_element057,C_element062,N_element024,O_element064,Mg_element010,Cl_element015]
  conduct = 2
  density = 1
  expand = 3
  formula = G4_MS20_TISSUE
  name = G4_MS20_TISSUE
  specific = 4
FEATURE [App::DocumentObjectGroupPython] H_element058  label="H_element : 0.136"  # scripted group (container) (typed FeaturePython)
  n = 0.102
FEATURE [App::DocumentObjectGroupPython] C_element063  label="C_element : 0.143"  # scripted group (container) (typed FeaturePython)
  n = 0.143
FEATURE [App::DocumentObjectGroupPython] N_element025  label="N_element : 0.034"  # scripted group (container) (typed FeaturePython)
  n = 0.034
FEATURE [App::DocumentObjectGroupPython] O_element065  label="O_element : 0.710"  # scripted group (container) (typed FeaturePython)
  n = 0.71
FEATURE [App::DocumentObjectGroupPython] Na_element011  label="Na_element : 0.098"  # scripted group (container) (typed FeaturePython)
  n = 0.001
FEATURE [App::DocumentObjectGroupPython] P_element007  label="P_element : 0.002"  # scripted group (container) (typed FeaturePython)
  n = 0.002
FEATURE [App::DocumentObjectGroupPython] S_element017  label="S_element : 0.018"  # scripted group (container) (typed FeaturePython)
  n = 0.003
FEATURE [App::DocumentObjectGroupPython] Cl_element016  label="Cl_element : 0.589"  # scripted group (container) (typed FeaturePython)
  n = 0.001
FEATURE [App::DocumentObjectGroupPython] K_element006  label="K_element : 0.004"  # scripted group (container) (typed FeaturePython)
  n = 0.004
FEATURE [App::DocumentObjectGroupPython] G4_MUSCLE_SKELETAL_ICRP  # scripted group (container) (typed FeaturePython)
  Dunit = g/cm3
  Dvalue = 1.05
  Group = -> [H_element058,C_element063,N_element025,O_element065,Na_element011,P_element007,S_element017,Cl_element016,K_element006]
  conduct = 2
  density = 1
  expand = 3
  formula = G4_MUSCLE_SKELETAL_ICRP
  name = G4_MUSCLE_SKELETAL_ICRP
  specific = 4
FEATURE [App::DocumentObjectGroupPython] H_element059  label="H_element : 0.137"  # scripted group (container) (typed FeaturePython)
  n = 0.102102
FEATURE [App::DocumentObjectGroupPython] C_element064  label="C_element : 0.123"  # scripted group (container) (typed FeaturePython)
  n = 0.123123
FEATURE [App::DocumentObjectGroupPython] N_element026  label="N_element : 0.756"  # scripted group (container) (typed FeaturePython)
  n = 0.035035
FEATURE [App::DocumentObjectGroupPython] O_element066  label="O_element : 0.730"  # scripted group (container) (typed FeaturePython)
  n = 0.72973
FEATURE [App::DocumentObjectGroupPython] Na_element012  label="Na_element : 0.099"  # scripted group (container) (typed FeaturePython)
  n = 0.001001
FEATURE [App::DocumentObjectGroupPython] P_element008  label="P_element : 0.106"  # scripted group (container) (typed FeaturePython)
  n = 0.002002
FEATURE [App::DocumentObjectGroupPython] S_element018  label="S_element : 0.019"  # scripted group (container) (typed FeaturePython)
  n = 0.004004
FEATURE [App::DocumentObjectGroupPython] K_element007  label="K_element : 0.016"  # scripted group (container) (typed FeaturePython)
  n = 0.003003
FEATURE [App::DocumentObjectGroupPython] G4_MUSCLE_STRIATED_ICRU  # scripted group (container) (typed FeaturePython)
  Dunit = g/cm3
  Dvalue = 1.04
  Group = -> [H_element059,C_element064,N_element026,O_element066,Na_element012,P_element008,S_element018,K_element007]
  conduct = 2
  density = 1
  expand = 3
  formula = G4_MUSCLE_STRIATED_ICRU
  name = G4_MUSCLE_STRIATED_ICRU
  specific = 4
FEATURE [App::DocumentObjectGroupPython] H_element060  label="H_element : 0.098"  # scripted group (container) (typed FeaturePython)
  n = 0.0982341
FEATURE [App::DocumentObjectGroupPython] C_element065  label="C_element : 0.156"  # scripted group (container) (typed FeaturePython)
  n = 0.156214
FEATURE [App::DocumentObjectGroupPython] N_element027  label="N_element : 0.757"  # scripted group (container) (typed FeaturePython)
  n = 0.035451
FEATURE [App::DocumentObjectGroupPython] O_element067  label="O_element : 0.880"  # scripted group (container) (typed FeaturePython)
  n = 0.710101
FEATURE [App::DocumentObjectGroupPython] G4_MUSCLE_WITH_SUCROSE  # scripted group (container) (typed FeaturePython)
  Dunit = g/cm3
  Dvalue = 1.11
  Group = -> [H_element060,C_element065,N_element027,O_element067]
  conduct = 2
  density = 1
  expand = 3
  formula = G4_MUSCLE_WITH_SUCROSE
  name = G4_MUSCLE_WITH_SUCROSE
  specific = 4
FEATURE [App::DocumentObjectGroupPython] H_element061  label="H_element : 0.138"  # scripted group (container) (typed FeaturePython)
  n = 0.101969
FEATURE [App::DocumentObjectGroupPython] C_element066  label="C_element : 0.120"  # scripted group (container) (typed FeaturePython)
  n = 0.120058
FEATURE [App::DocumentObjectGroupPython] N_element028  label="N_element : 0.758"  # scripted group (container) (typed FeaturePython)
  n = 0.035451
FEATURE [App::DocumentObjectGroupPython] O_element068  label="O_element : 0.743"  # scripted group (container) (typed FeaturePython)
  n = 0.742522
FEATURE [App::DocumentObjectGroupPython] G4_MUSCLE_WITHOUT_SUCROSE  # scripted group (container) (typed FeaturePython)
  Dunit = g/cm3
  Dvalue = 1.07
  Group = -> [H_element061,C_element066,N_element028,O_element068]
  conduct = 2
  density = 1
  expand = 3
  formula = G4_MUSCLE_WITHOUT_SUCROSE
  name = G4_MUSCLE_WITHOUT_SUCROSE
  specific = 4
FEATURE [App::DocumentObjectGroupPython] C_element067  label="C_element : 10"  # scripted group (container) (typed FeaturePython)
  n = 10
  ref = C_element
FEATURE [App::DocumentObjectGroupPython] H_element062  label="H_element : 031"  # scripted group (container) (typed FeaturePython)
  n = 8
  ref = H_element
FEATURE [App::DocumentObjectGroupPython] G4_NAPHTHALENE  # scripted group (container) (typed FeaturePython)
  Dunit = g/cm3
  Dvalue = 1.145
  Group = -> [C_element067,H_element062]
  conduct = 2
  density = 1
  expand = 3
  formula = G4_NAPHTHALENE
  name = G4_NAPHTHALENE
  specific = 4
FEATURE [App::DocumentObjectGroupPython] C_element068  label="C_element : 034"  # scripted group (container) (typed FeaturePython)
  n = 6
  ref = C_element
FEATURE [App::DocumentObjectGroupPython] H_element063  label="H_element : 032"  # scripted group (container) (typed FeaturePython)
  n = 5
  ref = H_element
FEATURE [App::DocumentObjectGroupPython] N_element029  label="N_element : 012"  # scripted group (container) (typed FeaturePython)
  n = 1
  ref = N_element
FEATURE [App::DocumentObjectGroupPython] O_element069  label="O_element : 034"  # scripted group (container) (typed FeaturePython)
  n = 2
  ref = O_element
FEATURE [App::DocumentObjectGroupPython] G4_NITROBENZENE  # scripted group (container) (typed FeaturePython)
  Dunit = g/cm3
  Dvalue = 1.19867
  Group = -> [C_element068,H_element063,N_element029,O_element069]
  conduct = 2
  density = 1
  expand = 3
  formula = G4_NITROBENZENE
  name = G4_NITROBENZENE
  specific = 4
FEATURE [App::DocumentObjectGroupPython] N_element030  label="N_element : 013"  # scripted group (container) (typed FeaturePython)
  n = 2
  ref = N_element
FEATURE [App::DocumentObjectGroupPython] O_element070  label="O_element : 035"  # scripted group (container) (typed FeaturePython)
  n = 1
  ref = O_element
FEATURE [App::DocumentObjectGroupPython] G4_NITROUS_OXIDE  # scripted group (container) (typed FeaturePython)
  Dunit = g/cm3
  Dvalue = 0.00183094
  Group = -> [N_element030,O_element070]
  conduct = 2
  density = 1
  expand = 3
  formula = G4_NITROUS_OXIDE
  name = G4_NITROUS_OXIDE
  specific = 4
FEATURE [App::DocumentObjectGroupPython] H_element064  label="H_element : 0.104"  # scripted group (container) (typed FeaturePython)
  n = 0.103509
FEATURE [App::DocumentObjectGroupPython] C_element069  label="C_element : 0.648"  # scripted group (container) (typed FeaturePython)
  n = 0.648416
FEATURE [App::DocumentObjectGroupPython] N_element031  label="N_element : 0.100"  # scripted group (container) (typed FeaturePython)
  n = 0.0995361
FEATURE [App::DocumentObjectGroupPython] O_element071  label="O_element : 0.149"  # scripted group (container) (typed FeaturePython)
  n = 0.148539
FEATURE [App::DocumentObjectGroupPython] G4_NYLON_8062  # scripted group (container) (typed FeaturePython)
  Dunit = g/cm3
  Dvalue = 1.08
  Group = -> [H_element064,C_element069,N_element031,O_element071]
  conduct = 2
  density = 1
  expand = 3
  formula = G4_NYLON-8062
  name = G4_NYLON-8062
  specific = 4
FEATURE [App::DocumentObjectGroupPython] C_element070  label="C_element : 035"  # scripted group (container) (typed FeaturePython)
  n = 6
  ref = C_element
FEATURE [App::DocumentObjectGroupPython] H_element065  label="H_element : 11"  # scripted group (container) (typed FeaturePython)
  n = 11
  ref = H_element
FEATURE [App::DocumentObjectGroupPython] N_element032  label="N_element : 014"  # scripted group (container) (typed FeaturePython)
  n = 1
  ref = N_element
FEATURE [App::DocumentObjectGroupPython] O_element072  label="O_element : 036"  # scripted group (container) (typed FeaturePython)
  n = 1
  ref = O_element
FEATURE [App::DocumentObjectGroupPython] G4_NYLON_6_6  # scripted group (container) (typed FeaturePython)
  Dunit = g/cm3
  Dvalue = 1.14
  Group = -> [C_element070,H_element065,N_element032,O_element072]
  conduct = 2
  density = 1
  expand = 3
  formula = G4_NYLON-6-6
  name = G4_NYLON-6-6
  specific = 4
FEATURE [App::DocumentObjectGroupPython] H_element066  label="H_element : 0.139"  # scripted group (container) (typed FeaturePython)
  n = 0.107062
FEATURE [App::DocumentObjectGroupPython] C_element071  label="C_element : 0.680"  # scripted group (container) (typed FeaturePython)
  n = 0.680449
FEATURE [App::DocumentObjectGroupPython] N_element033  label="N_element : 0.099"  # scripted group (container) (typed FeaturePython)
  n = 0.099189
FEATURE [App::DocumentObjectGroupPython] O_element073  label="O_element : 0.113"  # scripted group (container) (typed FeaturePython)
  n = 0.1133
FEATURE [App::DocumentObjectGroupPython] G4_NYLON_6_10  # scripted group (container) (typed FeaturePython)
  Dunit = g/cm3
  Dvalue = 1.14
  Group = -> [H_element066,C_element071,N_element033,O_element073]
  conduct = 2
  density = 1
  expand = 3
  formula = G4_NYLON-6-10
  name = G4_NYLON-6-10
  specific = 4
FEATURE [App::DocumentObjectGroupPython] H_element067  label="H_element : 0.140"  # scripted group (container) (typed FeaturePython)
  n = 0.115476
FEATURE [App::DocumentObjectGroupPython] C_element072  label="C_element : 0.721"  # scripted group (container) (typed FeaturePython)
  n = 0.720818
FEATURE [App::DocumentObjectGroupPython] N_element034  label="N_element : 0.076"  # scripted group (container) (typed FeaturePython)
  n = 0.0764169
FEATURE [App::DocumentObjectGroupPython] O_element074  label="O_element : 0.087"  # scripted group (container) (typed FeaturePython)
  n = 0.0872889
FEATURE [App::DocumentObjectGroupPython] G4_NYLON_11_RILSAN  # scripted group (container) (typed FeaturePython)
  Dunit = g/cm3
  Dvalue = 1.425
  Group = -> [H_element067,C_element072,N_element034,O_element074]
  conduct = 2
  density = 1
  expand = 3
  formula = G4_NYLON-11_RILSAN
  name = G4_NYLON-11_RILSAN
  specific = 4
FEATURE [App::DocumentObjectGroupPython] C_element073  label="C_element : 8"  # scripted group (container) (typed FeaturePython)
  n = 8
  ref = C_element
FEATURE [App::DocumentObjectGroupPython] H_element068  label="H_element : 18"  # scripted group (container) (typed FeaturePython)
  n = 18
  ref = H_element
FEATURE [App::DocumentObjectGroupPython] G4_OCTANE  # scripted group (container) (typed FeaturePython)
  Dunit = g/cm3
  Dvalue = 0.7026
  Group = -> [C_element073,H_element068]
  conduct = 2
  density = 1
  expand = 3
  formula = G4_OCTANE
  name = G4_OCTANE
  specific = 4
FEATURE [App::DocumentObjectGroupPython] C_element074  label="C_element : 25"  # scripted group (container) (typed FeaturePython)
  n = 25
  ref = C_element
FEATURE [App::DocumentObjectGroupPython] H_element069  label="H_element : 52"  # scripted group (container) (typed FeaturePython)
  n = 52
  ref = H_element
FEATURE [App::DocumentObjectGroupPython] G4_PARAFFIN  # scripted group (container) (typed FeaturePython)
  Dunit = g/cm3
  Dvalue = 0.93
  Group = -> [C_element074,H_element069]
  conduct = 2
  density = 1
  expand = 3
  formula = G4_PARAFFIN
  name = G4_PARAFFIN
  specific = 4
FEATURE [App::DocumentObjectGroupPython] C_element075  label="C_element : 036"  # scripted group (container) (typed FeaturePython)
  n = 5
  ref = C_element
FEATURE [App::DocumentObjectGroupPython] H_element070  label="H_element : 033"  # scripted group (container) (typed FeaturePython)
  n = 12
  ref = H_element
FEATURE [App::DocumentObjectGroupPython] G4_N_PENTANE  # scripted group (container) (typed FeaturePython)
  Dunit = g/cm3
  Dvalue = 0.6262
  Group = -> [C_element075,H_element070]
  conduct = 2
  density = 1
  expand = 3
  formula = G4_N-PENTANE
  name = G4_N-PENTANE
  specific = 4
FEATURE [App::DocumentObjectGroupPython] H_element071  label="H_element : 0.014"  # scripted group (container) (typed FeaturePython)
  n = 0.0141
FEATURE [App::DocumentObjectGroupPython] C_element076  label="C_element : 0.072"  # scripted group (container) (typed FeaturePython)
  n = 0.072261
FEATURE [App::DocumentObjectGroupPython] N_element035  label="N_element : 0.019"  # scripted group (container) (typed FeaturePython)
  n = 0.01932
FEATURE [App::DocumentObjectGroupPython] O_element075  label="O_element : 0.066"  # scripted group (container) (typed FeaturePython)
  n = 0.066101
FEATURE [App::DocumentObjectGroupPython] S_element019  label="S_element : 0.020"  # scripted group (container) (typed FeaturePython)
  n = 0.00189
FEATURE [App::DocumentObjectGroupPython] Br_element004  label="Br_element : 0.349"  # scripted group (container) (typed FeaturePython)
  n = 0.349103
FEATURE [App::DocumentObjectGroupPython] Ag_element001  label="Ag_element : 0.474"  # scripted group (container) (typed FeaturePython)
  n = 0.474105
FEATURE [App::DocumentObjectGroupPython] I_element005  label="I_element : 0.003"  # scripted group (container) (typed FeaturePython)
  n = 0.00312
FEATURE [App::DocumentObjectGroupPython] G4_PHOTO_EMULSION  # scripted group (container) (typed FeaturePython)
  Dunit = g/cm3
  Dvalue = 3.815
  Group = -> [H_element071,C_element076,N_element035,O_element075,S_element019,Br_element004,Ag_element001,I_element005]
  conduct = 2
  density = 1
  expand = 3
  formula = G4_PHOTO_EMULSION
  name = G4_PHOTO_EMULSION
  specific = 4
FEATURE [App::DocumentObjectGroupPython] C_element077  label="C_element : 9"  # scripted group (container) (typed FeaturePython)
  n = 9
  ref = C_element
FEATURE [App::DocumentObjectGroupPython] H_element072  label="H_element : 034"  # scripted group (container) (typed FeaturePython)
  n = 10
  ref = H_element
FEATURE [App::DocumentObjectGroupPython] G4_PLASTIC_SC_VINYLTOLUENE  # scripted group (container) (typed FeaturePython)
  Dunit = g/cm3
  Dvalue = 1.032
  Group = -> [C_element077,H_element072]
  conduct = 2
  density = 1
  expand = 3
  formula = G4_PLASTIC_SC_VINYLTOLUENE
  name = G4_PLASTIC_SC_VINYLTOLUENE
  specific = 4
FEATURE [App::DocumentObjectGroupPython] Pu_element001  label="Pu_element : 1"  # scripted group (container) (typed FeaturePython)
  n = 1
  ref = Pu_element
FEATURE [App::DocumentObjectGroupPython] O_element076  label="O_element : 037"  # scripted group (container) (typed FeaturePython)
  n = 2
  ref = O_element
FEATURE [App::DocumentObjectGroupPython] G4_PLUTONIUM_DIOXIDE  # scripted group (container) (typed FeaturePython)
  Dunit = g/cm3
  Dvalue = 11.46
  Group = -> [Pu_element001,O_element076]
  conduct = 2
  density = 1
  expand = 3
  formula = G4_PLUTONIUM_DIOXIDE
  name = G4_PLUTONIUM_DIOXIDE
  specific = 4
FEATURE [App::DocumentObjectGroupPython] C_element078  label="C_element : 037"  # scripted group (container) (typed FeaturePython)
  n = 3
  ref = C_element
FEATURE [App::DocumentObjectGroupPython] H_element073  label="H_element : 035"  # scripted group (container) (typed FeaturePython)
  n = 3
  ref = H_element
FEATURE [App::DocumentObjectGroupPython] N_element036  label="N_element : 015"  # scripted group (container) (typed FeaturePython)
  n = 1
  ref = N_element
FEATURE [App::DocumentObjectGroupPython] G4_POLYACRYLONITRILE  # scripted group (container) (typed FeaturePython)
  Dunit = g/cm3
  Dvalue = 1.17
  Group = -> [C_element078,H_element073,N_element036]
  conduct = 2
  density = 1
  expand = 3
  formula = G4_POLYACRYLONITRILE
  name = G4_POLYACRYLONITRILE
  specific = 4
FEATURE [App::DocumentObjectGroupPython] C_element079  label="C_element : 16"  # scripted group (container) (typed FeaturePython)
  n = 16
  ref = C_element
FEATURE [App::DocumentObjectGroupPython] H_element074  label="H_element : 036"  # scripted group (container) (typed FeaturePython)
  n = 14
  ref = H_element
FEATURE [App::DocumentObjectGroupPython] O_element077  label="O_element : 038"  # scripted group (container) (typed FeaturePython)
  n = 3
  ref = O_element
FEATURE [App::DocumentObjectGroupPython] G4_POLYCARBONATE  # scripted group (container) (typed FeaturePython)
  Dunit = g/cm3
  Dvalue = 1.2
  Group = -> [C_element079,H_element074,O_element077]
  conduct = 2
  density = 1
  expand = 3
  formula = G4_POLYCARBONATE
  name = G4_POLYCARBONATE
  specific = 4
FEATURE [App::DocumentObjectGroupPython] C_element080  label="C_element : 038"  # scripted group (container) (typed FeaturePython)
  n = 8
  ref = C_element
FEATURE [App::DocumentObjectGroupPython] H_element075  label="H_element : 037"  # scripted group (container) (typed FeaturePython)
  n = 7
  ref = H_element
FEATURE [App::DocumentObjectGroupPython] Cl_element017  label="Cl_element : 007"  # scripted group (container) (typed FeaturePython)
  n = 1
  ref = Cl_element
FEATURE [App::DocumentObjectGroupPython] G4_POLYCHLOROSTYRENE  # scripted group (container) (typed FeaturePython)
  Dunit = g/cm3
  Dvalue = 1.3
  Group = -> [C_element080,H_element075,Cl_element017]
  conduct = 2
  density = 1
  expand = 3
  formula = G4_POLYCHLOROSTYRENE
  name = G4_POLYCHLOROSTYRENE
  specific = 4
FEATURE [App::DocumentObjectGroupPython] C_element081  label="C_element : 039"  # scripted group (container) (typed FeaturePython)
  n = 1
  ref = C_element
FEATURE [App::DocumentObjectGroupPython] H_element076  label="H_element : 038"  # scripted group (container) (typed FeaturePython)
  n = 2
  ref = H_element
FEATURE [App::DocumentObjectGroupPython] G4_POLYETHYLENE  # scripted group (container) (typed FeaturePython)
  Dunit = g/cm3
  Dvalue = 0.94
  Group = -> [C_element081,H_element076]
  conduct = 2
  density = 1
  expand = 3
  formula = G4_POLYETHYLENE
  name = G4_POLYETHYLENE
  specific = 4
FEATURE [App::DocumentObjectGroupPython] C_element082  label="C_element : 040"  # scripted group (container) (typed FeaturePython)
  n = 10
  ref = C_element
FEATURE [App::DocumentObjectGroupPython] H_element077  label="H_element : 039"  # scripted group (container) (typed FeaturePython)
  n = 8
  ref = H_element
FEATURE [App::DocumentObjectGroupPython] O_element078  label="O_element : 039"  # scripted group (container) (typed FeaturePython)
  n = 4
  ref = O_element
FEATURE [App::DocumentObjectGroupPython] G4_MYLAR  # scripted group (container) (typed FeaturePython)
  Dunit = g/cm3
  Dvalue = 1.4
  Group = -> [C_element082,H_element077,O_element078]
  conduct = 2
  density = 1
  expand = 3
  formula = G4_MYLAR
  name = G4_MYLAR
  specific = 4
FEATURE [App::DocumentObjectGroupPython] C_element083  label="C_element : 041"  # scripted group (container) (typed FeaturePython)
  n = 5
  ref = C_element
FEATURE [App::DocumentObjectGroupPython] H_element078  label="H_element : 040"  # scripted group (container) (typed FeaturePython)
  n = 8
  ref = H_element
FEATURE [App::DocumentObjectGroupPython] O_element079  label="O_element : 040"  # scripted group (container) (typed FeaturePython)
  n = 2
  ref = O_element
FEATURE [App::DocumentObjectGroupPython] G4_PLEXIGLASS  # scripted group (container) (typed FeaturePython)
  Dunit = g/cm3
  Dvalue = 1.19
  Group = -> [C_element083,H_element078,O_element079]
  conduct = 2
  density = 1
  expand = 3
  formula = G4_PLEXIGLASS
  name = G4_PLEXIGLASS
  specific = 4
FEATURE [App::DocumentObjectGroupPython] C_element084  label="C_element : 042"  # scripted group (container) (typed FeaturePython)
  n = 1
  ref = C_element
FEATURE [App::DocumentObjectGroupPython] H_element079  label="H_element : 041"  # scripted group (container) (typed FeaturePython)
  n = 2
  ref = H_element
FEATURE [App::DocumentObjectGroupPython] O_element080  label="O_element : 041"  # scripted group (container) (typed FeaturePython)
  n = 1
  ref = O_element
FEATURE [App::DocumentObjectGroupPython] G4_POLYOXYMETHYLENE  # scripted group (container) (typed FeaturePython)
  Dunit = g/cm3
  Dvalue = 1.425
  Group = -> [C_element084,H_element079,O_element080]
  conduct = 2
  density = 1
  expand = 3
  formula = G4_POLYOXYMETHYLENE
  name = G4_POLYOXYMETHYLENE
  specific = 4
FEATURE [App::DocumentObjectGroupPython] C_element085  label="C_element : 043"  # scripted group (container) (typed FeaturePython)
  n = 2
  ref = C_element
FEATURE [App::DocumentObjectGroupPython] H_element080  label="H_element : 042"  # scripted group (container) (typed FeaturePython)
  n = 4
  ref = H_element
FEATURE [App::DocumentObjectGroupPython] G4_POLYPROPYLENE  # scripted group (container) (typed FeaturePython)
  Dunit = g/cm3
  Dvalue = 0.9
  Group = -> [C_element085,H_element080]
  conduct = 2
  density = 1
  expand = 3
  formula = G4_POLYPROPYLENE
  name = G4_POLYPROPYLENE
  specific = 4
FEATURE [App::DocumentObjectGroupPython] C_element086  label="C_element : 044"  # scripted group (container) (typed FeaturePython)
  n = 8
  ref = C_element
FEATURE [App::DocumentObjectGroupPython] H_element081  label="H_element : 043"  # scripted group (container) (typed FeaturePython)
  n = 8
  ref = H_element
FEATURE [App::DocumentObjectGroupPython] G4_POLYSTYRENE  # scripted group (container) (typed FeaturePython)
  Dunit = g/cm3
  Dvalue = 1.06
  Group = -> [C_element086,H_element081]
  conduct = 2
  density = 1
  expand = 3
  formula = G4_POLYSTYRENE
  name = G4_POLYSTYRENE
  specific = 4
FEATURE [App::DocumentObjectGroupPython] C_element087  label="C_element : 045"  # scripted group (container) (typed FeaturePython)
  n = 2
  ref = C_element
FEATURE [App::DocumentObjectGroupPython] F_element014  label="F_element : 4"  # scripted group (container) (typed FeaturePython)
  n = 4
  ref = F_element
FEATURE [App::DocumentObjectGroupPython] G4_TEFLON  # scripted group (container) (typed FeaturePython)
  Dunit = g/cm3
  Dvalue = 2.2
  Group = -> [C_element087,F_element014]
  conduct = 2
  density = 1
  expand = 3
  formula = G4_TEFLON
  name = G4_TEFLON
  specific = 4
FEATURE [App::DocumentObjectGroupPython] C_element088  label="C_element : 046"  # scripted group (container) (typed FeaturePython)
  n = 2
  ref = C_element
FEATURE [App::DocumentObjectGroupPython] F_element015  label="F_element : 006"  # scripted group (container) (typed FeaturePython)
  n = 3
  ref = F_element
FEATURE [App::DocumentObjectGroupPython] Cl_element018  label="Cl_element : 008"  # scripted group (container) (typed FeaturePython)
  n = 1
  ref = Cl_element
FEATURE [App::DocumentObjectGroupPython] G4_POLYTRIFLUOROCHLOROETHYLENE  # scripted group (container) (typed FeaturePython)
  Dunit = g/cm3
  Dvalue = 2.1
  Group = -> [C_element088,F_element015,Cl_element018]
  conduct = 2
  density = 1
  expand = 3
  formula = G4_POLYTRIFLUOROCHLOROETHYLENE
  name = G4_POLYTRIFLUOROCHLOROETHYLENE
  specific = 4
FEATURE [App::DocumentObjectGroupPython] C_element089  label="C_element : 047"  # scripted group (container) (typed FeaturePython)
  n = 4
  ref = C_element
FEATURE [App::DocumentObjectGroupPython] H_element082  label="H_element : 044"  # scripted group (container) (typed FeaturePython)
  n = 6
  ref = H_element
FEATURE [App::DocumentObjectGroupPython] O_element081  label="O_element : 042"  # scripted group (container) (typed FeaturePython)
  n = 2
  ref = O_element
FEATURE [App::DocumentObjectGroupPython] G4_POLYVINYL_ACETATE  # scripted group (container) (typed FeaturePython)
  Dunit = g/cm3
  Dvalue = 1.19
  Group = -> [C_element089,H_element082,O_element081]
  conduct = 2
  density = 1
  expand = 3
  formula = G4_POLYVINYL_ACETATE
  name = G4_POLYVINYL_ACETATE
  specific = 4
FEATURE [App::DocumentObjectGroupPython] C_element090  label="C_element : 048"  # scripted group (container) (typed FeaturePython)
  n = 2
  ref = C_element
FEATURE [App::DocumentObjectGroupPython] H_element083  label="H_element : 045"  # scripted group (container) (typed FeaturePython)
  n = 4
  ref = H_element
FEATURE [App::DocumentObjectGroupPython] O_element082  label="O_element : 043"  # scripted group (container) (typed FeaturePython)
  n = 1
  ref = O_element
FEATURE [App::DocumentObjectGroupPython] G4_POLYVINYL_ALCOHOL  # scripted group (container) (typed FeaturePython)
  Dunit = g/cm3
  Dvalue = 1.3
  Group = -> [C_element090,H_element083,O_element082]
  conduct = 2
  density = 1
  expand = 3
  formula = G4_POLYVINYL_ALCOHOL
  name = G4_POLYVINYL_ALCOHOL
  specific = 4
FEATURE [App::DocumentObjectGroupPython] C_element091  label="C_element : 049"  # scripted group (container) (typed FeaturePython)
  n = 8
  ref = C_element
FEATURE [App::DocumentObjectGroupPython] H_element084  label="H_element : 046"  # scripted group (container) (typed FeaturePython)
  n = 14
  ref = H_element
FEATURE [App::DocumentObjectGroupPython] O_element083  label="O_element : 044"  # scripted group (container) (typed FeaturePython)
  n = 2
  ref = O_element
FEATURE [App::DocumentObjectGroupPython] G4_POLYVINYL_BUTYRAL  # scripted group (container) (typed FeaturePython)
  Dunit = g/cm3
  Dvalue = 1.12
  Group = -> [C_element091,H_element084,O_element083]
  conduct = 2
  density = 1
  expand = 3
  formula = G4_POLYVINYL_BUTYRAL
  name = G4_POLYVINYL_BUTYRAL
  specific = 4
FEATURE [App::DocumentObjectGroupPython] C_element092  label="C_element : 050"  # scripted group (container) (typed FeaturePython)
  n = 2
  ref = C_element
FEATURE [App::DocumentObjectGroupPython] H_element085  label="H_element : 047"  # scripted group (container) (typed FeaturePython)
  n = 3
  ref = H_element
FEATURE [App::DocumentObjectGroupPython] Cl_element019  label="Cl_element : 009"  # scripted group (container) (typed FeaturePython)
  n = 1
  ref = Cl_element
FEATURE [App::DocumentObjectGroupPython] G4_POLYVINYL_CHLORIDE  # scripted group (container) (typed FeaturePython)
  Dunit = g/cm3
  Dvalue = 1.3
  Group = -> [C_element092,H_element085,Cl_element019]
  conduct = 2
  density = 1
  expand = 3
  formula = G4_POLYVINYL_CHLORIDE
  name = G4_POLYVINYL_CHLORIDE
  specific = 4
FEATURE [App::DocumentObjectGroupPython] C_element093  label="C_element : 051"  # scripted group (container) (typed FeaturePython)
  n = 2
  ref = C_element
FEATURE [App::DocumentObjectGroupPython] H_element086  label="H_element : 048"  # scripted group (container) (typed FeaturePython)
  n = 2
  ref = H_element
FEATURE [App::DocumentObjectGroupPython] Cl_element020  label="Cl_element : 010"  # scripted group (container) (typed FeaturePython)
  n = 2
  ref = Cl_element
FEATURE [App::DocumentObjectGroupPython] G4_POLYVINYLIDENE_CHLORIDE  # scripted group (container) (typed FeaturePython)
  Dunit = g/cm3
  Dvalue = 1.7
  Group = -> [C_element093,H_element086,Cl_element020]
  conduct = 2
  density = 1
  expand = 3
  formula = G4_POLYVINYLIDENE_CHLORIDE
  name = G4_POLYVINYLIDENE_CHLORIDE
  specific = 4
FEATURE [App::DocumentObjectGroupPython] C_element094  label="C_element : 052"  # scripted group (container) (typed FeaturePython)
  n = 2
  ref = C_element
FEATURE [App::DocumentObjectGroupPython] H_element087  label="H_element : 049"  # scripted group (container) (typed FeaturePython)
  n = 2
  ref = H_element
FEATURE [App::DocumentObjectGroupPython] F_element016  label="F_element : 007"  # scripted group (container) (typed FeaturePython)
  n = 2
  ref = F_element
FEATURE [App::DocumentObjectGroupPython] G4_POLYVINYLIDENE_FLUORIDE  # scripted group (container) (typed FeaturePython)
  Dunit = g/cm3
  Dvalue = 1.76
  Group = -> [C_element094,H_element087,F_element016]
  conduct = 2
  density = 1
  expand = 3
  formula = G4_POLYVINYLIDENE_FLUORIDE
  name = G4_POLYVINYLIDENE_FLUORIDE
  specific = 4
FEATURE [App::DocumentObjectGroupPython] C_element095  label="C_element : 053"  # scripted group (container) (typed FeaturePython)
  n = 6
  ref = C_element
FEATURE [App::DocumentObjectGroupPython] H_element088  label="H_element : 9"  # scripted group (container) (typed FeaturePython)
  n = 9
  ref = H_element
FEATURE [App::DocumentObjectGroupPython] N_element037  label="N_element : 016"  # scripted group (container) (typed FeaturePython)
  n = 1
  ref = N_element
FEATURE [App::DocumentObjectGroupPython] O_element084  label="O_element : 045"  # scripted group (container) (typed FeaturePython)
  n = 1
  ref = O_element
FEATURE [App::DocumentObjectGroupPython] G4_POLYVINYL_PYRROLIDONE  # scripted group (container) (typed FeaturePython)
  Dunit = g/cm3
  Dvalue = 1.25
  Group = -> [C_element095,H_element088,N_element037,O_element084]
  conduct = 2
  density = 1
  expand = 3
  formula = G4_POLYVINYL_PYRROLIDONE
  name = G4_POLYVINYL_PYRROLIDONE
  specific = 4
FEATURE [App::DocumentObjectGroupPython] K_element008  label="K_element : 1"  # scripted group (container) (typed FeaturePython)
  n = 1
  ref = K_element
FEATURE [App::DocumentObjectGroupPython] I_element006  label="I_element : 003"  # scripted group (container) (typed FeaturePython)
  n = 1
  ref = I_element
FEATURE [App::DocumentObjectGroupPython] G4_POTASSIUM_IODIDE  # scripted group (container) (typed FeaturePython)
  Dunit = g/cm3
  Dvalue = 3.13
  Group = -> [K_element008,I_element006]
  conduct = 2
  density = 1
  expand = 3
  formula = G4_POTASSIUM_IODIDE
  name = G4_POTASSIUM_IODIDE
  specific = 4
FEATURE [App::DocumentObjectGroupPython] K_element009  label="K_element : 2"  # scripted group (container) (typed FeaturePython)
  n = 2
  ref = K_element
FEATURE [App::DocumentObjectGroupPython] O_element085  label="O_element : 046"  # scripted group (container) (typed FeaturePython)
  n = 1
  ref = O_element
FEATURE [App::DocumentObjectGroupPython] G4_POTASSIUM_OXIDE  # scripted group (container) (typed FeaturePython)
  Dunit = g/cm3
  Dvalue = 2.32
  Group = -> [K_element009,O_element085]
  conduct = 2
  density = 1
  expand = 3
  formula = G4_POTASSIUM_OXIDE
  name = G4_POTASSIUM_OXIDE
  specific = 4
FEATURE [App::DocumentObjectGroupPython] C_element096  label="C_element : 054"  # scripted group (container) (typed FeaturePython)
  n = 3
  ref = C_element
FEATURE [App::DocumentObjectGroupPython] H_element089  label="H_element : 050"  # scripted group (container) (typed FeaturePython)
  n = 8
  ref = H_element
FEATURE [App::DocumentObjectGroupPython] G4_PROPANE  # scripted group (container) (typed FeaturePython)
  Dunit = g/cm3
  Dvalue = 0.00187939
  Group = -> [C_element096,H_element089]
  conduct = 2
  density = 1
  expand = 3
  formula = G4_PROPANE
  name = G4_PROPANE
  specific = 4
FEATURE [App::DocumentObjectGroupPython] C_element097  label="C_element : 055"  # scripted group (container) (typed FeaturePython)
  n = 3
  ref = C_element
FEATURE [App::DocumentObjectGroupPython] H_element090  label="H_element : 051"  # scripted group (container) (typed FeaturePython)
  n = 8
  ref = H_element
FEATURE [App::DocumentObjectGroupPython] G4_lPROPANE  # scripted group (container) (typed FeaturePython)
  Dunit = g/cm3
  Dvalue = 0.43
  Group = -> [C_element097,H_element090]
  conduct = 2
  density = 1
  expand = 3
  formula = G4_lPROPANE
  name = G4_lPROPANE
  specific = 4
FEATURE [App::DocumentObjectGroupPython] C_element098  label="C_element : 056"  # scripted group (container) (typed FeaturePython)
  n = 3
  ref = C_element
FEATURE [App::DocumentObjectGroupPython] H_element091  label="H_element : 052"  # scripted group (container) (typed FeaturePython)
  n = 8
  ref = H_element
FEATURE [App::DocumentObjectGroupPython] O_element086  label="O_element : 047"  # scripted group (container) (typed FeaturePython)
  n = 1
  ref = O_element
FEATURE [App::DocumentObjectGroupPython] G4_N_PROPYL_ALCOHOL  # scripted group (container) (typed FeaturePython)
  Dunit = g/cm3
  Dvalue = 0.8035
  Group = -> [C_element098,H_element091,O_element086]
  conduct = 2
  density = 1
  expand = 3
  formula = G4_N-PROPYL_ALCOHOL
  name = G4_N-PROPYL_ALCOHOL
  specific = 4
FEATURE [App::DocumentObjectGroupPython] C_element099  label="C_element : 057"  # scripted group (container) (typed FeaturePython)
  n = 5
  ref = C_element
FEATURE [App::DocumentObjectGroupPython] H_element092  label="H_element : 053"  # scripted group (container) (typed FeaturePython)
  n = 5
  ref = H_element
FEATURE [App::DocumentObjectGroupPython] N_element038  label="N_element : 017"  # scripted group (container) (typed FeaturePython)
  n = 1
  ref = N_element
FEATURE [App::DocumentObjectGroupPython] G4_PYRIDINE  # scripted group (container) (typed FeaturePython)
  Dunit = g/cm3
  Dvalue = 0.9819
  Group = -> [C_element099,H_element092,N_element038]
  conduct = 2
  density = 1
  expand = 3
  formula = G4_PYRIDINE
  name = G4_PYRIDINE
  specific = 4
FEATURE [App::DocumentObjectGroupPython] H_element093  label="H_element : 0.144"  # scripted group (container) (typed FeaturePython)
  n = 0.143711
FEATURE [App::DocumentObjectGroupPython] C_element100  label="C_element : 0.856"  # scripted group (container) (typed FeaturePython)
  n = 0.856289
FEATURE [App::DocumentObjectGroupPython] G4_RUBBER_BUTYL  # scripted group (container) (typed FeaturePython)
  Dunit = g/cm3
  Dvalue = 0.92
  Group = -> [H_element093,C_element100]
  conduct = 2
  density = 1
  expand = 3
  formula = G4_RUBBER_BUTYL
  name = G4_RUBBER_BUTYL
  specific = 4
FEATURE [App::DocumentObjectGroupPython] H_element094  label="H_element : 0.118"  # scripted group (container) (typed FeaturePython)
  n = 0.118371
FEATURE [App::DocumentObjectGroupPython] C_element101  label="C_element : 0.882"  # scripted group (container) (typed FeaturePython)
  n = 0.881629
FEATURE [App::DocumentObjectGroupPython] G4_RUBBER_NATURAL  # scripted group (container) (typed FeaturePython)
  Dunit = g/cm3
  Dvalue = 0.92
  Group = -> [H_element094,C_element101]
  conduct = 2
  density = 1
  expand = 3
  formula = G4_RUBBER_NATURAL
  name = G4_RUBBER_NATURAL
  specific = 4
FEATURE [App::DocumentObjectGroupPython] H_element095  label="H_element : 0.145"  # scripted group (container) (typed FeaturePython)
  n = 0.05692
FEATURE [App::DocumentObjectGroupPython] C_element102  label="C_element : 0.543"  # scripted group (container) (typed FeaturePython)
  n = 0.542646
FEATURE [App::DocumentObjectGroupPython] Cl_element021  label="Cl_element : 0.400"  # scripted group (container) (typed FeaturePython)
  n = 0.400434
FEATURE [App::DocumentObjectGroupPython] G4_RUBBER_NEOPRENE  # scripted group (container) (typed FeaturePython)
  Dunit = g/cm3
  Dvalue = 1.23
  Group = -> [H_element095,C_element102,Cl_element021]
  conduct = 2
  density = 1
  expand = 3
  formula = G4_RUBBER_NEOPRENE
  name = G4_RUBBER_NEOPRENE
  specific = 4
FEATURE [App::DocumentObjectGroupPython] Si_element006  label="Si_element : 1"  # scripted group (container) (typed FeaturePython)
  n = 1
  ref = Si_element
FEATURE [App::DocumentObjectGroupPython] O_element087  label="O_element : 048"  # scripted group (container) (typed FeaturePython)
  n = 2
  ref = O_element
FEATURE [App::DocumentObjectGroupPython] G4_SILICON_DIOXIDE  # scripted group (container) (typed FeaturePython)
  Dunit = g/cm3
  Dvalue = 2.32
  Group = -> [Si_element006,O_element087]
  conduct = 2
  density = 1
  expand = 3
  formula = G4_SILICON_DIOXIDE
  name = G4_SILICON_DIOXIDE
  specific = 4
FEATURE [App::DocumentObjectGroupPython] Ag_element002  label="Ag_element : 1"  # scripted group (container) (typed FeaturePython)
  n = 1
  ref = Ag_element
FEATURE [App::DocumentObjectGroupPython] Br_element005  label="Br_element : 003"  # scripted group (container) (typed FeaturePython)
  n = 1
  ref = Br_element
FEATURE [App::DocumentObjectGroupPython] G4_SILVER_BROMIDE  # scripted group (container) (typed FeaturePython)
  Dunit = g/cm3
  Dvalue = 6.473
  Group = -> [Ag_element002,Br_element005]
  conduct = 2
  density = 1
  expand = 3
  formula = G4_SILVER_BROMIDE
  name = G4_SILVER_BROMIDE
  specific = 4
FEATURE [App::DocumentObjectGroupPython] Ag_element003  label="Ag_element : 002"  # scripted group (container) (typed FeaturePython)
  n = 1
  ref = Ag_element
FEATURE [App::DocumentObjectGroupPython] Cl_element022  label="Cl_element : 011"  # scripted group (container) (typed FeaturePython)
  n = 1
  ref = Cl_element
FEATURE [App::DocumentObjectGroupPython] G4_SILVER_CHLORIDE  # scripted group (container) (typed FeaturePython)
  Dunit = g/cm3
  Dvalue = 5.56
  Group = -> [Ag_element003,Cl_element022]
  conduct = 2
  density = 1
  expand = 3
  formula = G4_SILVER_CHLORIDE
  name = G4_SILVER_CHLORIDE
  specific = 4
FEATURE [App::DocumentObjectGroupPython] Br_element006  label="Br_element : 0.423"  # scripted group (container) (typed FeaturePython)
  n = 0.422895
FEATURE [App::DocumentObjectGroupPython] Ag_element004  label="Ag_element : 0.574"  # scripted group (container) (typed FeaturePython)
  n = 0.573748
FEATURE [App::DocumentObjectGroupPython] I_element007  label="I_element : 0.649"  # scripted group (container) (typed FeaturePython)
  n = 0.003357
FEATURE [App::DocumentObjectGroupPython] G4_SILVER_HALIDES  # scripted group (container) (typed FeaturePython)
  Dunit = g/cm3
  Dvalue = 6.47
  Group = -> [Br_element006,Ag_element004,I_element007]
  conduct = 2
  density = 1
  expand = 3
  formula = G4_SILVER_HALIDES
  name = G4_SILVER_HALIDES
  specific = 4
FEATURE [App::DocumentObjectGroupPython] Ag_element005  label="Ag_element : 003"  # scripted group (container) (typed FeaturePython)
  n = 1
  ref = Ag_element
FEATURE [App::DocumentObjectGroupPython] I_element008  label="I_element : 004"  # scripted group (container) (typed FeaturePython)
  n = 1
  ref = I_element
FEATURE [App::DocumentObjectGroupPython] G4_SILVER_IODIDE  # scripted group (container) (typed FeaturePython)
  Dunit = g/cm3
  Dvalue = 6.01
  Group = -> [Ag_element005,I_element008]
  conduct = 2
  density = 1
  expand = 3
  formula = G4_SILVER_IODIDE
  name = G4_SILVER_IODIDE
  specific = 4
FEATURE [App::DocumentObjectGroupPython] H_element096  label="H_element : 0.100"  # scripted group (container) (typed FeaturePython)
  n = 0.1
FEATURE [App::DocumentObjectGroupPython] C_element103  label="C_element : 0.204"  # scripted group (container) (typed FeaturePython)
  n = 0.204
FEATURE [App::DocumentObjectGroupPython] N_element039  label="N_element : 0.759"  # scripted group (container) (typed FeaturePython)
  n = 0.042
FEATURE [App::DocumentObjectGroupPython] O_element088  label="O_element : 0.645"  # scripted group (container) (typed FeaturePython)
  n = 0.645
FEATURE [App::DocumentObjectGroupPython] Na_element013  label="Na_element : 0.100"  # scripted group (container) (typed FeaturePython)
  n = 0.002
FEATURE [App::DocumentObjectGroupPython] P_element009  label="P_element : 0.107"  # scripted group (container) (typed FeaturePython)
  n = 0.001
FEATURE [App::DocumentObjectGroupPython] S_element020  label="S_element : 0.021"  # scripted group (container) (typed FeaturePython)
  n = 0.002
FEATURE [App::DocumentObjectGroupPython] Cl_element023  label="Cl_element : 0.590"  # scripted group (container) (typed FeaturePython)
  n = 0.003
FEATURE [App::DocumentObjectGroupPython] K_element010  label="K_element : 0.001"  # scripted group (container) (typed FeaturePython)
  n = 0.001
FEATURE [App::DocumentObjectGroupPython] G4_SKIN_ICRP  # scripted group (container) (typed FeaturePython)
  Dunit = g/cm3
  Dvalue = 1.09
  Group = -> [H_element096,C_element103,N_element039,O_element088,Na_element013,P_element009,S_element020,Cl_element023,K_element010]
  conduct = 2
  density = 1
  expand = 3
  formula = G4_SKIN_ICRP
  name = G4_SKIN_ICRP
  specific = 4
FEATURE [App::DocumentObjectGroupPython] Na_element014  label="Na_element : 2"  # scripted group (container) (typed FeaturePython)
  n = 2
  ref = Na_element
FEATURE [App::DocumentObjectGroupPython] C_element104  label="C_element : 058"  # scripted group (container) (typed FeaturePython)
  n = 1
  ref = C_element
FEATURE [App::DocumentObjectGroupPython] O_element089  label="O_element : 049"  # scripted group (container) (typed FeaturePython)
  n = 3
  ref = O_element
FEATURE [App::DocumentObjectGroupPython] G4_SODIUM_CARBONATE  # scripted group (container) (typed FeaturePython)
  Dunit = g/cm3
  Dvalue = 2.532
  Group = -> [Na_element014,C_element104,O_element089]
  conduct = 2
  density = 1
  expand = 3
  formula = G4_SODIUM_CARBONATE
  name = G4_SODIUM_CARBONATE
  specific = 4
FEATURE [App::DocumentObjectGroupPython] Na_element015  label="Na_element : 1"  # scripted group (container) (typed FeaturePython)
  n = 1
  ref = Na_element
FEATURE [App::DocumentObjectGroupPython] I_element009  label="I_element : 005"  # scripted group (container) (typed FeaturePython)
  n = 1
  ref = I_element
FEATURE [App::DocumentObjectGroupPython] G4_SODIUM_IODIDE  # scripted group (container) (typed FeaturePython)
  Dunit = g/cm3
  Dvalue = 3.667
  Group = -> [Na_element015,I_element009]
  conduct = 2
  density = 1
  expand = 3
  formula = G4_SODIUM_IODIDE
  name = G4_SODIUM_IODIDE
  specific = 4
FEATURE [App::DocumentObjectGroupPython] Na_element016  label="Na_element : 003"  # scripted group (container) (typed FeaturePython)
  n = 2
  ref = Na_element
FEATURE [App::DocumentObjectGroupPython] O_element090  label="O_element : 050"  # scripted group (container) (typed FeaturePython)
  n = 1
  ref = O_element
FEATURE [App::DocumentObjectGroupPython] G4_SODIUM_MONOXIDE  # scripted group (container) (typed FeaturePython)
  Dunit = g/cm3
  Dvalue = 2.27
  Group = -> [Na_element016,O_element090]
  conduct = 2
  density = 1
  expand = 3
  formula = G4_SODIUM_MONOXIDE
  name = G4_SODIUM_MONOXIDE
  specific = 4
FEATURE [App::DocumentObjectGroupPython] Na_element017  label="Na_element : 004"  # scripted group (container) (typed FeaturePython)
  n = 1
  ref = Na_element
FEATURE [App::DocumentObjectGroupPython] N_element040  label="N_element : 018"  # scripted group (container) (typed FeaturePython)
  n = 1
  ref = N_element
FEATURE [App::DocumentObjectGroupPython] O_element091  label="O_element : 051"  # scripted group (container) (typed FeaturePython)
  n = 3
  ref = O_element
FEATURE [App::DocumentObjectGroupPython] G4_SODIUM_NITRATE  # scripted group (container) (typed FeaturePython)
  Dunit = g/cm3
  Dvalue = 2.261
  Group = -> [Na_element017,N_element040,O_element091]
  conduct = 2
  density = 1
  expand = 3
  formula = G4_SODIUM_NITRATE
  name = G4_SODIUM_NITRATE
  specific = 4
FEATURE [App::DocumentObjectGroupPython] C_element105  label="C_element : 059"  # scripted group (container) (typed FeaturePython)
  n = 14
  ref = C_element
FEATURE [App::DocumentObjectGroupPython] H_element097  label="H_element : 054"  # scripted group (container) (typed FeaturePython)
  n = 12
  ref = H_element
FEATURE [App::DocumentObjectGroupPython] G4_STILBENE  # scripted group (container) (typed FeaturePython)
  Dunit = g/cm3
  Dvalue = 0.9707
  Group = -> [C_element105,H_element097]
  conduct = 2
  density = 1
  expand = 3
  formula = G4_STILBENE
  name = G4_STILBENE
  specific = 4
FEATURE [App::DocumentObjectGroupPython] C_element106  label="C_element : 12"  # scripted group (container) (typed FeaturePython)
  n = 12
  ref = C_element
FEATURE [App::DocumentObjectGroupPython] H_element098  label="H_element : 22"  # scripted group (container) (typed FeaturePython)
  n = 22
  ref = H_element
FEATURE [App::DocumentObjectGroupPython] O_element092  label="O_element : 11"  # scripted group (container) (typed FeaturePython)
  n = 11
  ref = O_element
FEATURE [App::DocumentObjectGroupPython] G4_SUCROSE  # scripted group (container) (typed FeaturePython)
  Dunit = g/cm3
  Dvalue = 1.5805
  Group = -> [C_element106,H_element098,O_element092]
  conduct = 2
  density = 1
  expand = 3
  formula = G4_SUCROSE
  name = G4_SUCROSE
  specific = 4
FEATURE [App::DocumentObjectGroupPython] C_element107  label="C_element : 18"  # scripted group (container) (typed FeaturePython)
  n = 18
  ref = C_element
FEATURE [App::DocumentObjectGroupPython] H_element099  label="H_element : 055"  # scripted group (container) (typed FeaturePython)
  n = 14
  ref = H_element
FEATURE [App::DocumentObjectGroupPython] G4_TERPHENYL  # scripted group (container) (typed FeaturePython)
  Dunit = g/cm3
  Dvalue = 1.24
  Group = -> [C_element107,H_element099]
  conduct = 2
  density = 1
  expand = 3
  formula = G4_TERPHENYL
  name = G4_TERPHENYL
  specific = 4
FEATURE [App::DocumentObjectGroupPython] H_element100  label="H_element : 0.146"  # scripted group (container) (typed FeaturePython)
  n = 0.106
FEATURE [App::DocumentObjectGroupPython] C_element108  label="C_element : 0.883"  # scripted group (container) (typed FeaturePython)
  n = 0.099
FEATURE [App::DocumentObjectGroupPython] N_element041  label="N_element : 0.020"  # scripted group (container) (typed FeaturePython)
  n = 0.02
FEATURE [App::DocumentObjectGroupPython] O_element093  label="O_element : 0.766"  # scripted group (container) (typed FeaturePython)
  n = 0.766
FEATURE [App::DocumentObjectGroupPython] Na_element018  label="Na_element : 0.101"  # scripted group (container) (typed FeaturePython)
  n = 0.002
FEATURE [App::DocumentObjectGroupPython] P_element010  label="P_element : 0.108"  # scripted group (container) (typed FeaturePython)
  n = 0.001
FEATURE [App::DocumentObjectGroupPython] S_element021  label="S_element : 0.022"  # scripted group (container) (typed FeaturePython)
  n = 0.002
FEATURE [App::DocumentObjectGroupPython] Cl_element024  label="Cl_element : 0.002"  # scripted group (container) (typed FeaturePython)
  n = 0.002
FEATURE [App::DocumentObjectGroupPython] K_element011  label="K_element : 0.017"  # scripted group (container) (typed FeaturePython)
  n = 0.002
FEATURE [App::DocumentObjectGroupPython] G4_TESTIS_ICRP  # scripted group (container) (typed FeaturePython)
  Dunit = g/cm3
  Dvalue = 1.04
  Group = -> [H_element100,C_element108,N_element041,O_element093,Na_element018,P_element010,S_element021,Cl_element024,K_element011]
  conduct = 2
  density = 1
  expand = 3
  formula = G4_TESTIS_ICRP
  name = G4_TESTIS_ICRP
  specific = 4
FEATURE [App::DocumentObjectGroupPython] C_element109  label="C_element : 060"  # scripted group (container) (typed FeaturePython)
  n = 2
  ref = C_element
FEATURE [App::DocumentObjectGroupPython] Cl_element025  label="Cl_element : 012"  # scripted group (container) (typed FeaturePython)
  n = 4
  ref = Cl_element
FEATURE [App::DocumentObjectGroupPython] G4_TETRACHLOROETHYLENE  # scripted group (container) (typed FeaturePython)
  Dunit = g/cm3
  Dvalue = 1.625
  Group = -> [C_element109,Cl_element025]
  conduct = 2
  density = 1
  expand = 3
  formula = G4_TETRACHLOROETHYLENE
  name = G4_TETRACHLOROETHYLENE
  specific = 4
FEATURE [App::DocumentObjectGroupPython] Tl_element001  label="Tl_element : 1"  # scripted group (container) (typed FeaturePython)
  n = 1
  ref = Tl_element
FEATURE [App::DocumentObjectGroupPython] Cl_element026  label="Cl_element : 013"  # scripted group (container) (typed FeaturePython)
  n = 1
  ref = Cl_element
FEATURE [App::DocumentObjectGroupPython] G4_THALLIUM_CHLORIDE  # scripted group (container) (typed FeaturePython)
  Dunit = g/cm3
  Dvalue = 7.004
  Group = -> [Tl_element001,Cl_element026]
  conduct = 2
  density = 1
  expand = 3
  formula = G4_THALLIUM_CHLORIDE
  name = G4_THALLIUM_CHLORIDE
  specific = 4
FEATURE [App::DocumentObjectGroupPython] H_element101  label="H_element : 0.147"  # scripted group (container) (typed FeaturePython)
  n = 0.105
FEATURE [App::DocumentObjectGroupPython] C_element110  label="C_element : 0.256"  # scripted group (container) (typed FeaturePython)
  n = 0.256
FEATURE [App::DocumentObjectGroupPython] N_element042  label="N_element : 0.760"  # scripted group (container) (typed FeaturePython)
  n = 0.027
FEATURE [App::DocumentObjectGroupPython] O_element094  label="O_element : 0.602"  # scripted group (container) (typed FeaturePython)
  n = 0.602
FEATURE [App::DocumentObjectGroupPython] Na_element019  label="Na_element : 0.102"  # scripted group (container) (typed FeaturePython)
  n = 0.001
FEATURE [App::DocumentObjectGroupPython] P_element011  label="P_element : 0.109"  # scripted group (container) (typed FeaturePython)
  n = 0.002
FEATURE [App::DocumentObjectGroupPython] S_element022  label="S_element : 0.023"  # scripted group (container) (typed FeaturePython)
  n = 0.003
FEATURE [App::DocumentObjectGroupPython] Cl_element027  label="Cl_element : 0.591"  # scripted group (container) (typed FeaturePython)
  n = 0.002
FEATURE [App::DocumentObjectGroupPython] K_element012  label="K_element : 0.018"  # scripted group (container) (typed FeaturePython)
  n = 0.002
FEATURE [App::DocumentObjectGroupPython] G4_TISSUE_SOFT_ICRP  # scripted group (container) (typed FeaturePython)
  Dunit = g/cm3
  Dvalue = 1.03
  Group = -> [H_element101,C_element110,N_element042,O_element094,Na_element019,P_element011,S_element022,Cl_element027,K_element012]
  conduct = 2
  density = 1
  expand = 3
  formula = G4_TISSUE_SOFT_ICRP
  name = G4_TISSUE_SOFT_ICRP
  specific = 4
FEATURE [App::DocumentObjectGroupPython] H_element102  label="H_element : 0.148"  # scripted group (container) (typed FeaturePython)
  n = 0.101
FEATURE [App::DocumentObjectGroupPython] C_element111  label="C_element : 0.111"  # scripted group (container) (typed FeaturePython)
  n = 0.111
FEATURE [App::DocumentObjectGroupPython] N_element043  label="N_element : 0.026"  # scripted group (container) (typed FeaturePython)
  n = 0.026
FEATURE [App::DocumentObjectGroupPython] O_element095  label="O_element : 0.762"  # scripted group (container) (typed FeaturePython)
  n = 0.762
FEATURE [App::DocumentObjectGroupPython] G4_TISSUE_SOFT_ICRU_4  # scripted group (container) (typed FeaturePython)
  Dunit = g/cm3
  Dvalue = 1
  Group = -> [H_element102,C_element111,N_element043,O_element095]
  conduct = 2
  density = 1
  expand = 3
  formula = G4_TISSUE_SOFT_ICRU-4
  name = G4_TISSUE_SOFT_ICRU-4
  specific = 4
FEATURE [App::DocumentObjectGroupPython] H_element103  label="H_element : 0.149"  # scripted group (container) (typed FeaturePython)
  n = 0.101869
FEATURE [App::DocumentObjectGroupPython] C_element112  label="C_element : 0.456"  # scripted group (container) (typed FeaturePython)
  n = 0.456179
FEATURE [App::DocumentObjectGroupPython] N_element044  label="N_element : 0.761"  # scripted group (container) (typed FeaturePython)
  n = 0.035172
FEATURE [App::DocumentObjectGroupPython] O_element096  label="O_element : 0.407"  # scripted group (container) (typed FeaturePython)
  n = 0.40678
FEATURE [App::DocumentObjectGroupPython] G4_TISSUE_METHANE  # scripted group (container) (typed FeaturePython)
  Dunit = g/cm3
  Dvalue = 0.00106409
  Group = -> [H_element103,C_element112,N_element044,O_element096]
  conduct = 2
  density = 1
  expand = 3
  formula = G4_TISSUE-METHANE
  name = G4_TISSUE-METHANE
  specific = 4
FEATURE [App::DocumentObjectGroupPython] H_element104  label="H_element : 0.103"  # scripted group (container) (typed FeaturePython)
  n = 0.102672
FEATURE [App::DocumentObjectGroupPython] C_element113  label="C_element : 0.569"  # scripted group (container) (typed FeaturePython)
  n = 0.56894
FEATURE [App::DocumentObjectGroupPython] N_element045  label="N_element : 0.762"  # scripted group (container) (typed FeaturePython)
  n = 0.035022
FEATURE [App::DocumentObjectGroupPython] O_element097  label="O_element : 0.293"  # scripted group (container) (typed FeaturePython)
  n = 0.293366
FEATURE [App::DocumentObjectGroupPython] G4_TISSUE_PROPANE  # scripted group (container) (typed FeaturePython)
  Dunit = g/cm3
  Dvalue = 0.00182628
  Group = -> [H_element104,C_element113,N_element045,O_element097]
  conduct = 2
  density = 1
  expand = 3
  formula = G4_TISSUE-PROPANE
  name = G4_TISSUE-PROPANE
  specific = 4
FEATURE [App::DocumentObjectGroupPython] Ti_element003  label="Ti_element : 1"  # scripted group (container) (typed FeaturePython)
  n = 1
  ref = Ti_element
FEATURE [App::DocumentObjectGroupPython] O_element098  label="O_element : 052"  # scripted group (container) (typed FeaturePython)
  n = 2
  ref = O_element
FEATURE [App::DocumentObjectGroupPython] G4_TITANIUM_DIOXIDE  # scripted group (container) (typed FeaturePython)
  Dunit = g/cm3
  Dvalue = 4.26
  Group = -> [Ti_element003,O_element098]
  conduct = 2
  density = 1
  expand = 3
  formula = G4_TITANIUM_DIOXIDE
  name = G4_TITANIUM_DIOXIDE
  specific = 4
FEATURE [App::DocumentObjectGroupPython] C_element114  label="C_element : 061"  # scripted group (container) (typed FeaturePython)
  n = 7
  ref = C_element
FEATURE [App::DocumentObjectGroupPython] H_element105  label="H_element : 056"  # scripted group (container) (typed FeaturePython)
  n = 8
  ref = H_element
FEATURE [App::DocumentObjectGroupPython] G4_TOLUENE  # scripted group (container) (typed FeaturePython)
  Dunit = g/cm3
  Dvalue = 0.8669
  Group = -> [C_element114,H_element105]
  conduct = 2
  density = 1
  expand = 3
  formula = G4_TOLUENE
  name = G4_TOLUENE
  specific = 4
FEATURE [App::DocumentObjectGroupPython] C_element115  label="C_element : 062"  # scripted group (container) (typed FeaturePython)
  n = 2
  ref = C_element
FEATURE [App::DocumentObjectGroupPython] H_element106  label="H_element : 057"  # scripted group (container) (typed FeaturePython)
  n = 1
  ref = H_element
FEATURE [App::DocumentObjectGroupPython] Cl_element028  label="Cl_element : 014"  # scripted group (container) (typed FeaturePython)
  n = 3
  ref = Cl_element
FEATURE [App::DocumentObjectGroupPython] G4_TRICHLOROETHYLENE  # scripted group (container) (typed FeaturePython)
  Dunit = g/cm3
  Dvalue = 1.46
  Group = -> [C_element115,H_element106,Cl_element028]
  conduct = 2
  density = 1
  expand = 3
  formula = G4_TRICHLOROETHYLENE
  name = G4_TRICHLOROETHYLENE
  specific = 4
FEATURE [App::DocumentObjectGroupPython] C_element116  label="C_element : 063"  # scripted group (container) (typed FeaturePython)
  n = 6
  ref = C_element
FEATURE [App::DocumentObjectGroupPython] H_element107  label="H_element : 15"  # scripted group (container) (typed FeaturePython)
  n = 15
  ref = H_element
FEATURE [App::DocumentObjectGroupPython] O_element099  label="O_element : 053"  # scripted group (container) (typed FeaturePython)
  n = 4
  ref = O_element
FEATURE [App::DocumentObjectGroupPython] P_element012  label="P_element : 1"  # scripted group (container) (typed FeaturePython)
  n = 1
  ref = P_element
FEATURE [App::DocumentObjectGroupPython] G4_TRIETHYL_PHOSPHATE  # scripted group (container) (typed FeaturePython)
  Dunit = g/cm3
  Dvalue = 1.07
  Group = -> [C_element116,H_element107,O_element099,P_element012]
  conduct = 2
  density = 1
  expand = 3
  formula = G4_TRIETHYL_PHOSPHATE
  name = G4_TRIETHYL_PHOSPHATE
  specific = 4
FEATURE [App::DocumentObjectGroupPython] W_element003  label="W_element : 003"  # scripted group (container) (typed FeaturePython)
  n = 1
  ref = W_element
FEATURE [App::DocumentObjectGroupPython] F_element017  label="F_element : 6"  # scripted group (container) (typed FeaturePython)
  n = 6
  ref = F_element
FEATURE [App::DocumentObjectGroupPython] G4_TUNGSTEN_HEXAFLUORIDE  # scripted group (container) (typed FeaturePython)
  Dunit = g/cm3
  Dvalue = 2.4
  Group = -> [W_element003,F_element017]
  conduct = 2
  density = 1
  expand = 3
  formula = G4_TUNGSTEN_HEXAFLUORIDE
  name = G4_TUNGSTEN_HEXAFLUORIDE
  specific = 4
FEATURE [App::DocumentObjectGroupPython] U_element001  label="U_element : 1"  # scripted group (container) (typed FeaturePython)
  n = 1
  ref = U_element
FEATURE [App::DocumentObjectGroupPython] C_element117  label="C_element : 064"  # scripted group (container) (typed FeaturePython)
  n = 2
  ref = C_element
FEATURE [App::DocumentObjectGroupPython] G4_URANIUM_DICARBIDE  # scripted group (container) (typed FeaturePython)
  Dunit = g/cm3
  Dvalue = 11.28
  Group = -> [U_element001,C_element117]
  conduct = 2
  density = 1
  expand = 3
  formula = G4_URANIUM_DICARBIDE
  name = G4_URANIUM_DICARBIDE
  specific = 4
FEATURE [App::DocumentObjectGroupPython] U_element002  label="U_element : 002"  # scripted group (container) (typed FeaturePython)
  n = 1
  ref = U_element
FEATURE [App::DocumentObjectGroupPython] C_element118  label="C_element : 065"  # scripted group (container) (typed FeaturePython)
  n = 1
  ref = C_element
FEATURE [App::DocumentObjectGroupPython] G4_URANIUM_MONOCARBIDE  # scripted group (container) (typed FeaturePython)
  Dunit = g/cm3
  Dvalue = 13.63
  Group = -> [U_element002,C_element118]
  conduct = 2
  density = 1
  expand = 3
  formula = G4_URANIUM_MONOCARBIDE
  name = G4_URANIUM_MONOCARBIDE
  specific = 4
FEATURE [App::DocumentObjectGroupPython] U_element003  label="U_element : 003"  # scripted group (container) (typed FeaturePython)
  n = 1
  ref = U_element
FEATURE [App::DocumentObjectGroupPython] O_element100  label="O_element : 054"  # scripted group (container) (typed FeaturePython)
  n = 2
  ref = O_element
FEATURE [App::DocumentObjectGroupPython] G4_URANIUM_OXIDE  # scripted group (container) (typed FeaturePython)
  Dunit = g/cm3
  Dvalue = 10.96
  Group = -> [U_element003,O_element100]
  conduct = 2
  density = 1
  expand = 3
  formula = G4_URANIUM_OXIDE
  name = G4_URANIUM_OXIDE
  specific = 4
FEATURE [App::DocumentObjectGroupPython] C_element119  label="C_element : 066"  # scripted group (container) (typed FeaturePython)
  n = 1
  ref = C_element
FEATURE [App::DocumentObjectGroupPython] H_element108  label="H_element : 058"  # scripted group (container) (typed FeaturePython)
  n = 4
  ref = H_element
FEATURE [App::DocumentObjectGroupPython] N_element046  label="N_element : 019"  # scripted group (container) (typed FeaturePython)
  n = 2
  ref = N_element
FEATURE [App::DocumentObjectGroupPython] O_element101  label="O_element : 055"  # scripted group (container) (typed FeaturePython)
  n = 1
  ref = O_element
FEATURE [App::DocumentObjectGroupPython] G4_UREA  # scripted group (container) (typed FeaturePython)
  Dunit = g/cm3
  Dvalue = 1.323
  Group = -> [C_element119,H_element108,N_element046,O_element101]
  conduct = 2
  density = 1
  expand = 3
  formula = G4_UREA
  name = G4_UREA
  specific = 4
FEATURE [App::DocumentObjectGroupPython] C_element120  label="C_element : 067"  # scripted group (container) (typed FeaturePython)
  n = 5
  ref = C_element
FEATURE [App::DocumentObjectGroupPython] H_element109  label="H_element : 059"  # scripted group (container) (typed FeaturePython)
  n = 11
  ref = H_element
FEATURE [App::DocumentObjectGroupPython] N_element047  label="N_element : 020"  # scripted group (container) (typed FeaturePython)
  n = 1
  ref = N_element
FEATURE [App::DocumentObjectGroupPython] O_element102  label="O_element : 056"  # scripted group (container) (typed FeaturePython)
  n = 2
  ref = O_element
FEATURE [App::DocumentObjectGroupPython] G4_VALINE  # scripted group (container) (typed FeaturePython)
  Dunit = g/cm3
  Dvalue = 1.23
  Group = -> [C_element120,H_element109,N_element047,O_element102]
  conduct = 2
  density = 1
  expand = 3
  formula = G4_VALINE
  name = G4_VALINE
  specific = 4
FEATURE [App::DocumentObjectGroupPython] H_element110  label="H_element : 0.009"  # scripted group (container) (typed FeaturePython)
  n = 0.009417
FEATURE [App::DocumentObjectGroupPython] C_element121  label="C_element : 0.281"  # scripted group (container) (typed FeaturePython)
  n = 0.280555
FEATURE [App::DocumentObjectGroupPython] F_element018  label="F_element : 0.710"  # scripted group (container) (typed FeaturePython)
  n = 0.710028
FEATURE [App::DocumentObjectGroupPython] G4_VITON  # scripted group (container) (typed FeaturePython)
  Dunit = g/cm3
  Dvalue = 1.8
  Group = -> [H_element110,C_element121,F_element018]
  conduct = 2
  density = 1
  expand = 3
  formula = G4_VITON
  name = G4_VITON
  specific = 4
FEATURE [App::DocumentObjectGroupPython] H_element111  label="H_element : 060"  # scripted group (container) (typed FeaturePython)
  n = 2
  ref = H_element
FEATURE [App::DocumentObjectGroupPython] O_element103  label="O_element : 057"  # scripted group (container) (typed FeaturePython)
  n = 1
  ref = O_element
FEATURE [App::DocumentObjectGroupPython] G4_WATER  # scripted group (container) (typed FeaturePython)
  Dunit = g/cm3
  Dvalue = 1
  Group = -> [H_element111,O_element103]
  conduct = 2
  density = 1
  expand = 3
  formula = G4_WATER
  name = G4_WATER
  specific = 4
FEATURE [App::DocumentObjectGroupPython] H_element112  label="H_element : 061"  # scripted group (container) (typed FeaturePython)
  n = 2
  ref = H_element
FEATURE [App::DocumentObjectGroupPython] O_element104  label="O_element : 058"  # scripted group (container) (typed FeaturePython)
  n = 1
  ref = O_element
FEATURE [App::DocumentObjectGroupPython] G4_WATER_VAPOR  # scripted group (container) (typed FeaturePython)
  Dunit = g/cm3
  Dvalue = 0.000756182
  Group = -> [H_element112,O_element104]
  conduct = 2
  density = 1
  expand = 3
  formula = G4_WATER_VAPOR
  name = G4_WATER_VAPOR
  specific = 4
FEATURE [App::DocumentObjectGroupPython] C_element122  label="C_element : 068"  # scripted group (container) (typed FeaturePython)
  n = 8
  ref = C_element
FEATURE [App::DocumentObjectGroupPython] H_element113  label="H_element : 062"  # scripted group (container) (typed FeaturePython)
  n = 10
  ref = H_element
FEATURE [App::DocumentObjectGroupPython] G4_XYLENE  # scripted group (container) (typed FeaturePython)
  Dunit = g/cm3
  Dvalue = 0.87
  Group = -> [C_element122,H_element113]
  conduct = 2
  density = 1
  expand = 3
  formula = G4_XYLENE
  name = G4_XYLENE
  specific = 4
FEATURE [App::DocumentObjectGroupPython] C_element123  label="C_element : 069"  # scripted group (container) (typed FeaturePython)
  n = 1
  ref = C_element
FEATURE [App::DocumentObjectGroupPython] G4_GRAPHITE  # scripted group (container) (typed FeaturePython)
  Dunit = g/cm3
  Dvalue = 2.21
  Group = -> [C_element123]
  conduct = 2
  density = 1
  expand = 3
  formula = G4_GRAPHITE
  name = G4_GRAPHITE
  specific = 4
FEATURE [App::DocumentObjectGroupPython] H_element114  label="H_element : 063"  # scripted group (container) (typed FeaturePython)
  n = 1
  ref = H_element
FEATURE [App::DocumentObjectGroupPython] G4_H  # scripted group (container) (typed FeaturePython)
  Dunit = g/cm3
  Dvalue = 8.3748e-05
  Group = -> [H_element114]
  conduct = 2
  density = 1
  expand = 3
  formula = H
  name = G4_H
  specific = 4
FEATURE [App::DocumentObjectGroupPython] He_element001  label="He_element : 1"  # scripted group (container) (typed FeaturePython)
  n = 1
  ref = He_element
FEATURE [App::DocumentObjectGroupPython] G4_He  # scripted group (container) (typed FeaturePython)
  Dunit = g/cm3
  Dvalue = 0.000166322
  Group = -> [He_element001]
  conduct = 2
  density = 1
  expand = 3
  formula = He
  name = G4_He
  specific = 4
FEATURE [App::DocumentObjectGroupPython] Li_element008  label="Li_element : 008"  # scripted group (container) (typed FeaturePython)
  n = 1
  ref = Li_element
FEATURE [App::DocumentObjectGroupPython] G4_Li  # scripted group (container) (typed FeaturePython)
  Dunit = g/cm3
  Dvalue = 0.534
  Group = -> [Li_element008]
  conduct = 2
  density = 1
  expand = 3
  formula = Li
  name = G4_Li
  specific = 4
FEATURE [App::DocumentObjectGroupPython] Be_element002  label="Be_element : 002"  # scripted group (container) (typed FeaturePython)
  n = 1
  ref = Be_element
FEATURE [App::DocumentObjectGroupPython] G4_Be  # scripted group (container) (typed FeaturePython)
  Dunit = g/cm3
  Dvalue = 1.848
  Group = -> [Be_element002]
  conduct = 2
  density = 1
  expand = 3
  formula = Be
  name = G4_Be
  specific = 4
FEATURE [App::DocumentObjectGroupPython] B_element007  label="B_element : 007"  # scripted group (container) (typed FeaturePython)
  n = 1
  ref = B_element
FEATURE [App::DocumentObjectGroupPython] G4_B  # scripted group (container) (typed FeaturePython)
  Dunit = g/cm3
  Dvalue = 2.37
  Group = -> [B_element007]
  conduct = 2
  density = 1
  expand = 3
  formula = B
  name = G4_B
  specific = 4
FEATURE [App::DocumentObjectGroupPython] C_element124  label="C_element : 070"  # scripted group (container) (typed FeaturePython)
  n = 1
  ref = C_element
FEATURE [App::DocumentObjectGroupPython] G4_C  # scripted group (container) (typed FeaturePython)
  Dunit = g/cm3
  Dvalue = 2
  Group = -> [C_element124]
  conduct = 2
  density = 1
  expand = 3
  formula = C
  name = G4_C
  specific = 4
FEATURE [App::DocumentObjectGroupPython] N_element048  label="N_element : 021"  # scripted group (container) (typed FeaturePython)
  n = 1
  ref = N_element
FEATURE [App::DocumentObjectGroupPython] G4_N  # scripted group (container) (typed FeaturePython)
  Dunit = g/cm3
  Dvalue = 0.0011652
  Group = -> [N_element048]
  conduct = 2
  density = 1
  expand = 3
  formula = N
  name = G4_N
  specific = 4
FEATURE [App::DocumentObjectGroupPython] O_element105  label="O_element : 059"  # scripted group (container) (typed FeaturePython)
  n = 1
  ref = O_element
FEATURE [App::DocumentObjectGroupPython] G4_O  # scripted group (container) (typed FeaturePython)
  Dunit = g/cm3
  Dvalue = 0.00133151
  Group = -> [O_element105]
  conduct = 2
  density = 1
  expand = 3
  formula = O
  name = G4_O
  specific = 4
FEATURE [App::DocumentObjectGroupPython] F_element019  label="F_element : 008"  # scripted group (container) (typed FeaturePython)
  n = 1
  ref = F_element
FEATURE [App::DocumentObjectGroupPython] G4_F  # scripted group (container) (typed FeaturePython)
  Dunit = g/cm3
  Dvalue = 0.00158029
  Group = -> [F_element019]
  conduct = 2
  density = 1
  expand = 3
  formula = F
  name = G4_F
  specific = 4
FEATURE [App::DocumentObjectGroupPython] Ne_element001  label="Ne_element : 1"  # scripted group (container) (typed FeaturePython)
  n = 1
  ref = Ne_element
FEATURE [App::DocumentObjectGroupPython] G4_Ne  # scripted group (container) (typed FeaturePython)
  Dunit = g/cm3
  Dvalue = 0.000838505
  Group = -> [Ne_element001]
  conduct = 2
  density = 1
  expand = 3
  formula = Ne
  name = G4_Ne
  specific = 4
FEATURE [App::DocumentObjectGroupPython] Na_element020  label="Na_element : 005"  # scripted group (container) (typed FeaturePython)
  n = 1
  ref = Na_element
FEATURE [App::DocumentObjectGroupPython] G4_Na  # scripted group (container) (typed FeaturePython)
  Dunit = g/cm3
  Dvalue = 0.971
  Group = -> [Na_element020]
  conduct = 2
  density = 1
  expand = 3
  formula = Na
  name = G4_Na
  specific = 4
FEATURE [App::DocumentObjectGroupPython] Mg_element011  label="Mg_element : 005"  # scripted group (container) (typed FeaturePython)
  n = 1
  ref = Mg_element
FEATURE [App::DocumentObjectGroupPython] G4_Mg  # scripted group (container) (typed FeaturePython)
  Dunit = g/cm3
  Dvalue = 1.74
  Group = -> [Mg_element011]
  conduct = 2
  density = 1
  expand = 3
  formula = Mg
  name = G4_Mg
  specific = 4
FEATURE [App::DocumentObjectGroupPython] Al_element004  label="Al_element : 1"  # scripted group (container) (typed FeaturePython)
  n = 1
  ref = Al_element
FEATURE [App::DocumentObjectGroupPython] G4_Al  # scripted group (container) (typed FeaturePython)
  Dunit = g/cm3
  Dvalue = 2.699
  Group = -> [Al_element004]
  conduct = 2
  density = 1
  expand = 3
  formula = Al
  name = G4_Al
  specific = 4
FEATURE [App::DocumentObjectGroupPython] Si_element007  label="Si_element : 002"  # scripted group (container) (typed FeaturePython)
  n = 1
  ref = Si_element
FEATURE [App::DocumentObjectGroupPython] G4_Si  # scripted group (container) (typed FeaturePython)
  Dunit = g/cm3
  Dvalue = 2.33
  Group = -> [Si_element007]
  conduct = 2
  density = 1
  expand = 3
  formula = Si
  name = G4_Si
  specific = 4
FEATURE [App::DocumentObjectGroupPython] P_element013  label="P_element : 002"  # scripted group (container) (typed FeaturePython)
  n = 1
  ref = P_element
FEATURE [App::DocumentObjectGroupPython] G4_P  # scripted group (container) (typed FeaturePython)
  Dunit = g/cm3
  Dvalue = 2.2
  Group = -> [P_element013]
  conduct = 2
  density = 1
  expand = 3
  formula = P
  name = G4_P
  specific = 4
FEATURE [App::DocumentObjectGroupPython] S_element023  label="S_element : 007"  # scripted group (container) (typed FeaturePython)
  n = 1
  ref = S_element
FEATURE [App::DocumentObjectGroupPython] G4_S  # scripted group (container) (typed FeaturePython)
  Dunit = g/cm3
  Dvalue = 2
  Group = -> [S_element023]
  conduct = 2
  density = 1
  expand = 3
  formula = S
  name = G4_S
  specific = 4
FEATURE [App::DocumentObjectGroupPython] Cl_element029  label="Cl_element : 015"  # scripted group (container) (typed FeaturePython)
  n = 1
  ref = Cl_element
FEATURE [App::DocumentObjectGroupPython] G4_Cl  # scripted group (container) (typed FeaturePython)
  Dunit = g/cm3
  Dvalue = 0.00299473
  Group = -> [Cl_element029]
  conduct = 2
  density = 1
  expand = 3
  formula = Cl
  name = G4_Cl
  specific = 4
FEATURE [App::DocumentObjectGroupPython] Ar_element002  label="Ar_element : 1"  # scripted group (container) (typed FeaturePython)
  n = 1
  ref = Ar_element
FEATURE [App::DocumentObjectGroupPython] G4_Ar  # scripted group (container) (typed FeaturePython)
  Dunit = g/cm3
  Dvalue = 0.00166201
  Group = -> [Ar_element002]
  conduct = 2
  density = 1
  expand = 3
  formula = Ar
  name = G4_Ar
  specific = 4
FEATURE [App::DocumentObjectGroupPython] K_element013  label="K_element : 003"  # scripted group (container) (typed FeaturePython)
  n = 1
  ref = K_element
FEATURE [App::DocumentObjectGroupPython] G4_K  # scripted group (container) (typed FeaturePython)
  Dunit = g/cm3
  Dvalue = 0.862
  Group = -> [K_element013]
  conduct = 2
  density = 1
  expand = 3
  formula = K
  name = G4_K
  specific = 4
FEATURE [App::DocumentObjectGroupPython] Ca_element014  label="Ca_element : 007"  # scripted group (container) (typed FeaturePython)
  n = 1
  ref = Ca_element
FEATURE [App::DocumentObjectGroupPython] G4_Ca  # scripted group (container) (typed FeaturePython)
  Dunit = g/cm3
  Dvalue = 1.55
  Group = -> [Ca_element014]
  conduct = 2
  density = 1
  expand = 3
  formula = Ca
  name = G4_Ca
  specific = 4
FEATURE [App::DocumentObjectGroupPython] Sc_element001  label="Sc_element : 1"  # scripted group (container) (typed FeaturePython)
  n = 1
  ref = Sc_element
FEATURE [App::DocumentObjectGroupPython] G4_Sc  # scripted group (container) (typed FeaturePython)
  Dunit = g/cm3
  Dvalue = 2.989
  Group = -> [Sc_element001]
  conduct = 2
  density = 1
  expand = 3
  formula = Sc
  name = G4_Sc
  specific = 4
FEATURE [App::DocumentObjectGroupPython] Ti_element004  label="Ti_element : 002"  # scripted group (container) (typed FeaturePython)
  n = 1
  ref = Ti_element
FEATURE [App::DocumentObjectGroupPython] G4_Ti  # scripted group (container) (typed FeaturePython)
  Dunit = g/cm3
  Dvalue = 4.54
  Group = -> [Ti_element004]
  conduct = 2
  density = 1
  expand = 3
  formula = Ti
  name = G4_Ti
  specific = 4
FEATURE [App::DocumentObjectGroupPython] V_element001  label="V_element : 1"  # scripted group (container) (typed FeaturePython)
  n = 1
  ref = V_element
FEATURE [App::DocumentObjectGroupPython] G4_V  # scripted group (container) (typed FeaturePython)
  Dunit = g/cm3
  Dvalue = 6.11
  Group = -> [V_element001]
  conduct = 2
  density = 1
  expand = 3
  formula = V
  name = G4_V
  specific = 4
FEATURE [App::DocumentObjectGroupPython] Cr_element001  label="Cr_element : 1"  # scripted group (container) (typed FeaturePython)
  n = 1
  ref = Cr_element
FEATURE [App::DocumentObjectGroupPython] G4_Cr  # scripted group (container) (typed FeaturePython)
  Dunit = g/cm3
  Dvalue = 7.18
  Group = -> [Cr_element001]
  conduct = 2
  density = 1
  expand = 3
  formula = Cr
  name = G4_Cr
  specific = 4
FEATURE [App::DocumentObjectGroupPython] Mn_element001  label="Mn_element : 1"  # scripted group (container) (typed FeaturePython)
  n = 1
  ref = Mn_element
FEATURE [App::DocumentObjectGroupPython] G4_Mn  # scripted group (container) (typed FeaturePython)
  Dunit = g/cm3
  Dvalue = 7.44
  Group = -> [Mn_element001]
  conduct = 2
  density = 1
  expand = 3
  formula = Mn
  name = G4_Mn
  specific = 4
FEATURE [App::DocumentObjectGroupPython] Fe_element007  label="Fe_element : 004"  # scripted group (container) (typed FeaturePython)
  n = 1
  ref = Fe_element
FEATURE [App::DocumentObjectGroupPython] G4_Fe  # scripted group (container) (typed FeaturePython)
  Dunit = g/cm3
  Dvalue = 7.874
  Group = -> [Fe_element007]
  conduct = 2
  density = 1
  expand = 3
  formula = Fe
  name = G4_Fe
  specific = 4
FEATURE [App::DocumentObjectGroupPython] Co_element001  label="Co_element : 1"  # scripted group (container) (typed FeaturePython)
  n = 1
  ref = Co_element
FEATURE [App::DocumentObjectGroupPython] G4_Co  # scripted group (container) (typed FeaturePython)
  Dunit = g/cm3
  Dvalue = 8.9
  Group = -> [Co_element001]
  conduct = 2
  density = 1
  expand = 3
  formula = Co
  name = G4_Co
  specific = 4
FEATURE [App::DocumentObjectGroupPython] Ni_element001  label="Ni_element : 1"  # scripted group (container) (typed FeaturePython)
  n = 1
  ref = Ni_element
FEATURE [App::DocumentObjectGroupPython] G4_Ni  # scripted group (container) (typed FeaturePython)
  Dunit = g/cm3
  Dvalue = 8.902
  Group = -> [Ni_element001]
  conduct = 2
  density = 1
  expand = 3
  formula = Ni
  name = G4_Ni
  specific = 4
FEATURE [App::DocumentObjectGroupPython] Cu_element001  label="Cu_element : 1"  # scripted group (container) (typed FeaturePython)
  n = 1
  ref = Cu_element
FEATURE [App::DocumentObjectGroupPython] G4_Cu  # scripted group (container) (typed FeaturePython)
  Dunit = g/cm3
  Dvalue = 8.96
  Group = -> [Cu_element001]
  conduct = 2
  density = 1
  expand = 3
  formula = Cu
  name = G4_Cu
  specific = 4
FEATURE [App::DocumentObjectGroupPython] Zn_element001  label="Zn_element : 1"  # scripted group (container) (typed FeaturePython)
  n = 1
  ref = Zn_element
FEATURE [App::DocumentObjectGroupPython] G4_Zn  # scripted group (container) (typed FeaturePython)
  Dunit = g/cm3
  Dvalue = 7.133
  Group = -> [Zn_element001]
  conduct = 2
  density = 1
  expand = 3
  formula = Zn
  name = G4_Zn
  specific = 4
FEATURE [App::DocumentObjectGroupPython] Ga_element002  label="Ga_element : 002"  # scripted group (container) (typed FeaturePython)
  n = 1
  ref = Ga_element
FEATURE [App::DocumentObjectGroupPython] G4_Ga  # scripted group (container) (typed FeaturePython)
  Dunit = g/cm3
  Dvalue = 5.904
  Group = -> [Ga_element002]
  conduct = 2
  density = 1
  expand = 3
  formula = Ga
  name = G4_Ga
  specific = 4
FEATURE [App::DocumentObjectGroupPython] Ge_element002  label="Ge_element : 1"  # scripted group (container) (typed FeaturePython)
  n = 1
  ref = Ge_element
FEATURE [App::DocumentObjectGroupPython] G4_Ge  # scripted group (container) (typed FeaturePython)
  Dunit = g/cm3
  Dvalue = 5.323
  Group = -> [Ge_element002]
  conduct = 2
  density = 1
  expand = 3
  formula = Ge
  name = G4_Ge
  specific = 4
FEATURE [App::DocumentObjectGroupPython] As_element003  label="As_element : 002"  # scripted group (container) (typed FeaturePython)
  n = 1
  ref = As_element
FEATURE [App::DocumentObjectGroupPython] G4_As  # scripted group (container) (typed FeaturePython)
  Dunit = g/cm3
  Dvalue = 5.73
  Group = -> [As_element003]
  conduct = 2
  density = 1
  expand = 3
  formula = As
  name = G4_As
  specific = 4
FEATURE [App::DocumentObjectGroupPython] Se_element001  label="Se_element : 1"  # scripted group (container) (typed FeaturePython)
  n = 1
  ref = Se_element
FEATURE [App::DocumentObjectGroupPython] G4_Se  # scripted group (container) (typed FeaturePython)
  Dunit = g/cm3
  Dvalue = 4.5
  Group = -> [Se_element001]
  conduct = 2
  density = 1
  expand = 3
  formula = Se
  name = G4_Se
  specific = 4
FEATURE [App::DocumentObjectGroupPython] Br_element007  label="Br_element : 004"  # scripted group (container) (typed FeaturePython)
  n = 1
  ref = Br_element
FEATURE [App::DocumentObjectGroupPython] G4_Br  # scripted group (container) (typed FeaturePython)
  Dunit = g/cm3
  Dvalue = 0.0070721
  Group = -> [Br_element007]
  conduct = 2
  density = 1
  expand = 3
  formula = Br
  name = G4_Br
  specific = 4
FEATURE [App::DocumentObjectGroupPython] Kr_element001  label="Kr_element : 1"  # scripted group (container) (typed FeaturePython)
  n = 1
  ref = Kr_element
FEATURE [App::DocumentObjectGroupPython] G4_Kr  # scripted group (container) (typed FeaturePython)
  Dunit = g/cm3
  Dvalue = 0.00347832
  Group = -> [Kr_element001]
  conduct = 2
  density = 1
  expand = 3
  formula = Kr
  name = G4_Kr
  specific = 4
FEATURE [App::DocumentObjectGroupPython] Rb_element001  label="Rb_element : 1"  # scripted group (container) (typed FeaturePython)
  n = 1
  ref = Rb_element
FEATURE [App::DocumentObjectGroupPython] G4_Rb  # scripted group (container) (typed FeaturePython)
  Dunit = g/cm3
  Dvalue = 1.532
  Group = -> [Rb_element001]
  conduct = 2
  density = 1
  expand = 3
  formula = Rb
  name = G4_Rb
  specific = 4
FEATURE [App::DocumentObjectGroupPython] Sr_element001  label="Sr_element : 1"  # scripted group (container) (typed FeaturePython)
  n = 1
  ref = Sr_element
FEATURE [App::DocumentObjectGroupPython] G4_Sr  # scripted group (container) (typed FeaturePython)
  Dunit = g/cm3
  Dvalue = 2.54
  Group = -> [Sr_element001]
  conduct = 2
  density = 1
  expand = 3
  formula = Sr
  name = G4_Sr
  specific = 4
FEATURE [App::DocumentObjectGroupPython] Y_element001  label="Y_element : 1"  # scripted group (container) (typed FeaturePython)
  n = 1
  ref = Y_element
FEATURE [App::DocumentObjectGroupPython] G4_Y  # scripted group (container) (typed FeaturePython)
  Dunit = g/cm3
  Dvalue = 4.469
  Group = -> [Y_element001]
  conduct = 2
  density = 1
  expand = 3
  formula = Y
  name = G4_Y
  specific = 4
FEATURE [App::DocumentObjectGroupPython] Zr_element001  label="Zr_element : 1"  # scripted group (container) (typed FeaturePython)
  n = 1
  ref = Zr_element
FEATURE [App::DocumentObjectGroupPython] G4_Zr  # scripted group (container) (typed FeaturePython)
  Dunit = g/cm3
  Dvalue = 6.506
  Group = -> [Zr_element001]
  conduct = 2
  density = 1
  expand = 3
  formula = Zr
  name = G4_Zr
  specific = 4
FEATURE [App::DocumentObjectGroupPython] Nb_element001  label="Nb_element : 1"  # scripted group (container) (typed FeaturePython)
  n = 1
  ref = Nb_element
FEATURE [App::DocumentObjectGroupPython] G4_Nb  # scripted group (container) (typed FeaturePython)
  Dunit = g/cm3
  Dvalue = 8.57
  Group = -> [Nb_element001]
  conduct = 2
  density = 1
  expand = 3
  formula = Nb
  name = G4_Nb
  specific = 4
FEATURE [App::DocumentObjectGroupPython] Mo_element001  label="Mo_element : 1"  # scripted group (container) (typed FeaturePython)
  n = 1
  ref = Mo_element
FEATURE [App::DocumentObjectGroupPython] G4_Mo  # scripted group (container) (typed FeaturePython)
  Dunit = g/cm3
  Dvalue = 10.22
  Group = -> [Mo_element001]
  conduct = 2
  density = 1
  expand = 3
  formula = Mo
  name = G4_Mo
  specific = 4
FEATURE [App::DocumentObjectGroupPython] Tc_element001  label="Tc_element : 1"  # scripted group (container) (typed FeaturePython)
  n = 1
  ref = Tc_element
FEATURE [App::DocumentObjectGroupPython] G4_Tc  # scripted group (container) (typed FeaturePython)
  Dunit = g/cm3
  Dvalue = 11.5
  Group = -> [Tc_element001]
  conduct = 2
  density = 1
  expand = 3
  formula = Tc
  name = G4_Tc
  specific = 4
FEATURE [App::DocumentObjectGroupPython] Ru_element001  label="Ru_element : 1"  # scripted group (container) (typed FeaturePython)
  n = 1
  ref = Ru_element
FEATURE [App::DocumentObjectGroupPython] G4_Ru  # scripted group (container) (typed FeaturePython)
  Dunit = g/cm3
  Dvalue = 12.41
  Group = -> [Ru_element001]
  conduct = 2
  density = 1
  expand = 3
  formula = Ru
  name = G4_Ru
  specific = 4
FEATURE [App::DocumentObjectGroupPython] Rh_element001  label="Rh_element : 1"  # scripted group (container) (typed FeaturePython)
  n = 1
  ref = Rh_element
FEATURE [App::DocumentObjectGroupPython] G4_Rh  # scripted group (container) (typed FeaturePython)
  Dunit = g/cm3
  Dvalue = 12.41
  Group = -> [Rh_element001]
  conduct = 2
  density = 1
  expand = 3
  formula = Rh
  name = G4_Rh
  specific = 4
FEATURE [App::DocumentObjectGroupPython] Pd_element001  label="Pd_element : 1"  # scripted group (container) (typed FeaturePython)
  n = 1
  ref = Pd_element
FEATURE [App::DocumentObjectGroupPython] G4_Pd  # scripted group (container) (typed FeaturePython)
  Dunit = g/cm3
  Dvalue = 12.02
  Group = -> [Pd_element001]
  conduct = 2
  density = 1
  expand = 3
  formula = Pd
  name = G4_Pd
  specific = 4
FEATURE [App::DocumentObjectGroupPython] Ag_element006  label="Ag_element : 004"  # scripted group (container) (typed FeaturePython)
  n = 1
  ref = Ag_element
FEATURE [App::DocumentObjectGroupPython] G4_Ag  # scripted group (container) (typed FeaturePython)
  Dunit = g/cm3
  Dvalue = 10.5
  Group = -> [Ag_element006]
  conduct = 2
  density = 1
  expand = 3
  formula = Ag
  name = G4_Ag
  specific = 4
FEATURE [App::DocumentObjectGroupPython] Cd_element003  label="Cd_element : 003"  # scripted group (container) (typed FeaturePython)
  n = 1
  ref = Cd_element
FEATURE [App::DocumentObjectGroupPython] G4_Cd  # scripted group (container) (typed FeaturePython)
  Dunit = g/cm3
  Dvalue = 8.65
  Group = -> [Cd_element003]
  conduct = 2
  density = 1
  expand = 3
  formula = Cd
  name = G4_Cd
  specific = 4
FEATURE [App::DocumentObjectGroupPython] In_element001  label="In_element : 1"  # scripted group (container) (typed FeaturePython)
  n = 1
  ref = In_element
FEATURE [App::DocumentObjectGroupPython] G4_In  # scripted group (container) (typed FeaturePython)
  Dunit = g/cm3
  Dvalue = 7.31
  Group = -> [In_element001]
  conduct = 2
  density = 1
  expand = 3
  formula = In
  name = G4_In
  specific = 4
FEATURE [App::DocumentObjectGroupPython] Sn_element001  label="Sn_element : 1"  # scripted group (container) (typed FeaturePython)
  n = 1
  ref = Sn_element
FEATURE [App::DocumentObjectGroupPython] G4_Sn  # scripted group (container) (typed FeaturePython)
  Dunit = g/cm3
  Dvalue = 7.31
  Group = -> [Sn_element001]
  conduct = 2
  density = 1
  expand = 3
  formula = Sn
  name = G4_Sn
  specific = 4
FEATURE [App::DocumentObjectGroupPython] Sb_element001  label="Sb_element : 1"  # scripted group (container) (typed FeaturePython)
  n = 1
  ref = Sb_element
FEATURE [App::DocumentObjectGroupPython] G4_Sb  # scripted group (container) (typed FeaturePython)
  Dunit = g/cm3
  Dvalue = 6.691
  Group = -> [Sb_element001]
  conduct = 2
  density = 1
  expand = 3
  formula = Sb
  name = G4_Sb
  specific = 4
FEATURE [App::DocumentObjectGroupPython] Te_element002  label="Te_element : 002"  # scripted group (container) (typed FeaturePython)
  n = 1
  ref = Te_element
FEATURE [App::DocumentObjectGroupPython] G4_Te  # scripted group (container) (typed FeaturePython)
  Dunit = g/cm3
  Dvalue = 6.24
  Group = -> [Te_element002]
  conduct = 2
  density = 1
  expand = 3
  formula = Te
  name = G4_Te
  specific = 4
FEATURE [App::DocumentObjectGroupPython] I_element010  label="I_element : 006"  # scripted group (container) (typed FeaturePython)
  n = 1
  ref = I_element
FEATURE [App::DocumentObjectGroupPython] G4_I  # scripted group (container) (typed FeaturePython)
  Dunit = g/cm3
  Dvalue = 4.93
  Group = -> [I_element010]
  conduct = 2
  density = 1
  expand = 3
  formula = I
  name = G4_I
  specific = 4
FEATURE [App::DocumentObjectGroupPython] Xe_element001  label="Xe_element : 1"  # scripted group (container) (typed FeaturePython)
  n = 1
  ref = Xe_element
FEATURE [App::DocumentObjectGroupPython] G4_Xe  # scripted group (container) (typed FeaturePython)
  Dunit = g/cm3
  Dvalue = 0.00548536
  Group = -> [Xe_element001]
  conduct = 2
  density = 1
  expand = 3
  formula = Xe
  name = G4_Xe
  specific = 4
FEATURE [App::DocumentObjectGroupPython] Cs_element003  label="Cs_element : 003"  # scripted group (container) (typed FeaturePython)
  n = 1
  ref = Cs_element
FEATURE [App::DocumentObjectGroupPython] G4_Cs  # scripted group (container) (typed FeaturePython)
  Dunit = g/cm3
  Dvalue = 1.873
  Group = -> [Cs_element003]
  conduct = 2
  density = 1
  expand = 3
  formula = Cs
  name = G4_Cs
  specific = 4
FEATURE [App::DocumentObjectGroupPython] Ba_element003  label="Ba_element : 003"  # scripted group (container) (typed FeaturePython)
  n = 1
  ref = Ba_element
FEATURE [App::DocumentObjectGroupPython] G4_Ba  # scripted group (container) (typed FeaturePython)
  Dunit = g/cm3
  Dvalue = 3.5
  Group = -> [Ba_element003]
  conduct = 2
  density = 1
  expand = 3
  formula = Ba
  name = G4_Ba
  specific = 4
FEATURE [App::DocumentObjectGroupPython] La_element003  label="La_element : 003"  # scripted group (container) (typed FeaturePython)
  n = 1
  ref = La_element
FEATURE [App::DocumentObjectGroupPython] G4_La  # scripted group (container) (typed FeaturePython)
  Dunit = g/cm3
  Dvalue = 6.154
  Group = -> [La_element003]
  conduct = 2
  density = 1
  expand = 3
  formula = La
  name = G4_La
  specific = 4
FEATURE [App::DocumentObjectGroupPython] Ce_element002  label="Ce_element : 1"  # scripted group (container) (typed FeaturePython)
  n = 1
  ref = Ce_element
FEATURE [App::DocumentObjectGroupPython] G4_Ce  # scripted group (container) (typed FeaturePython)
  Dunit = g/cm3
  Dvalue = 6.657
  Group = -> [Ce_element002]
  conduct = 2
  density = 1
  expand = 3
  formula = Ce
  name = G4_Ce
  specific = 4
FEATURE [App::DocumentObjectGroupPython] Pr_element001  label="Pr_element : 1"  # scripted group (container) (typed FeaturePython)
  n = 1
  ref = Pr_element
FEATURE [App::DocumentObjectGroupPython] G4_Pr  # scripted group (container) (typed FeaturePython)
  Dunit = g/cm3
  Dvalue = 6.71
  Group = -> [Pr_element001]
  conduct = 2
  density = 1
  expand = 3
  formula = Pr
  name = G4_Pr
  specific = 4
FEATURE [App::DocumentObjectGroupPython] Nd_element001  label="Nd_element : 1"  # scripted group (container) (typed FeaturePython)
  n = 1
  ref = Nd_element
FEATURE [App::DocumentObjectGroupPython] G4_Nd  # scripted group (container) (typed FeaturePython)
  Dunit = g/cm3
  Dvalue = 6.9
  Group = -> [Nd_element001]
  conduct = 2
  density = 1
  expand = 3
  formula = Nd
  name = G4_Nd
  specific = 4
FEATURE [App::DocumentObjectGroupPython] Pm_element001  label="Pm_element : 1"  # scripted group (container) (typed FeaturePython)
  n = 1
  ref = Pm_element
FEATURE [App::DocumentObjectGroupPython] G4_Pm  # scripted group (container) (typed FeaturePython)
  Dunit = g/cm3
  Dvalue = 7.22
  Group = -> [Pm_element001]
  conduct = 2
  density = 1
  expand = 3
  formula = Pm
  name = G4_Pm
  specific = 4
FEATURE [App::DocumentObjectGroupPython] Sm_element001  label="Sm_element : 1"  # scripted group (container) (typed FeaturePython)
  n = 1
  ref = Sm_element
FEATURE [App::DocumentObjectGroupPython] G4_Sm  # scripted group (container) (typed FeaturePython)
  Dunit = g/cm3
  Dvalue = 7.46
  Group = -> [Sm_element001]
  conduct = 2
  density = 1
  expand = 3
  formula = Sm
  name = G4_Sm
  specific = 4
FEATURE [App::DocumentObjectGroupPython] Eu_element001  label="Eu_element : 1"  # scripted group (container) (typed FeaturePython)
  n = 1
  ref = Eu_element
FEATURE [App::DocumentObjectGroupPython] G4_Eu  # scripted group (container) (typed FeaturePython)
  Dunit = g/cm3
  Dvalue = 5.243
  Group = -> [Eu_element001]
  conduct = 2
  density = 1
  expand = 3
  formula = Eu
  name = G4_Eu
  specific = 4
FEATURE [App::DocumentObjectGroupPython] Gd_element002  label="Gd_element : 1"  # scripted group (container) (typed FeaturePython)
  n = 1
  ref = Gd_element
FEATURE [App::DocumentObjectGroupPython] G4_Gd  # scripted group (container) (typed FeaturePython)
  Dunit = g/cm3
  Dvalue = 7.9004
  Group = -> [Gd_element002]
  conduct = 2
  density = 1
  expand = 3
  formula = Gd
  name = G4_Gd
  specific = 4
FEATURE [App::DocumentObjectGroupPython] Tb_element001  label="Tb_element : 1"  # scripted group (container) (typed FeaturePython)
  n = 1
  ref = Tb_element
FEATURE [App::DocumentObjectGroupPython] G4_Tb  # scripted group (container) (typed FeaturePython)
  Dunit = g/cm3
  Dvalue = 8.229
  Group = -> [Tb_element001]
  conduct = 2
  density = 1
  expand = 3
  formula = Tb
  name = G4_Tb
  specific = 4
FEATURE [App::DocumentObjectGroupPython] Dy_element001  label="Dy_element : 1"  # scripted group (container) (typed FeaturePython)
  n = 1
  ref = Dy_element
FEATURE [App::DocumentObjectGroupPython] G4_Dy  # scripted group (container) (typed FeaturePython)
  Dunit = g/cm3
  Dvalue = 8.55
  Group = -> [Dy_element001]
  conduct = 2
  density = 1
  expand = 3
  formula = Dy
  name = G4_Dy
  specific = 4
FEATURE [App::DocumentObjectGroupPython] Ho_element001  label="Ho_element : 1"  # scripted group (container) (typed FeaturePython)
  n = 1
  ref = Ho_element
FEATURE [App::DocumentObjectGroupPython] G4_Ho  # scripted group (container) (typed FeaturePython)
  Dunit = g/cm3
  Dvalue = 8.795
  Group = -> [Ho_element001]
  conduct = 2
  density = 1
  expand = 3
  formula = Ho
  name = G4_Ho
  specific = 4
FEATURE [App::DocumentObjectGroupPython] Er_element001  label="Er_element : 1"  # scripted group (container) (typed FeaturePython)
  n = 1
  ref = Er_element
FEATURE [App::DocumentObjectGroupPython] G4_Er  # scripted group (container) (typed FeaturePython)
  Dunit = g/cm3
  Dvalue = 9.066
  Group = -> [Er_element001]
  conduct = 2
  density = 1
  expand = 3
  formula = Er
  name = G4_Er
  specific = 4
FEATURE [App::DocumentObjectGroupPython] Tm_element001  label="Tm_element : 1"  # scripted group (container) (typed FeaturePython)
  n = 1
  ref = Tm_element
FEATURE [App::DocumentObjectGroupPython] G4_Tm  # scripted group (container) (typed FeaturePython)
  Dunit = g/cm3
  Dvalue = 9.321
  Group = -> [Tm_element001]
  conduct = 2
  density = 1
  expand = 3
  formula = Tm
  name = G4_Tm
  specific = 4
FEATURE [App::DocumentObjectGroupPython] Yb_element001  label="Yb_element : 1"  # scripted group (container) (typed FeaturePython)
  n = 1
  ref = Yb_element
FEATURE [App::DocumentObjectGroupPython] G4_Yb  # scripted group (container) (typed FeaturePython)
  Dunit = g/cm3
  Dvalue = 6.73
  Group = -> [Yb_element001]
  conduct = 2
  density = 1
  expand = 3
  formula = Yb
  name = G4_Yb
  specific = 4
FEATURE [App::DocumentObjectGroupPython] Lu_element001  label="Lu_element : 1"  # scripted group (container) (typed FeaturePython)
  n = 1
  ref = Lu_element
FEATURE [App::DocumentObjectGroupPython] G4_Lu  # scripted group (container) (typed FeaturePython)
  Dunit = g/cm3
  Dvalue = 9.84
  Group = -> [Lu_element001]
  conduct = 2
  density = 1
  expand = 3
  formula = Lu
  name = G4_Lu
  specific = 4
FEATURE [App::DocumentObjectGroupPython] Hf_element001  label="Hf_element : 1"  # scripted group (container) (typed FeaturePython)
  n = 1
  ref = Hf_element
FEATURE [App::DocumentObjectGroupPython] G4_Hf  # scripted group (container) (typed FeaturePython)
  Dunit = g/cm3
  Dvalue = 13.31
  Group = -> [Hf_element001]
  conduct = 2
  density = 1
  expand = 3
  formula = Hf
  name = G4_Hf
  specific = 4
FEATURE [App::DocumentObjectGroupPython] Ta_element001  label="Ta_element : 1"  # scripted group (container) (typed FeaturePython)
  n = 1
  ref = Ta_element
FEATURE [App::DocumentObjectGroupPython] G4_Ta  # scripted group (container) (typed FeaturePython)
  Dunit = g/cm3
  Dvalue = 16.654
  Group = -> [Ta_element001]
  conduct = 2
  density = 1
  expand = 3
  formula = Ta
  name = G4_Ta
  specific = 4
FEATURE [App::DocumentObjectGroupPython] W_element004  label="W_element : 004"  # scripted group (container) (typed FeaturePython)
  n = 1
  ref = W_element
FEATURE [App::DocumentObjectGroupPython] G4_W  # scripted group (container) (typed FeaturePython)
  Dunit = g/cm3
  Dvalue = 19.3
  Group = -> [W_element004]
  conduct = 2
  density = 1
  expand = 3
  formula = W
  name = G4_W
  specific = 4
FEATURE [App::DocumentObjectGroupPython] Re_element001  label="Re_element : 1"  # scripted group (container) (typed FeaturePython)
  n = 1
  ref = Re_element
FEATURE [App::DocumentObjectGroupPython] G4_Re  # scripted group (container) (typed FeaturePython)
  Dunit = g/cm3
  Dvalue = 21.02
  Group = -> [Re_element001]
  conduct = 2
  density = 1
  expand = 3
  formula = Re
  name = G4_Re
  specific = 4
FEATURE [App::DocumentObjectGroupPython] Os_element001  label="Os_element : 1"  # scripted group (container) (typed FeaturePython)
  n = 1
  ref = Os_element
FEATURE [App::DocumentObjectGroupPython] G4_Os  # scripted group (container) (typed FeaturePython)
  Dunit = g/cm3
  Dvalue = 22.57
  Group = -> [Os_element001]
  conduct = 2
  density = 1
  expand = 3
  formula = Os
  name = G4_Os
  specific = 4
FEATURE [App::DocumentObjectGroupPython] Ir_element001  label="Ir_element : 1"  # scripted group (container) (typed FeaturePython)
  n = 1
  ref = Ir_element
FEATURE [App::DocumentObjectGroupPython] G4_Ir  # scripted group (container) (typed FeaturePython)
  Dunit = g/cm3
  Dvalue = 22.42
  Group = -> [Ir_element001]
  conduct = 2
  density = 1
  expand = 3
  formula = Ir
  name = G4_Ir
  specific = 4
FEATURE [App::DocumentObjectGroupPython] Pt_element001  label="Pt_element : 1"  # scripted group (container) (typed FeaturePython)
  n = 1
  ref = Pt_element
FEATURE [App::DocumentObjectGroupPython] G4_Pt  # scripted group (container) (typed FeaturePython)
  Dunit = g/cm3
  Dvalue = 21.45
  Group = -> [Pt_element001]
  conduct = 2
  density = 1
  expand = 3
  formula = Pt
  name = G4_Pt
  specific = 4
FEATURE [App::DocumentObjectGroupPython] Au_element001  label="Au_element : 1"  # scripted group (container) (typed FeaturePython)
  n = 1
  ref = Au_element
FEATURE [App::DocumentObjectGroupPython] G4_Au  # scripted group (container) (typed FeaturePython)
  Dunit = g/cm3
  Dvalue = 19.32
  Group = -> [Au_element001]
  conduct = 2
  density = 1
  expand = 3
  formula = Au
  name = G4_Au
  specific = 4
FEATURE [App::DocumentObjectGroupPython] Hg_element002  label="Hg_element : 002"  # scripted group (container) (typed FeaturePython)
  n = 1
  ref = Hg_element
FEATURE [App::DocumentObjectGroupPython] G4_Hg  # scripted group (container) (typed FeaturePython)
  Dunit = g/cm3
  Dvalue = 13.546
  Group = -> [Hg_element002]
  conduct = 2
  density = 1
  expand = 3
  formula = Hg
  name = G4_Hg
  specific = 4
FEATURE [App::DocumentObjectGroupPython] Tl_element002  label="Tl_element : 002"  # scripted group (container) (typed FeaturePython)
  n = 1
  ref = Tl_element
FEATURE [App::DocumentObjectGroupPython] G4_Tl  # scripted group (container) (typed FeaturePython)
  Dunit = g/cm3
  Dvalue = 11.72
  Group = -> [Tl_element002]
  conduct = 2
  density = 1
  expand = 3
  formula = Tl
  name = G4_Tl
  specific = 4
FEATURE [App::DocumentObjectGroupPython] Pb_element003  label="Pb_element : 1"  # scripted group (container) (typed FeaturePython)
  n = 1
  ref = Pb_element
FEATURE [App::DocumentObjectGroupPython] G4_Pb  # scripted group (container) (typed FeaturePython)
  Dunit = g/cm3
  Dvalue = 11.35
  Group = -> [Pb_element003]
  conduct = 2
  density = 1
  expand = 3
  formula = Pb
  name = G4_Pb
  specific = 4
FEATURE [App::DocumentObjectGroupPython] Bi_element002  label="Bi_element : 1"  # scripted group (container) (typed FeaturePython)
  n = 1
  ref = Bi_element
FEATURE [App::DocumentObjectGroupPython] G4_Bi  # scripted group (container) (typed FeaturePython)
  Dunit = g/cm3
  Dvalue = 9.747
  Group = -> [Bi_element002]
  conduct = 2
  density = 1
  expand = 3
  formula = Bi
  name = G4_Bi
  specific = 4
FEATURE [App::DocumentObjectGroupPython] Po_element001  label="Po_element : 1"  # scripted group (container) (typed FeaturePython)
  n = 1
  ref = Po_element
FEATURE [App::DocumentObjectGroupPython] G4_Po  # scripted group (container) (typed FeaturePython)
  Dunit = g/cm3
  Dvalue = 9.32
  Group = -> [Po_element001]
  conduct = 2
  density = 1
  expand = 3
  formula = Po
  name = G4_Po
  specific = 4
FEATURE [App::DocumentObjectGroupPython] At_element001  label="At_element : 1"  # scripted group (container) (typed FeaturePython)
  n = 1
  ref = At_element
FEATURE [App::DocumentObjectGroupPython] G4_At  # scripted group (container) (typed FeaturePython)
  Dunit = g/cm3
  Dvalue = 9.32
  Group = -> [At_element001]
  conduct = 2
  density = 1
  expand = 3
  formula = At
  name = G4_At
  specific = 4
FEATURE [App::DocumentObjectGroupPython] Rn_element001  label="Rn_element : 1"  # scripted group (container) (typed FeaturePython)
  n = 1
  ref = Rn_element
FEATURE [App::DocumentObjectGroupPython] G4_Rn  # scripted group (container) (typed FeaturePython)
  Dunit = g/cm3
  Dvalue = 0.00900662
  Group = -> [Rn_element001]
  conduct = 2
  density = 1
  expand = 3
  formula = Rn
  name = G4_Rn
  specific = 4
FEATURE [App::DocumentObjectGroupPython] Fr_element001  label="Fr_element : 1"  # scripted group (container) (typed FeaturePython)
  n = 1
  ref = Fr_element
FEATURE [App::DocumentObjectGroupPython] G4_Fr  # scripted group (container) (typed FeaturePython)
  Dunit = g/cm3
  Dvalue = 1
  Group = -> [Fr_element001]
  conduct = 2
  density = 1
  expand = 3
  formula = Fr
  name = G4_Fr
  specific = 4
FEATURE [App::DocumentObjectGroupPython] Ra_element001  label="Ra_element : 1"  # scripted group (container) (typed FeaturePython)
  n = 1
  ref = Ra_element
FEATURE [App::DocumentObjectGroupPython] G4_Ra  # scripted group (container) (typed FeaturePython)
  Dunit = g/cm3
  Dvalue = 5
  Group = -> [Ra_element001]
  conduct = 2
  density = 1
  expand = 3
  formula = Ra
  name = G4_Ra
  specific = 4
FEATURE [App::DocumentObjectGroupPython] Ac_element001  label="Ac_element : 1"  # scripted group (container) (typed FeaturePython)
  n = 1
  ref = Ac_element
FEATURE [App::DocumentObjectGroupPython] G4_Ac  # scripted group (container) (typed FeaturePython)
  Dunit = g/cm3
  Dvalue = 10.07
  Group = -> [Ac_element001]
  conduct = 2
  density = 1
  expand = 3
  formula = Ac
  name = G4_Ac
  specific = 4
FEATURE [App::DocumentObjectGroupPython] Th_element001  label="Th_element : 1"  # scripted group (container) (typed FeaturePython)
  n = 1
  ref = Th_element
FEATURE [App::DocumentObjectGroupPython] G4_Th  # scripted group (container) (typed FeaturePython)
  Dunit = g/cm3
  Dvalue = 11.72
  Group = -> [Th_element001]
  conduct = 2
  density = 1
  expand = 3
  formula = Th
  name = G4_Th
  specific = 4
FEATURE [App::DocumentObjectGroupPython] Pa_element001  label="Pa_element : 1"  # scripted group (container) (typed FeaturePython)
  n = 1
  ref = Pa_element
FEATURE [App::DocumentObjectGroupPython] G4_Pa  # scripted group (container) (typed FeaturePython)
  Dunit = g/cm3
  Dvalue = 15.37
  Group = -> [Pa_element001]
  conduct = 2
  density = 1
  expand = 3
  formula = Pa
  name = G4_Pa
  specific = 4
FEATURE [App::DocumentObjectGroupPython] U_element004  label="U_element : 004"  # scripted group (container) (typed FeaturePython)
  n = 1
  ref = U_element
FEATURE [App::DocumentObjectGroupPython] G4_U  # scripted group (container) (typed FeaturePython)
  Dunit = g/cm3
  Dvalue = 18.95
  Group = -> [U_element004]
  conduct = 2
  density = 1
  expand = 3
  formula = U
  name = G4_U
  specific = 4
FEATURE [App::DocumentObjectGroupPython] Np_element001  label="Np_element : 1"  # scripted group (container) (typed FeaturePython)
  n = 1
  ref = Np_element
FEATURE [App::DocumentObjectGroupPython] G4_Np  # scripted group (container) (typed FeaturePython)
  Dunit = g/cm3
  Dvalue = 20.25
  Group = -> [Np_element001]
  conduct = 2
  density = 1
  expand = 3
  formula = Np
  name = G4_Np
  specific = 4
FEATURE [App::DocumentObjectGroupPython] Pu_element002  label="Pu_element : 002"  # scripted group (container) (typed FeaturePython)
  n = 1
  ref = Pu_element
FEATURE [App::DocumentObjectGroupPython] G4_Pu  # scripted group (container) (typed FeaturePython)
  Dunit = g/cm3
  Dvalue = 19.84
  Group = -> [Pu_element002]
  conduct = 2
  density = 1
  expand = 3
  formula = Pu
  name = G4_Pu
  specific = 4
FEATURE [App::DocumentObjectGroupPython] Am_element001  label="Am_element : 1"  # scripted group (container) (typed FeaturePython)
  n = 1
  ref = Am_element
FEATURE [App::DocumentObjectGroupPython] G4_Am  # scripted group (container) (typed FeaturePython)
  Dunit = g/cm3
  Dvalue = 13.67
  Group = -> [Am_element001]
  conduct = 2
  density = 1
  expand = 3
  formula = Am
  name = G4_Am
  specific = 4
FEATURE [App::DocumentObjectGroupPython] Cm_element001  label="Cm_element : 1"  # scripted group (container) (typed FeaturePython)
  n = 1
  ref = Cm_element
FEATURE [App::DocumentObjectGroupPython] G4_Cm  # scripted group (container) (typed FeaturePython)
  Dunit = g/cm3
  Dvalue = 13.51
  Group = -> [Cm_element001]
  conduct = 2
  density = 1
  expand = 3
  formula = Cm
  name = G4_Cm
  specific = 4
FEATURE [App::DocumentObjectGroupPython] Bk_element001  label="Bk_element : 1"  # scripted group (container) (typed FeaturePython)
  n = 1
  ref = Bk_element
FEATURE [App::DocumentObjectGroupPython] G4_Bk  # scripted group (container) (typed FeaturePython)
  Dunit = g/cm3
  Dvalue = 14
  Group = -> [Bk_element001]
  conduct = 2
  density = 1
  expand = 3
  formula = Bk
  name = G4_Bk
  specific = 4
FEATURE [App::DocumentObjectGroupPython] Cf_element001  label="Cf_element : 1"  # scripted group (container) (typed FeaturePython)
  n = 1
  ref = Cf_element
FEATURE [App::DocumentObjectGroupPython] G4_Cf  # scripted group (container) (typed FeaturePython)
  Dunit = g/cm3
  Dvalue = 10
  Group = -> [Cf_element001]
  conduct = 2
  density = 1
  expand = 3
  formula = Cf
  name = G4_Cf
  specific = 4
FEATURE [App::DocumentObjectGroupPython] G4Materials  # scripted group (container) (typed FeaturePython)
  Group = -> [G4_A_150_TISSUE,G4_ACETONE,G4_ACETYLENE,G4_ADENINE,G4_ADIPOSE_TISSUE_ICRP,G4_AIR,G4_ALANINE,G4_ALUMINUM_OXIDE,G4_AMBER,G4_AMMONIA,G4_ANILINE,G4_ANTHRACENE,G4_B_100_BONE,G4_BAKELITE,G4_BARIUM_FLUORIDE,G4_BARIUM_SULFATE,G4_BENZENE,G4_BERYLLIUM_OXIDE,G4_BGO,G4_BLOOD_ICRP,G4_BONE_COMPACT_ICRU,G4_BONE_CORTICAL_ICRP,G4_BORON_CARBIDE,G4_BORON_OXIDE,G4_BRAIN_ICRP,G4_BUTANE,G4_N_BUTYL_ALCOHOL,G4_C_552,+251 more]
FEATURE [App::DocumentObjectGroupPython] Geant4  # scripted group (container) (typed FeaturePython)
  Group = -> [G4Isotopes,G4Elements,G4Materials]
FEATURE [Part::FeaturePython] GDMLBox_WorldBox  # WARN: FeaturePython — macro-defined, semantics opaque (R4)
  lunit = 2
  material = 5
  x = 100
  y = 100
  z = 20
FEATURE [Sketcher::SketchObject] Sketch
  FullyConstrained = true
  MapMode = 2
  sketch-geometry (1):
    g0: Circle CenterX=0 CenterY=0 CenterZ=0 NormalX=0 NormalY=0 NormalZ=1 AngleXU=0 Radius=2
  constraints (2):
    c: Radius(g0) = 2
    c: Coincident(g0,g-1)
FEATURE [Part::Extrusion] Extrude
  Base = -> Sketch
  Dir = (0,0,1)
  DirMode = 2
  FaceMakerClass = Part::FaceMakerBullseye
  LengthFwd = 10
  LengthRev = 0
  Solid = true
  Symmetric = false
FEATURE [App::Part] worldVOL
  Group = -> [GDMLBox_WorldBox,Sketch,Extrude]
  Origin = -> Origin
